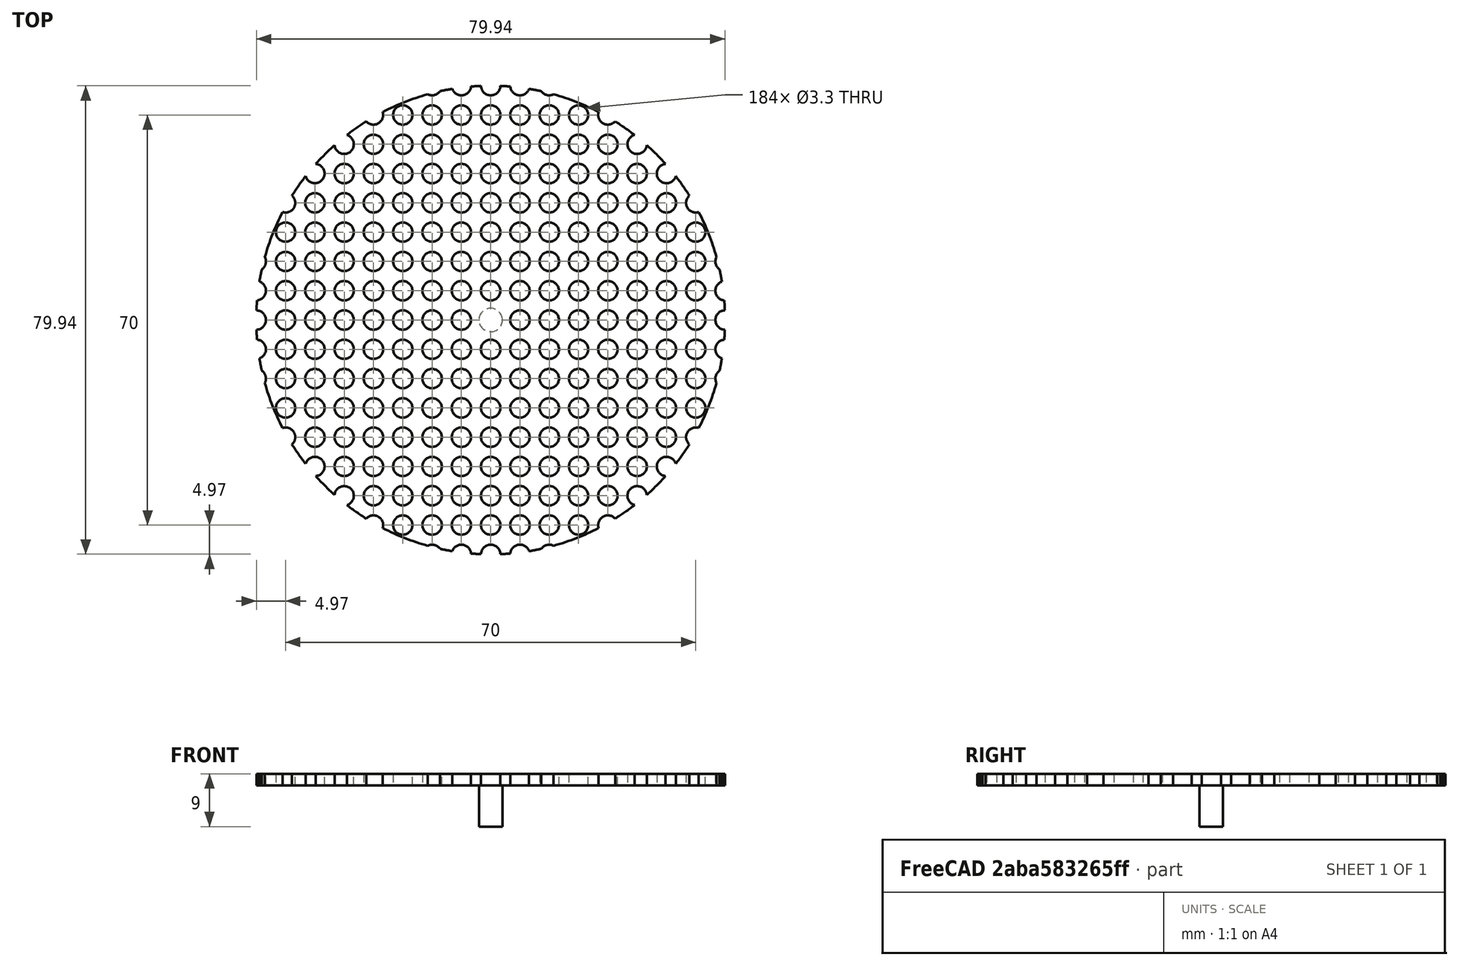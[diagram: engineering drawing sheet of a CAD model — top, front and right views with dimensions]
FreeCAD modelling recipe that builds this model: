
FCSTD DOCUMENT  (FreeCAD 0.21R0.21.1)
Label: XL30SampleholderBreadboard
License: All rights reserved
LicenseURL: https://en.wikipedia.org/wiki/All_rights_reserved
objects: Part::Cylinder×442, Part::MultiFuse×23, Spreadsheet::Sheet×1, Part::Cut×1
note: 466 computed .brp shape members not serialized (recipe doc carries the construction recipe); baked Part::Feature solids carry a one-line shape summary decoded from their .brp

FEATURE [Spreadsheet::Sheet] Spreadsheet  label="BreadboardConfig"
  cells = A1='Parameters; A2='Diameter of stage; B2(dia_breadboard)=80; C2='The outer diameter of the breadboard stage; A3='Corehole diameter; B3(screw_corehole)=3.3; C3='Corehole diameter for screws (3.3mm for M4); A4='Plate thickness; B4(t_plate)=2; A5='Hole spacing; B5(screw_spacing)=5
FEATURE [Part::Cylinder] Cylinder
  Angle = 360
  AttacherType = Attacher::AttachEngine3D
  FirstAngle = 0
  Height = 7
  Placement = pos=(0,0,-7) rot=(0,0,1;0rad)
  Radius = 2
  SecondAngle = 0
FEATURE [Part::Cylinder] Cylinder001
  Angle = 360
  AttacherType = Attacher::AttachEngine3D
  FirstAngle = 0
  Height = 2
  Radius = 40
  SecondAngle = 0
  expr: Height = <<BreadboardConfig>>.t_plate
  expr: Radius = <<BreadboardConfig>>.dia_breadboard / 2
FEATURE [Part::MultiFuse] Fusion
  Shapes = -> [Cylinder,Cylinder001]
FEATURE [Part::Cylinder] Cylinder002
  Angle = 360
  AttacherType = Attacher::AttachEngine3D
  FirstAngle = 0
  Height = 2
  Placement = pos=(5,0,0) rot=(0,0,1;0rad)
  Radius = 1.65
  SecondAngle = 0
  expr: .Placement.Base.x = <<BreadboardConfig>>.screw_spacing * 1
  expr: Height = <<BreadboardConfig>>.t_plate
  expr: Radius = <<BreadboardConfig>>.screw_corehole / 2
FEATURE [Part::Cylinder] Cylinder003
  Angle = 360
  AttacherType = Attacher::AttachEngine3D
  FirstAngle = 0
  Height = 2
  Placement = pos=(10,0,0) rot=(0,0,1;0rad)
  Radius = 1.65
  SecondAngle = 0
  expr: .Placement.Base.x = <<BreadboardConfig>>.screw_spacing * 2
  expr: Height = <<BreadboardConfig>>.t_plate
  expr: Radius = <<BreadboardConfig>>.screw_corehole / 2
FEATURE [Part::Cylinder] Cylinder004
  Angle = 360
  AttacherType = Attacher::AttachEngine3D
  FirstAngle = 0
  Height = 2
  Placement = pos=(15,0,0) rot=(0,0,1;0rad)
  Radius = 1.65
  SecondAngle = 0
  expr: .Placement.Base.x = <<BreadboardConfig>>.screw_spacing * 3
  expr: Height = <<BreadboardConfig>>.t_plate
  expr: Radius = <<BreadboardConfig>>.screw_corehole / 2
FEATURE [Part::Cylinder] Cylinder005
  Angle = 360
  AttacherType = Attacher::AttachEngine3D
  FirstAngle = 0
  Height = 2
  Placement = pos=(20,0,0) rot=(0,0,1;0rad)
  Radius = 1.65
  SecondAngle = 0
  expr: .Placement.Base.x = <<BreadboardConfig>>.screw_spacing * 4
  expr: Height = <<BreadboardConfig>>.t_plate
  expr: Radius = <<BreadboardConfig>>.screw_corehole / 2
FEATURE [Part::Cylinder] Cylinder006
  Angle = 360
  AttacherType = Attacher::AttachEngine3D
  FirstAngle = 0
  Height = 2
  Placement = pos=(25,0,0) rot=(0,0,1;0rad)
  Radius = 1.65
  SecondAngle = 0
  expr: .Placement.Base.x = <<BreadboardConfig>>.screw_spacing * 5
  expr: Height = <<BreadboardConfig>>.t_plate
  expr: Radius = <<BreadboardConfig>>.screw_corehole / 2
FEATURE [Part::Cylinder] Cylinder007
  Angle = 360
  AttacherType = Attacher::AttachEngine3D
  FirstAngle = 0
  Height = 2
  Placement = pos=(30,0,0) rot=(0,0,1;0rad)
  Radius = 1.65
  SecondAngle = 0
  expr: .Placement.Base.x = <<BreadboardConfig>>.screw_spacing * 6
  expr: Height = <<BreadboardConfig>>.t_plate
  expr: Radius = <<BreadboardConfig>>.screw_corehole / 2
FEATURE [Part::Cylinder] Cylinder008
  Angle = 360
  AttacherType = Attacher::AttachEngine3D
  FirstAngle = 0
  Height = 2
  Placement = pos=(35,0,0) rot=(0,0,1;0rad)
  Radius = 1.65
  SecondAngle = 0
  expr: .Placement.Base.x = <<BreadboardConfig>>.screw_spacing * 7
  expr: Height = <<BreadboardConfig>>.t_plate
  expr: Radius = <<BreadboardConfig>>.screw_corehole / 2
FEATURE [Part::Cylinder] Cylinder009
  Angle = 360
  AttacherType = Attacher::AttachEngine3D
  FirstAngle = 0
  Height = 2
  Placement = pos=(40,0,0) rot=(0,0,1;0rad)
  Radius = 1.65
  SecondAngle = 0
  expr: .Placement.Base.x = <<BreadboardConfig>>.screw_spacing * 8
  expr: Height = <<BreadboardConfig>>.t_plate
  expr: Radius = <<BreadboardConfig>>.screw_corehole / 2
FEATURE [Part::Cylinder] Cylinder010
  Angle = 360
  AttacherType = Attacher::AttachEngine3D
  FirstAngle = 0
  Height = 2
  Placement = pos=(45,0,0) rot=(0,0,1;0rad)
  Radius = 1.65
  SecondAngle = 0
  expr: .Placement.Base.x = <<BreadboardConfig>>.screw_spacing * 9
  expr: Height = <<BreadboardConfig>>.t_plate
  expr: Radius = <<BreadboardConfig>>.screw_corehole / 2
FEATURE [Part::Cylinder] Cylinder011
  Angle = 360
  AttacherType = Attacher::AttachEngine3D
  FirstAngle = 0
  Height = 2
  Placement = pos=(50,0,0) rot=(0,0,1;0rad)
  Radius = 1.65
  SecondAngle = 0
  expr: .Placement.Base.x = <<BreadboardConfig>>.screw_spacing * 10
  expr: Height = <<BreadboardConfig>>.t_plate
  expr: Radius = <<BreadboardConfig>>.screw_corehole / 2
FEATURE [Part::Cylinder] Cylinder012
  Angle = 360
  AttacherType = Attacher::AttachEngine3D
  FirstAngle = 0
  Height = 2
  Placement = pos=(-5,0,0) rot=(0,0,1;0rad)
  Radius = 1.65
  SecondAngle = 0
  expr: .Placement.Base.x = <<BreadboardConfig>>.screw_spacing * -1
  expr: Height = <<BreadboardConfig>>.t_plate
  expr: Radius = <<BreadboardConfig>>.screw_corehole / 2
FEATURE [Part::Cylinder] Cylinder013
  Angle = 360
  AttacherType = Attacher::AttachEngine3D
  FirstAngle = 0
  Height = 2
  Placement = pos=(-10,0,0) rot=(0,0,1;0rad)
  Radius = 1.65
  SecondAngle = 0
  expr: .Placement.Base.x = <<BreadboardConfig>>.screw_spacing * -2
  expr: Height = <<BreadboardConfig>>.t_plate
  expr: Radius = <<BreadboardConfig>>.screw_corehole / 2
FEATURE [Part::Cylinder] Cylinder014
  Angle = 360
  AttacherType = Attacher::AttachEngine3D
  FirstAngle = 0
  Height = 2
  Placement = pos=(-15,0,0) rot=(0,0,1;0rad)
  Radius = 1.65
  SecondAngle = 0
  expr: .Placement.Base.x = <<BreadboardConfig>>.screw_spacing * -3
  expr: Height = <<BreadboardConfig>>.t_plate
  expr: Radius = <<BreadboardConfig>>.screw_corehole / 2
FEATURE [Part::Cylinder] Cylinder015
  Angle = 360
  AttacherType = Attacher::AttachEngine3D
  FirstAngle = 0
  Height = 2
  Placement = pos=(-20,0,0) rot=(0,0,1;0rad)
  Radius = 1.65
  SecondAngle = 0
  expr: .Placement.Base.x = <<BreadboardConfig>>.screw_spacing * -4
  expr: Height = <<BreadboardConfig>>.t_plate
  expr: Radius = <<BreadboardConfig>>.screw_corehole / 2
FEATURE [Part::Cylinder] Cylinder016
  Angle = 360
  AttacherType = Attacher::AttachEngine3D
  FirstAngle = 0
  Height = 2
  Placement = pos=(-25,0,0) rot=(0,0,1;0rad)
  Radius = 1.65
  SecondAngle = 0
  expr: .Placement.Base.x = <<BreadboardConfig>>.screw_spacing * -5
  expr: Height = <<BreadboardConfig>>.t_plate
  expr: Radius = <<BreadboardConfig>>.screw_corehole / 2
FEATURE [Part::Cylinder] Cylinder017
  Angle = 360
  AttacherType = Attacher::AttachEngine3D
  FirstAngle = 0
  Height = 2
  Placement = pos=(-30,0,0) rot=(0,0,1;0rad)
  Radius = 1.65
  SecondAngle = 0
  expr: .Placement.Base.x = <<BreadboardConfig>>.screw_spacing * -6
  expr: Height = <<BreadboardConfig>>.t_plate
  expr: Radius = <<BreadboardConfig>>.screw_corehole / 2
FEATURE [Part::Cylinder] Cylinder018
  Angle = 360
  AttacherType = Attacher::AttachEngine3D
  FirstAngle = 0
  Height = 2
  Placement = pos=(-35,0,0) rot=(0,0,1;0rad)
  Radius = 1.65
  SecondAngle = 0
  expr: .Placement.Base.x = <<BreadboardConfig>>.screw_spacing * -7
  expr: Height = <<BreadboardConfig>>.t_plate
  expr: Radius = <<BreadboardConfig>>.screw_corehole / 2
FEATURE [Part::Cylinder] Cylinder019
  Angle = 360
  AttacherType = Attacher::AttachEngine3D
  FirstAngle = 0
  Height = 2
  Placement = pos=(-40,0,0) rot=(0,0,1;0rad)
  Radius = 1.65
  SecondAngle = 0
  expr: .Placement.Base.x = <<BreadboardConfig>>.screw_spacing * -8
  expr: Height = <<BreadboardConfig>>.t_plate
  expr: Radius = <<BreadboardConfig>>.screw_corehole / 2
FEATURE [Part::Cylinder] Cylinder020
  Angle = 360
  AttacherType = Attacher::AttachEngine3D
  FirstAngle = 0
  Height = 2
  Placement = pos=(-45,0,0) rot=(0,0,1;0rad)
  Radius = 1.65
  SecondAngle = 0
  expr: .Placement.Base.x = <<BreadboardConfig>>.screw_spacing * -9
  expr: Height = <<BreadboardConfig>>.t_plate
  expr: Radius = <<BreadboardConfig>>.screw_corehole / 2
FEATURE [Part::Cylinder] Cylinder021
  Angle = 360
  AttacherType = Attacher::AttachEngine3D
  FirstAngle = 0
  Height = 2
  Placement = pos=(-50,0,0) rot=(0,0,1;0rad)
  Radius = 1.65
  SecondAngle = 0
  expr: .Placement.Base.x = <<BreadboardConfig>>.screw_spacing * -10
  expr: Height = <<BreadboardConfig>>.t_plate
  expr: Radius = <<BreadboardConfig>>.screw_corehole / 2
FEATURE [Part::MultiFuse] Fusion001
  Shapes = -> [Cylinder021,Cylinder020,Cylinder019,Cylinder018,Cylinder017,Cylinder016,Cylinder015,Cylinder014,Cylinder013,Cylinder012,Cylinder011,Cylinder010,Cylinder009,Cylinder008,Cylinder007,Cylinder006,Cylinder005,Cylinder004,Cylinder003,Cylinder002]
FEATURE [Part::Cylinder] Cylinder022
  Angle = 360
  AttacherType = Attacher::AttachEngine3D
  FirstAngle = 0
  Height = 2
  Placement = pos=(5,0,0) rot=(0,0,1;0rad)
  Radius = 1.65
  SecondAngle = 0
  expr: .Placement.Base.x = <<BreadboardConfig>>.screw_spacing * 1
  expr: Height = <<BreadboardConfig>>.t_plate
  expr: Radius = <<BreadboardConfig>>.screw_corehole / 2
FEATURE [Part::Cylinder] Cylinder023
  Angle = 360
  AttacherType = Attacher::AttachEngine3D
  FirstAngle = 0
  Height = 2
  Placement = pos=(10,0,0) rot=(0,0,1;0rad)
  Radius = 1.65
  SecondAngle = 0
  expr: .Placement.Base.x = <<BreadboardConfig>>.screw_spacing * 2
  expr: Height = <<BreadboardConfig>>.t_plate
  expr: Radius = <<BreadboardConfig>>.screw_corehole / 2
FEATURE [Part::Cylinder] Cylinder024
  Angle = 360
  AttacherType = Attacher::AttachEngine3D
  FirstAngle = 0
  Height = 2
  Placement = pos=(15,0,0) rot=(0,0,1;0rad)
  Radius = 1.65
  SecondAngle = 0
  expr: .Placement.Base.x = <<BreadboardConfig>>.screw_spacing * 3
  expr: Height = <<BreadboardConfig>>.t_plate
  expr: Radius = <<BreadboardConfig>>.screw_corehole / 2
FEATURE [Part::Cylinder] Cylinder025
  Angle = 360
  AttacherType = Attacher::AttachEngine3D
  FirstAngle = 0
  Height = 2
  Placement = pos=(20,0,0) rot=(0,0,1;0rad)
  Radius = 1.65
  SecondAngle = 0
  expr: .Placement.Base.x = <<BreadboardConfig>>.screw_spacing * 4
  expr: Height = <<BreadboardConfig>>.t_plate
  expr: Radius = <<BreadboardConfig>>.screw_corehole / 2
FEATURE [Part::Cylinder] Cylinder026
  Angle = 360
  AttacherType = Attacher::AttachEngine3D
  FirstAngle = 0
  Height = 2
  Placement = pos=(25,0,0) rot=(0,0,1;0rad)
  Radius = 1.65
  SecondAngle = 0
  expr: .Placement.Base.x = <<BreadboardConfig>>.screw_spacing * 5
  expr: Height = <<BreadboardConfig>>.t_plate
  expr: Radius = <<BreadboardConfig>>.screw_corehole / 2
FEATURE [Part::Cylinder] Cylinder027
  Angle = 360
  AttacherType = Attacher::AttachEngine3D
  FirstAngle = 0
  Height = 2
  Placement = pos=(30,0,0) rot=(0,0,1;0rad)
  Radius = 1.65
  SecondAngle = 0
  expr: .Placement.Base.x = <<BreadboardConfig>>.screw_spacing * 6
  expr: Height = <<BreadboardConfig>>.t_plate
  expr: Radius = <<BreadboardConfig>>.screw_corehole / 2
FEATURE [Part::Cylinder] Cylinder028
  Angle = 360
  AttacherType = Attacher::AttachEngine3D
  FirstAngle = 0
  Height = 2
  Placement = pos=(35,0,0) rot=(0,0,1;0rad)
  Radius = 1.65
  SecondAngle = 0
  expr: .Placement.Base.x = <<BreadboardConfig>>.screw_spacing * 7
  expr: Height = <<BreadboardConfig>>.t_plate
  expr: Radius = <<BreadboardConfig>>.screw_corehole / 2
FEATURE [Part::Cylinder] Cylinder029
  Angle = 360
  AttacherType = Attacher::AttachEngine3D
  FirstAngle = 0
  Height = 2
  Placement = pos=(40,0,0) rot=(0,0,1;0rad)
  Radius = 1.65
  SecondAngle = 0
  expr: .Placement.Base.x = <<BreadboardConfig>>.screw_spacing * 8
  expr: Height = <<BreadboardConfig>>.t_plate
  expr: Radius = <<BreadboardConfig>>.screw_corehole / 2
FEATURE [Part::Cylinder] Cylinder030
  Angle = 360
  AttacherType = Attacher::AttachEngine3D
  FirstAngle = 0
  Height = 2
  Placement = pos=(45,0,0) rot=(0,0,1;0rad)
  Radius = 1.65
  SecondAngle = 0
  expr: .Placement.Base.x = <<BreadboardConfig>>.screw_spacing * 9
  expr: Height = <<BreadboardConfig>>.t_plate
  expr: Radius = <<BreadboardConfig>>.screw_corehole / 2
FEATURE [Part::Cylinder] Cylinder031
  Angle = 360
  AttacherType = Attacher::AttachEngine3D
  FirstAngle = 0
  Height = 2
  Placement = pos=(50,0,0) rot=(0,0,1;0rad)
  Radius = 1.65
  SecondAngle = 0
  expr: .Placement.Base.x = <<BreadboardConfig>>.screw_spacing * 10
  expr: Height = <<BreadboardConfig>>.t_plate
  expr: Radius = <<BreadboardConfig>>.screw_corehole / 2
FEATURE [Part::Cylinder] Cylinder032
  Angle = 360
  AttacherType = Attacher::AttachEngine3D
  FirstAngle = 0
  Height = 2
  Placement = pos=(-5,0,0) rot=(0,0,1;0rad)
  Radius = 1.65
  SecondAngle = 0
  expr: .Placement.Base.x = <<BreadboardConfig>>.screw_spacing * -1
  expr: Height = <<BreadboardConfig>>.t_plate
  expr: Radius = <<BreadboardConfig>>.screw_corehole / 2
FEATURE [Part::Cylinder] Cylinder033
  Angle = 360
  AttacherType = Attacher::AttachEngine3D
  FirstAngle = 0
  Height = 2
  Placement = pos=(-10,0,0) rot=(0,0,1;0rad)
  Radius = 1.65
  SecondAngle = 0
  expr: .Placement.Base.x = <<BreadboardConfig>>.screw_spacing * -2
  expr: Height = <<BreadboardConfig>>.t_plate
  expr: Radius = <<BreadboardConfig>>.screw_corehole / 2
FEATURE [Part::Cylinder] Cylinder034
  Angle = 360
  AttacherType = Attacher::AttachEngine3D
  FirstAngle = 0
  Height = 2
  Placement = pos=(-15,0,0) rot=(0,0,1;0rad)
  Radius = 1.65
  SecondAngle = 0
  expr: .Placement.Base.x = <<BreadboardConfig>>.screw_spacing * -3
  expr: Height = <<BreadboardConfig>>.t_plate
  expr: Radius = <<BreadboardConfig>>.screw_corehole / 2
FEATURE [Part::Cylinder] Cylinder035
  Angle = 360
  AttacherType = Attacher::AttachEngine3D
  FirstAngle = 0
  Height = 2
  Placement = pos=(-20,0,0) rot=(0,0,1;0rad)
  Radius = 1.65
  SecondAngle = 0
  expr: .Placement.Base.x = <<BreadboardConfig>>.screw_spacing * -4
  expr: Height = <<BreadboardConfig>>.t_plate
  expr: Radius = <<BreadboardConfig>>.screw_corehole / 2
FEATURE [Part::Cylinder] Cylinder036
  Angle = 360
  AttacherType = Attacher::AttachEngine3D
  FirstAngle = 0
  Height = 2
  Placement = pos=(-25,0,0) rot=(0,0,1;0rad)
  Radius = 1.65
  SecondAngle = 0
  expr: .Placement.Base.x = <<BreadboardConfig>>.screw_spacing * -5
  expr: Height = <<BreadboardConfig>>.t_plate
  expr: Radius = <<BreadboardConfig>>.screw_corehole / 2
FEATURE [Part::Cylinder] Cylinder037
  Angle = 360
  AttacherType = Attacher::AttachEngine3D
  FirstAngle = 0
  Height = 2
  Placement = pos=(-30,0,0) rot=(0,0,1;0rad)
  Radius = 1.65
  SecondAngle = 0
  expr: .Placement.Base.x = <<BreadboardConfig>>.screw_spacing * -6
  expr: Height = <<BreadboardConfig>>.t_plate
  expr: Radius = <<BreadboardConfig>>.screw_corehole / 2
FEATURE [Part::Cylinder] Cylinder038
  Angle = 360
  AttacherType = Attacher::AttachEngine3D
  FirstAngle = 0
  Height = 2
  Placement = pos=(-35,0,0) rot=(0,0,1;0rad)
  Radius = 1.65
  SecondAngle = 0
  expr: .Placement.Base.x = <<BreadboardConfig>>.screw_spacing * -7
  expr: Height = <<BreadboardConfig>>.t_plate
  expr: Radius = <<BreadboardConfig>>.screw_corehole / 2
FEATURE [Part::Cylinder] Cylinder039
  Angle = 360
  AttacherType = Attacher::AttachEngine3D
  FirstAngle = 0
  Height = 2
  Placement = pos=(-40,0,0) rot=(0,0,1;0rad)
  Radius = 1.65
  SecondAngle = 0
  expr: .Placement.Base.x = <<BreadboardConfig>>.screw_spacing * -8
  expr: Height = <<BreadboardConfig>>.t_plate
  expr: Radius = <<BreadboardConfig>>.screw_corehole / 2
FEATURE [Part::Cylinder] Cylinder040
  Angle = 360
  AttacherType = Attacher::AttachEngine3D
  FirstAngle = 0
  Height = 2
  Placement = pos=(-45,0,0) rot=(0,0,1;0rad)
  Radius = 1.65
  SecondAngle = 0
  expr: .Placement.Base.x = <<BreadboardConfig>>.screw_spacing * -9
  expr: Height = <<BreadboardConfig>>.t_plate
  expr: Radius = <<BreadboardConfig>>.screw_corehole / 2
FEATURE [Part::Cylinder] Cylinder041
  Angle = 360
  AttacherType = Attacher::AttachEngine3D
  FirstAngle = 0
  Height = 2
  Placement = pos=(-50,0,0) rot=(0,0,1;0rad)
  Radius = 1.65
  SecondAngle = 0
  expr: .Placement.Base.x = <<BreadboardConfig>>.screw_spacing * -10
  expr: Height = <<BreadboardConfig>>.t_plate
  expr: Radius = <<BreadboardConfig>>.screw_corehole / 2
FEATURE [Part::Cylinder] Cylinder042
  Angle = 360
  AttacherType = Attacher::AttachEngine3D
  FirstAngle = 0
  Height = 2
  Radius = 1.65
  SecondAngle = 0
  expr: Height = <<BreadboardConfig>>.t_plate
  expr: Radius = <<BreadboardConfig>>.screw_corehole / 2
FEATURE [Part::MultiFuse] Fusion002
  Placement = pos=(0,5,0) rot=(0,0,1;0rad)
  Shapes = -> [Cylinder041,Cylinder040,Cylinder039,Cylinder038,Cylinder037,Cylinder036,Cylinder035,Cylinder034,Cylinder033,Cylinder032,Cylinder031,Cylinder030,Cylinder029,Cylinder028,Cylinder027,Cylinder026,Cylinder025,Cylinder024,Cylinder023,Cylinder022,Cylinder042]
  expr: .Placement.Base.y = <<BreadboardConfig>>.screw_spacing
FEATURE [Part::Cylinder] Cylinder043
  Angle = 360
  AttacherType = Attacher::AttachEngine3D
  FirstAngle = 0
  Height = 2
  Placement = pos=(5,0,0) rot=(0,0,1;0rad)
  Radius = 1.65
  SecondAngle = 0
  expr: .Placement.Base.x = <<BreadboardConfig>>.screw_spacing * 1
  expr: Height = <<BreadboardConfig>>.t_plate
  expr: Radius = <<BreadboardConfig>>.screw_corehole / 2
FEATURE [Part::Cylinder] Cylinder044
  Angle = 360
  AttacherType = Attacher::AttachEngine3D
  FirstAngle = 0
  Height = 2
  Placement = pos=(10,0,0) rot=(0,0,1;0rad)
  Radius = 1.65
  SecondAngle = 0
  expr: .Placement.Base.x = <<BreadboardConfig>>.screw_spacing * 2
  expr: Height = <<BreadboardConfig>>.t_plate
  expr: Radius = <<BreadboardConfig>>.screw_corehole / 2
FEATURE [Part::Cylinder] Cylinder045
  Angle = 360
  AttacherType = Attacher::AttachEngine3D
  FirstAngle = 0
  Height = 2
  Placement = pos=(15,0,0) rot=(0,0,1;0rad)
  Radius = 1.65
  SecondAngle = 0
  expr: .Placement.Base.x = <<BreadboardConfig>>.screw_spacing * 3
  expr: Height = <<BreadboardConfig>>.t_plate
  expr: Radius = <<BreadboardConfig>>.screw_corehole / 2
FEATURE [Part::Cylinder] Cylinder046
  Angle = 360
  AttacherType = Attacher::AttachEngine3D
  FirstAngle = 0
  Height = 2
  Placement = pos=(20,0,0) rot=(0,0,1;0rad)
  Radius = 1.65
  SecondAngle = 0
  expr: .Placement.Base.x = <<BreadboardConfig>>.screw_spacing * 4
  expr: Height = <<BreadboardConfig>>.t_plate
  expr: Radius = <<BreadboardConfig>>.screw_corehole / 2
FEATURE [Part::Cylinder] Cylinder047
  Angle = 360
  AttacherType = Attacher::AttachEngine3D
  FirstAngle = 0
  Height = 2
  Placement = pos=(25,0,0) rot=(0,0,1;0rad)
  Radius = 1.65
  SecondAngle = 0
  expr: .Placement.Base.x = <<BreadboardConfig>>.screw_spacing * 5
  expr: Height = <<BreadboardConfig>>.t_plate
  expr: Radius = <<BreadboardConfig>>.screw_corehole / 2
FEATURE [Part::Cylinder] Cylinder048
  Angle = 360
  AttacherType = Attacher::AttachEngine3D
  FirstAngle = 0
  Height = 2
  Placement = pos=(30,0,0) rot=(0,0,1;0rad)
  Radius = 1.65
  SecondAngle = 0
  expr: .Placement.Base.x = <<BreadboardConfig>>.screw_spacing * 6
  expr: Height = <<BreadboardConfig>>.t_plate
  expr: Radius = <<BreadboardConfig>>.screw_corehole / 2
FEATURE [Part::Cylinder] Cylinder049
  Angle = 360
  AttacherType = Attacher::AttachEngine3D
  FirstAngle = 0
  Height = 2
  Placement = pos=(35,0,0) rot=(0,0,1;0rad)
  Radius = 1.65
  SecondAngle = 0
  expr: .Placement.Base.x = <<BreadboardConfig>>.screw_spacing * 7
  expr: Height = <<BreadboardConfig>>.t_plate
  expr: Radius = <<BreadboardConfig>>.screw_corehole / 2
FEATURE [Part::Cylinder] Cylinder050
  Angle = 360
  AttacherType = Attacher::AttachEngine3D
  FirstAngle = 0
  Height = 2
  Placement = pos=(40,0,0) rot=(0,0,1;0rad)
  Radius = 1.65
  SecondAngle = 0
  expr: .Placement.Base.x = <<BreadboardConfig>>.screw_spacing * 8
  expr: Height = <<BreadboardConfig>>.t_plate
  expr: Radius = <<BreadboardConfig>>.screw_corehole / 2
FEATURE [Part::Cylinder] Cylinder051
  Angle = 360
  AttacherType = Attacher::AttachEngine3D
  FirstAngle = 0
  Height = 2
  Placement = pos=(45,0,0) rot=(0,0,1;0rad)
  Radius = 1.65
  SecondAngle = 0
  expr: .Placement.Base.x = <<BreadboardConfig>>.screw_spacing * 9
  expr: Height = <<BreadboardConfig>>.t_plate
  expr: Radius = <<BreadboardConfig>>.screw_corehole / 2
FEATURE [Part::Cylinder] Cylinder052
  Angle = 360
  AttacherType = Attacher::AttachEngine3D
  FirstAngle = 0
  Height = 2
  Placement = pos=(50,0,0) rot=(0,0,1;0rad)
  Radius = 1.65
  SecondAngle = 0
  expr: .Placement.Base.x = <<BreadboardConfig>>.screw_spacing * 10
  expr: Height = <<BreadboardConfig>>.t_plate
  expr: Radius = <<BreadboardConfig>>.screw_corehole / 2
FEATURE [Part::Cylinder] Cylinder053
  Angle = 360
  AttacherType = Attacher::AttachEngine3D
  FirstAngle = 0
  Height = 2
  Placement = pos=(-5,0,0) rot=(0,0,1;0rad)
  Radius = 1.65
  SecondAngle = 0
  expr: .Placement.Base.x = <<BreadboardConfig>>.screw_spacing * -1
  expr: Height = <<BreadboardConfig>>.t_plate
  expr: Radius = <<BreadboardConfig>>.screw_corehole / 2
FEATURE [Part::Cylinder] Cylinder054
  Angle = 360
  AttacherType = Attacher::AttachEngine3D
  FirstAngle = 0
  Height = 2
  Placement = pos=(-10,0,0) rot=(0,0,1;0rad)
  Radius = 1.65
  SecondAngle = 0
  expr: .Placement.Base.x = <<BreadboardConfig>>.screw_spacing * -2
  expr: Height = <<BreadboardConfig>>.t_plate
  expr: Radius = <<BreadboardConfig>>.screw_corehole / 2
FEATURE [Part::Cylinder] Cylinder055
  Angle = 360
  AttacherType = Attacher::AttachEngine3D
  FirstAngle = 0
  Height = 2
  Placement = pos=(-15,0,0) rot=(0,0,1;0rad)
  Radius = 1.65
  SecondAngle = 0
  expr: .Placement.Base.x = <<BreadboardConfig>>.screw_spacing * -3
  expr: Height = <<BreadboardConfig>>.t_plate
  expr: Radius = <<BreadboardConfig>>.screw_corehole / 2
FEATURE [Part::Cylinder] Cylinder056
  Angle = 360
  AttacherType = Attacher::AttachEngine3D
  FirstAngle = 0
  Height = 2
  Placement = pos=(-20,0,0) rot=(0,0,1;0rad)
  Radius = 1.65
  SecondAngle = 0
  expr: .Placement.Base.x = <<BreadboardConfig>>.screw_spacing * -4
  expr: Height = <<BreadboardConfig>>.t_plate
  expr: Radius = <<BreadboardConfig>>.screw_corehole / 2
FEATURE [Part::Cylinder] Cylinder057
  Angle = 360
  AttacherType = Attacher::AttachEngine3D
  FirstAngle = 0
  Height = 2
  Placement = pos=(-25,0,0) rot=(0,0,1;0rad)
  Radius = 1.65
  SecondAngle = 0
  expr: .Placement.Base.x = <<BreadboardConfig>>.screw_spacing * -5
  expr: Height = <<BreadboardConfig>>.t_plate
  expr: Radius = <<BreadboardConfig>>.screw_corehole / 2
FEATURE [Part::Cylinder] Cylinder058
  Angle = 360
  AttacherType = Attacher::AttachEngine3D
  FirstAngle = 0
  Height = 2
  Placement = pos=(-30,0,0) rot=(0,0,1;0rad)
  Radius = 1.65
  SecondAngle = 0
  expr: .Placement.Base.x = <<BreadboardConfig>>.screw_spacing * -6
  expr: Height = <<BreadboardConfig>>.t_plate
  expr: Radius = <<BreadboardConfig>>.screw_corehole / 2
FEATURE [Part::Cylinder] Cylinder059
  Angle = 360
  AttacherType = Attacher::AttachEngine3D
  FirstAngle = 0
  Height = 2
  Placement = pos=(-35,0,0) rot=(0,0,1;0rad)
  Radius = 1.65
  SecondAngle = 0
  expr: .Placement.Base.x = <<BreadboardConfig>>.screw_spacing * -7
  expr: Height = <<BreadboardConfig>>.t_plate
  expr: Radius = <<BreadboardConfig>>.screw_corehole / 2
FEATURE [Part::Cylinder] Cylinder060
  Angle = 360
  AttacherType = Attacher::AttachEngine3D
  FirstAngle = 0
  Height = 2
  Placement = pos=(-40,0,0) rot=(0,0,1;0rad)
  Radius = 1.65
  SecondAngle = 0
  expr: .Placement.Base.x = <<BreadboardConfig>>.screw_spacing * -8
  expr: Height = <<BreadboardConfig>>.t_plate
  expr: Radius = <<BreadboardConfig>>.screw_corehole / 2
FEATURE [Part::Cylinder] Cylinder061
  Angle = 360
  AttacherType = Attacher::AttachEngine3D
  FirstAngle = 0
  Height = 2
  Placement = pos=(-45,0,0) rot=(0,0,1;0rad)
  Radius = 1.65
  SecondAngle = 0
  expr: .Placement.Base.x = <<BreadboardConfig>>.screw_spacing * -9
  expr: Height = <<BreadboardConfig>>.t_plate
  expr: Radius = <<BreadboardConfig>>.screw_corehole / 2
FEATURE [Part::Cylinder] Cylinder062
  Angle = 360
  AttacherType = Attacher::AttachEngine3D
  FirstAngle = 0
  Height = 2
  Placement = pos=(-50,0,0) rot=(0,0,1;0rad)
  Radius = 1.65
  SecondAngle = 0
  expr: .Placement.Base.x = <<BreadboardConfig>>.screw_spacing * -10
  expr: Height = <<BreadboardConfig>>.t_plate
  expr: Radius = <<BreadboardConfig>>.screw_corehole / 2
FEATURE [Part::Cylinder] Cylinder063
  Angle = 360
  AttacherType = Attacher::AttachEngine3D
  FirstAngle = 0
  Height = 2
  Radius = 1.65
  SecondAngle = 0
  expr: Height = <<BreadboardConfig>>.t_plate
  expr: Radius = <<BreadboardConfig>>.screw_corehole / 2
FEATURE [Part::MultiFuse] Fusion003
  Placement = pos=(0,10,0) rot=(0,0,1;0rad)
  Shapes = -> [Cylinder062,Cylinder061,Cylinder060,Cylinder059,Cylinder058,Cylinder057,Cylinder056,Cylinder055,Cylinder054,Cylinder053,Cylinder052,Cylinder051,Cylinder050,Cylinder049,Cylinder048,Cylinder047,Cylinder046,Cylinder045,Cylinder044,Cylinder043,Cylinder063]
  expr: .Placement.Base.y = <<BreadboardConfig>>.screw_spacing * 2
FEATURE [Part::Cylinder] Cylinder064
  Angle = 360
  AttacherType = Attacher::AttachEngine3D
  FirstAngle = 0
  Height = 2
  Placement = pos=(5,0,0) rot=(0,0,1;0rad)
  Radius = 1.65
  SecondAngle = 0
  expr: .Placement.Base.x = <<BreadboardConfig>>.screw_spacing * 1
  expr: Height = <<BreadboardConfig>>.t_plate
  expr: Radius = <<BreadboardConfig>>.screw_corehole / 2
FEATURE [Part::Cylinder] Cylinder065
  Angle = 360
  AttacherType = Attacher::AttachEngine3D
  FirstAngle = 0
  Height = 2
  Placement = pos=(10,0,0) rot=(0,0,1;0rad)
  Radius = 1.65
  SecondAngle = 0
  expr: .Placement.Base.x = <<BreadboardConfig>>.screw_spacing * 2
  expr: Height = <<BreadboardConfig>>.t_plate
  expr: Radius = <<BreadboardConfig>>.screw_corehole / 2
FEATURE [Part::Cylinder] Cylinder066
  Angle = 360
  AttacherType = Attacher::AttachEngine3D
  FirstAngle = 0
  Height = 2
  Placement = pos=(15,0,0) rot=(0,0,1;0rad)
  Radius = 1.65
  SecondAngle = 0
  expr: .Placement.Base.x = <<BreadboardConfig>>.screw_spacing * 3
  expr: Height = <<BreadboardConfig>>.t_plate
  expr: Radius = <<BreadboardConfig>>.screw_corehole / 2
FEATURE [Part::Cylinder] Cylinder067
  Angle = 360
  AttacherType = Attacher::AttachEngine3D
  FirstAngle = 0
  Height = 2
  Placement = pos=(20,0,0) rot=(0,0,1;0rad)
  Radius = 1.65
  SecondAngle = 0
  expr: .Placement.Base.x = <<BreadboardConfig>>.screw_spacing * 4
  expr: Height = <<BreadboardConfig>>.t_plate
  expr: Radius = <<BreadboardConfig>>.screw_corehole / 2
FEATURE [Part::Cylinder] Cylinder068
  Angle = 360
  AttacherType = Attacher::AttachEngine3D
  FirstAngle = 0
  Height = 2
  Placement = pos=(25,0,0) rot=(0,0,1;0rad)
  Radius = 1.65
  SecondAngle = 0
  expr: .Placement.Base.x = <<BreadboardConfig>>.screw_spacing * 5
  expr: Height = <<BreadboardConfig>>.t_plate
  expr: Radius = <<BreadboardConfig>>.screw_corehole / 2
FEATURE [Part::Cylinder] Cylinder069
  Angle = 360
  AttacherType = Attacher::AttachEngine3D
  FirstAngle = 0
  Height = 2
  Placement = pos=(30,0,0) rot=(0,0,1;0rad)
  Radius = 1.65
  SecondAngle = 0
  expr: .Placement.Base.x = <<BreadboardConfig>>.screw_spacing * 6
  expr: Height = <<BreadboardConfig>>.t_plate
  expr: Radius = <<BreadboardConfig>>.screw_corehole / 2
FEATURE [Part::Cylinder] Cylinder070
  Angle = 360
  AttacherType = Attacher::AttachEngine3D
  FirstAngle = 0
  Height = 2
  Placement = pos=(35,0,0) rot=(0,0,1;0rad)
  Radius = 1.65
  SecondAngle = 0
  expr: .Placement.Base.x = <<BreadboardConfig>>.screw_spacing * 7
  expr: Height = <<BreadboardConfig>>.t_plate
  expr: Radius = <<BreadboardConfig>>.screw_corehole / 2
FEATURE [Part::Cylinder] Cylinder071
  Angle = 360
  AttacherType = Attacher::AttachEngine3D
  FirstAngle = 0
  Height = 2
  Placement = pos=(40,0,0) rot=(0,0,1;0rad)
  Radius = 1.65
  SecondAngle = 0
  expr: .Placement.Base.x = <<BreadboardConfig>>.screw_spacing * 8
  expr: Height = <<BreadboardConfig>>.t_plate
  expr: Radius = <<BreadboardConfig>>.screw_corehole / 2
FEATURE [Part::Cylinder] Cylinder072
  Angle = 360
  AttacherType = Attacher::AttachEngine3D
  FirstAngle = 0
  Height = 2
  Placement = pos=(45,0,0) rot=(0,0,1;0rad)
  Radius = 1.65
  SecondAngle = 0
  expr: .Placement.Base.x = <<BreadboardConfig>>.screw_spacing * 9
  expr: Height = <<BreadboardConfig>>.t_plate
  expr: Radius = <<BreadboardConfig>>.screw_corehole / 2
FEATURE [Part::Cylinder] Cylinder073
  Angle = 360
  AttacherType = Attacher::AttachEngine3D
  FirstAngle = 0
  Height = 2
  Placement = pos=(50,0,0) rot=(0,0,1;0rad)
  Radius = 1.65
  SecondAngle = 0
  expr: .Placement.Base.x = <<BreadboardConfig>>.screw_spacing * 10
  expr: Height = <<BreadboardConfig>>.t_plate
  expr: Radius = <<BreadboardConfig>>.screw_corehole / 2
FEATURE [Part::Cylinder] Cylinder074
  Angle = 360
  AttacherType = Attacher::AttachEngine3D
  FirstAngle = 0
  Height = 2
  Placement = pos=(-5,0,0) rot=(0,0,1;0rad)
  Radius = 1.65
  SecondAngle = 0
  expr: .Placement.Base.x = <<BreadboardConfig>>.screw_spacing * -1
  expr: Height = <<BreadboardConfig>>.t_plate
  expr: Radius = <<BreadboardConfig>>.screw_corehole / 2
FEATURE [Part::Cylinder] Cylinder075
  Angle = 360
  AttacherType = Attacher::AttachEngine3D
  FirstAngle = 0
  Height = 2
  Placement = pos=(-10,0,0) rot=(0,0,1;0rad)
  Radius = 1.65
  SecondAngle = 0
  expr: .Placement.Base.x = <<BreadboardConfig>>.screw_spacing * -2
  expr: Height = <<BreadboardConfig>>.t_plate
  expr: Radius = <<BreadboardConfig>>.screw_corehole / 2
FEATURE [Part::Cylinder] Cylinder076
  Angle = 360
  AttacherType = Attacher::AttachEngine3D
  FirstAngle = 0
  Height = 2
  Placement = pos=(-15,0,0) rot=(0,0,1;0rad)
  Radius = 1.65
  SecondAngle = 0
  expr: .Placement.Base.x = <<BreadboardConfig>>.screw_spacing * -3
  expr: Height = <<BreadboardConfig>>.t_plate
  expr: Radius = <<BreadboardConfig>>.screw_corehole / 2
FEATURE [Part::Cylinder] Cylinder077
  Angle = 360
  AttacherType = Attacher::AttachEngine3D
  FirstAngle = 0
  Height = 2
  Placement = pos=(-20,0,0) rot=(0,0,1;0rad)
  Radius = 1.65
  SecondAngle = 0
  expr: .Placement.Base.x = <<BreadboardConfig>>.screw_spacing * -4
  expr: Height = <<BreadboardConfig>>.t_plate
  expr: Radius = <<BreadboardConfig>>.screw_corehole / 2
FEATURE [Part::Cylinder] Cylinder078
  Angle = 360
  AttacherType = Attacher::AttachEngine3D
  FirstAngle = 0
  Height = 2
  Placement = pos=(-25,0,0) rot=(0,0,1;0rad)
  Radius = 1.65
  SecondAngle = 0
  expr: .Placement.Base.x = <<BreadboardConfig>>.screw_spacing * -5
  expr: Height = <<BreadboardConfig>>.t_plate
  expr: Radius = <<BreadboardConfig>>.screw_corehole / 2
FEATURE [Part::Cylinder] Cylinder079
  Angle = 360
  AttacherType = Attacher::AttachEngine3D
  FirstAngle = 0
  Height = 2
  Placement = pos=(-30,0,0) rot=(0,0,1;0rad)
  Radius = 1.65
  SecondAngle = 0
  expr: .Placement.Base.x = <<BreadboardConfig>>.screw_spacing * -6
  expr: Height = <<BreadboardConfig>>.t_plate
  expr: Radius = <<BreadboardConfig>>.screw_corehole / 2
FEATURE [Part::Cylinder] Cylinder080
  Angle = 360
  AttacherType = Attacher::AttachEngine3D
  FirstAngle = 0
  Height = 2
  Placement = pos=(-35,0,0) rot=(0,0,1;0rad)
  Radius = 1.65
  SecondAngle = 0
  expr: .Placement.Base.x = <<BreadboardConfig>>.screw_spacing * -7
  expr: Height = <<BreadboardConfig>>.t_plate
  expr: Radius = <<BreadboardConfig>>.screw_corehole / 2
FEATURE [Part::Cylinder] Cylinder081
  Angle = 360
  AttacherType = Attacher::AttachEngine3D
  FirstAngle = 0
  Height = 2
  Placement = pos=(-40,0,0) rot=(0,0,1;0rad)
  Radius = 1.65
  SecondAngle = 0
  expr: .Placement.Base.x = <<BreadboardConfig>>.screw_spacing * -8
  expr: Height = <<BreadboardConfig>>.t_plate
  expr: Radius = <<BreadboardConfig>>.screw_corehole / 2
FEATURE [Part::Cylinder] Cylinder082
  Angle = 360
  AttacherType = Attacher::AttachEngine3D
  FirstAngle = 0
  Height = 2
  Placement = pos=(-45,0,0) rot=(0,0,1;0rad)
  Radius = 1.65
  SecondAngle = 0
  expr: .Placement.Base.x = <<BreadboardConfig>>.screw_spacing * -9
  expr: Height = <<BreadboardConfig>>.t_plate
  expr: Radius = <<BreadboardConfig>>.screw_corehole / 2
FEATURE [Part::Cylinder] Cylinder083
  Angle = 360
  AttacherType = Attacher::AttachEngine3D
  FirstAngle = 0
  Height = 2
  Placement = pos=(-50,0,0) rot=(0,0,1;0rad)
  Radius = 1.65
  SecondAngle = 0
  expr: .Placement.Base.x = <<BreadboardConfig>>.screw_spacing * -10
  expr: Height = <<BreadboardConfig>>.t_plate
  expr: Radius = <<BreadboardConfig>>.screw_corehole / 2
FEATURE [Part::Cylinder] Cylinder084
  Angle = 360
  AttacherType = Attacher::AttachEngine3D
  FirstAngle = 0
  Height = 2
  Radius = 1.65
  SecondAngle = 0
  expr: Height = <<BreadboardConfig>>.t_plate
  expr: Radius = <<BreadboardConfig>>.screw_corehole / 2
FEATURE [Part::MultiFuse] Fusion004
  Placement = pos=(0,15,0) rot=(0,0,1;0rad)
  Shapes = -> [Cylinder083,Cylinder082,Cylinder081,Cylinder080,Cylinder079,Cylinder078,Cylinder077,Cylinder076,Cylinder075,Cylinder074,Cylinder073,Cylinder072,Cylinder071,Cylinder070,Cylinder069,Cylinder068,Cylinder067,Cylinder066,Cylinder065,Cylinder064,Cylinder084]
  expr: .Placement.Base.y = <<BreadboardConfig>>.screw_spacing * 3
FEATURE [Part::Cylinder] Cylinder085
  Angle = 360
  AttacherType = Attacher::AttachEngine3D
  FirstAngle = 0
  Height = 2
  Placement = pos=(5,0,0) rot=(0,0,1;0rad)
  Radius = 1.65
  SecondAngle = 0
  expr: .Placement.Base.x = <<BreadboardConfig>>.screw_spacing * 1
  expr: Height = <<BreadboardConfig>>.t_plate
  expr: Radius = <<BreadboardConfig>>.screw_corehole / 2
FEATURE [Part::Cylinder] Cylinder086
  Angle = 360
  AttacherType = Attacher::AttachEngine3D
  FirstAngle = 0
  Height = 2
  Placement = pos=(10,0,0) rot=(0,0,1;0rad)
  Radius = 1.65
  SecondAngle = 0
  expr: .Placement.Base.x = <<BreadboardConfig>>.screw_spacing * 2
  expr: Height = <<BreadboardConfig>>.t_plate
  expr: Radius = <<BreadboardConfig>>.screw_corehole / 2
FEATURE [Part::Cylinder] Cylinder087
  Angle = 360
  AttacherType = Attacher::AttachEngine3D
  FirstAngle = 0
  Height = 2
  Placement = pos=(15,0,0) rot=(0,0,1;0rad)
  Radius = 1.65
  SecondAngle = 0
  expr: .Placement.Base.x = <<BreadboardConfig>>.screw_spacing * 3
  expr: Height = <<BreadboardConfig>>.t_plate
  expr: Radius = <<BreadboardConfig>>.screw_corehole / 2
FEATURE [Part::Cylinder] Cylinder088
  Angle = 360
  AttacherType = Attacher::AttachEngine3D
  FirstAngle = 0
  Height = 2
  Placement = pos=(20,0,0) rot=(0,0,1;0rad)
  Radius = 1.65
  SecondAngle = 0
  expr: .Placement.Base.x = <<BreadboardConfig>>.screw_spacing * 4
  expr: Height = <<BreadboardConfig>>.t_plate
  expr: Radius = <<BreadboardConfig>>.screw_corehole / 2
FEATURE [Part::Cylinder] Cylinder089
  Angle = 360
  AttacherType = Attacher::AttachEngine3D
  FirstAngle = 0
  Height = 2
  Placement = pos=(25,0,0) rot=(0,0,1;0rad)
  Radius = 1.65
  SecondAngle = 0
  expr: .Placement.Base.x = <<BreadboardConfig>>.screw_spacing * 5
  expr: Height = <<BreadboardConfig>>.t_plate
  expr: Radius = <<BreadboardConfig>>.screw_corehole / 2
FEATURE [Part::Cylinder] Cylinder090
  Angle = 360
  AttacherType = Attacher::AttachEngine3D
  FirstAngle = 0
  Height = 2
  Placement = pos=(30,0,0) rot=(0,0,1;0rad)
  Radius = 1.65
  SecondAngle = 0
  expr: .Placement.Base.x = <<BreadboardConfig>>.screw_spacing * 6
  expr: Height = <<BreadboardConfig>>.t_plate
  expr: Radius = <<BreadboardConfig>>.screw_corehole / 2
FEATURE [Part::Cylinder] Cylinder091
  Angle = 360
  AttacherType = Attacher::AttachEngine3D
  FirstAngle = 0
  Height = 2
  Placement = pos=(35,0,0) rot=(0,0,1;0rad)
  Radius = 1.65
  SecondAngle = 0
  expr: .Placement.Base.x = <<BreadboardConfig>>.screw_spacing * 7
  expr: Height = <<BreadboardConfig>>.t_plate
  expr: Radius = <<BreadboardConfig>>.screw_corehole / 2
FEATURE [Part::Cylinder] Cylinder092
  Angle = 360
  AttacherType = Attacher::AttachEngine3D
  FirstAngle = 0
  Height = 2
  Placement = pos=(40,0,0) rot=(0,0,1;0rad)
  Radius = 1.65
  SecondAngle = 0
  expr: .Placement.Base.x = <<BreadboardConfig>>.screw_spacing * 8
  expr: Height = <<BreadboardConfig>>.t_plate
  expr: Radius = <<BreadboardConfig>>.screw_corehole / 2
FEATURE [Part::Cylinder] Cylinder093
  Angle = 360
  AttacherType = Attacher::AttachEngine3D
  FirstAngle = 0
  Height = 2
  Placement = pos=(45,0,0) rot=(0,0,1;0rad)
  Radius = 1.65
  SecondAngle = 0
  expr: .Placement.Base.x = <<BreadboardConfig>>.screw_spacing * 9
  expr: Height = <<BreadboardConfig>>.t_plate
  expr: Radius = <<BreadboardConfig>>.screw_corehole / 2
FEATURE [Part::Cylinder] Cylinder094
  Angle = 360
  AttacherType = Attacher::AttachEngine3D
  FirstAngle = 0
  Height = 2
  Placement = pos=(50,0,0) rot=(0,0,1;0rad)
  Radius = 1.65
  SecondAngle = 0
  expr: .Placement.Base.x = <<BreadboardConfig>>.screw_spacing * 10
  expr: Height = <<BreadboardConfig>>.t_plate
  expr: Radius = <<BreadboardConfig>>.screw_corehole / 2
FEATURE [Part::Cylinder] Cylinder095
  Angle = 360
  AttacherType = Attacher::AttachEngine3D
  FirstAngle = 0
  Height = 2
  Placement = pos=(-5,0,0) rot=(0,0,1;0rad)
  Radius = 1.65
  SecondAngle = 0
  expr: .Placement.Base.x = <<BreadboardConfig>>.screw_spacing * -1
  expr: Height = <<BreadboardConfig>>.t_plate
  expr: Radius = <<BreadboardConfig>>.screw_corehole / 2
FEATURE [Part::Cylinder] Cylinder096
  Angle = 360
  AttacherType = Attacher::AttachEngine3D
  FirstAngle = 0
  Height = 2
  Placement = pos=(-10,0,0) rot=(0,0,1;0rad)
  Radius = 1.65
  SecondAngle = 0
  expr: .Placement.Base.x = <<BreadboardConfig>>.screw_spacing * -2
  expr: Height = <<BreadboardConfig>>.t_plate
  expr: Radius = <<BreadboardConfig>>.screw_corehole / 2
FEATURE [Part::Cylinder] Cylinder097
  Angle = 360
  AttacherType = Attacher::AttachEngine3D
  FirstAngle = 0
  Height = 2
  Placement = pos=(-15,0,0) rot=(0,0,1;0rad)
  Radius = 1.65
  SecondAngle = 0
  expr: .Placement.Base.x = <<BreadboardConfig>>.screw_spacing * -3
  expr: Height = <<BreadboardConfig>>.t_plate
  expr: Radius = <<BreadboardConfig>>.screw_corehole / 2
FEATURE [Part::Cylinder] Cylinder098
  Angle = 360
  AttacherType = Attacher::AttachEngine3D
  FirstAngle = 0
  Height = 2
  Placement = pos=(-20,0,0) rot=(0,0,1;0rad)
  Radius = 1.65
  SecondAngle = 0
  expr: .Placement.Base.x = <<BreadboardConfig>>.screw_spacing * -4
  expr: Height = <<BreadboardConfig>>.t_plate
  expr: Radius = <<BreadboardConfig>>.screw_corehole / 2
FEATURE [Part::Cylinder] Cylinder099
  Angle = 360
  AttacherType = Attacher::AttachEngine3D
  FirstAngle = 0
  Height = 2
  Placement = pos=(-25,0,0) rot=(0,0,1;0rad)
  Radius = 1.65
  SecondAngle = 0
  expr: .Placement.Base.x = <<BreadboardConfig>>.screw_spacing * -5
  expr: Height = <<BreadboardConfig>>.t_plate
  expr: Radius = <<BreadboardConfig>>.screw_corehole / 2
FEATURE [Part::Cylinder] Cylinder100
  Angle = 360
  AttacherType = Attacher::AttachEngine3D
  FirstAngle = 0
  Height = 2
  Placement = pos=(-30,0,0) rot=(0,0,1;0rad)
  Radius = 1.65
  SecondAngle = 0
  expr: .Placement.Base.x = <<BreadboardConfig>>.screw_spacing * -6
  expr: Height = <<BreadboardConfig>>.t_plate
  expr: Radius = <<BreadboardConfig>>.screw_corehole / 2
FEATURE [Part::Cylinder] Cylinder101
  Angle = 360
  AttacherType = Attacher::AttachEngine3D
  FirstAngle = 0
  Height = 2
  Placement = pos=(-35,0,0) rot=(0,0,1;0rad)
  Radius = 1.65
  SecondAngle = 0
  expr: .Placement.Base.x = <<BreadboardConfig>>.screw_spacing * -7
  expr: Height = <<BreadboardConfig>>.t_plate
  expr: Radius = <<BreadboardConfig>>.screw_corehole / 2
FEATURE [Part::Cylinder] Cylinder102
  Angle = 360
  AttacherType = Attacher::AttachEngine3D
  FirstAngle = 0
  Height = 2
  Placement = pos=(-40,0,0) rot=(0,0,1;0rad)
  Radius = 1.65
  SecondAngle = 0
  expr: .Placement.Base.x = <<BreadboardConfig>>.screw_spacing * -8
  expr: Height = <<BreadboardConfig>>.t_plate
  expr: Radius = <<BreadboardConfig>>.screw_corehole / 2
FEATURE [Part::Cylinder] Cylinder103
  Angle = 360
  AttacherType = Attacher::AttachEngine3D
  FirstAngle = 0
  Height = 2
  Placement = pos=(-45,0,0) rot=(0,0,1;0rad)
  Radius = 1.65
  SecondAngle = 0
  expr: .Placement.Base.x = <<BreadboardConfig>>.screw_spacing * -9
  expr: Height = <<BreadboardConfig>>.t_plate
  expr: Radius = <<BreadboardConfig>>.screw_corehole / 2
FEATURE [Part::Cylinder] Cylinder104
  Angle = 360
  AttacherType = Attacher::AttachEngine3D
  FirstAngle = 0
  Height = 2
  Placement = pos=(-50,0,0) rot=(0,0,1;0rad)
  Radius = 1.65
  SecondAngle = 0
  expr: .Placement.Base.x = <<BreadboardConfig>>.screw_spacing * -10
  expr: Height = <<BreadboardConfig>>.t_plate
  expr: Radius = <<BreadboardConfig>>.screw_corehole / 2
FEATURE [Part::Cylinder] Cylinder105
  Angle = 360
  AttacherType = Attacher::AttachEngine3D
  FirstAngle = 0
  Height = 2
  Radius = 1.65
  SecondAngle = 0
  expr: Height = <<BreadboardConfig>>.t_plate
  expr: Radius = <<BreadboardConfig>>.screw_corehole / 2
FEATURE [Part::MultiFuse] Fusion005
  Placement = pos=(0,20,0) rot=(0,0,1;0rad)
  Shapes = -> [Cylinder104,Cylinder103,Cylinder102,Cylinder101,Cylinder100,Cylinder099,Cylinder098,Cylinder097,Cylinder096,Cylinder095,Cylinder094,Cylinder093,Cylinder092,Cylinder091,Cylinder090,Cylinder089,Cylinder088,Cylinder087,Cylinder086,Cylinder085,Cylinder105]
  expr: .Placement.Base.y = <<BreadboardConfig>>.screw_spacing * 4
FEATURE [Part::Cylinder] Cylinder106
  Angle = 360
  AttacherType = Attacher::AttachEngine3D
  FirstAngle = 0
  Height = 2
  Placement = pos=(5,0,0) rot=(0,0,1;0rad)
  Radius = 1.65
  SecondAngle = 0
  expr: .Placement.Base.x = <<BreadboardConfig>>.screw_spacing * 1
  expr: Height = <<BreadboardConfig>>.t_plate
  expr: Radius = <<BreadboardConfig>>.screw_corehole / 2
FEATURE [Part::Cylinder] Cylinder107
  Angle = 360
  AttacherType = Attacher::AttachEngine3D
  FirstAngle = 0
  Height = 2
  Placement = pos=(10,0,0) rot=(0,0,1;0rad)
  Radius = 1.65
  SecondAngle = 0
  expr: .Placement.Base.x = <<BreadboardConfig>>.screw_spacing * 2
  expr: Height = <<BreadboardConfig>>.t_plate
  expr: Radius = <<BreadboardConfig>>.screw_corehole / 2
FEATURE [Part::Cylinder] Cylinder108
  Angle = 360
  AttacherType = Attacher::AttachEngine3D
  FirstAngle = 0
  Height = 2
  Placement = pos=(15,0,0) rot=(0,0,1;0rad)
  Radius = 1.65
  SecondAngle = 0
  expr: .Placement.Base.x = <<BreadboardConfig>>.screw_spacing * 3
  expr: Height = <<BreadboardConfig>>.t_plate
  expr: Radius = <<BreadboardConfig>>.screw_corehole / 2
FEATURE [Part::Cylinder] Cylinder109
  Angle = 360
  AttacherType = Attacher::AttachEngine3D
  FirstAngle = 0
  Height = 2
  Placement = pos=(20,0,0) rot=(0,0,1;0rad)
  Radius = 1.65
  SecondAngle = 0
  expr: .Placement.Base.x = <<BreadboardConfig>>.screw_spacing * 4
  expr: Height = <<BreadboardConfig>>.t_plate
  expr: Radius = <<BreadboardConfig>>.screw_corehole / 2
FEATURE [Part::Cylinder] Cylinder110
  Angle = 360
  AttacherType = Attacher::AttachEngine3D
  FirstAngle = 0
  Height = 2
  Placement = pos=(25,0,0) rot=(0,0,1;0rad)
  Radius = 1.65
  SecondAngle = 0
  expr: .Placement.Base.x = <<BreadboardConfig>>.screw_spacing * 5
  expr: Height = <<BreadboardConfig>>.t_plate
  expr: Radius = <<BreadboardConfig>>.screw_corehole / 2
FEATURE [Part::Cylinder] Cylinder111
  Angle = 360
  AttacherType = Attacher::AttachEngine3D
  FirstAngle = 0
  Height = 2
  Placement = pos=(30,0,0) rot=(0,0,1;0rad)
  Radius = 1.65
  SecondAngle = 0
  expr: .Placement.Base.x = <<BreadboardConfig>>.screw_spacing * 6
  expr: Height = <<BreadboardConfig>>.t_plate
  expr: Radius = <<BreadboardConfig>>.screw_corehole / 2
FEATURE [Part::Cylinder] Cylinder112
  Angle = 360
  AttacherType = Attacher::AttachEngine3D
  FirstAngle = 0
  Height = 2
  Placement = pos=(35,0,0) rot=(0,0,1;0rad)
  Radius = 1.65
  SecondAngle = 0
  expr: .Placement.Base.x = <<BreadboardConfig>>.screw_spacing * 7
  expr: Height = <<BreadboardConfig>>.t_plate
  expr: Radius = <<BreadboardConfig>>.screw_corehole / 2
FEATURE [Part::Cylinder] Cylinder113
  Angle = 360
  AttacherType = Attacher::AttachEngine3D
  FirstAngle = 0
  Height = 2
  Placement = pos=(40,0,0) rot=(0,0,1;0rad)
  Radius = 1.65
  SecondAngle = 0
  expr: .Placement.Base.x = <<BreadboardConfig>>.screw_spacing * 8
  expr: Height = <<BreadboardConfig>>.t_plate
  expr: Radius = <<BreadboardConfig>>.screw_corehole / 2
FEATURE [Part::Cylinder] Cylinder114
  Angle = 360
  AttacherType = Attacher::AttachEngine3D
  FirstAngle = 0
  Height = 2
  Placement = pos=(45,0,0) rot=(0,0,1;0rad)
  Radius = 1.65
  SecondAngle = 0
  expr: .Placement.Base.x = <<BreadboardConfig>>.screw_spacing * 9
  expr: Height = <<BreadboardConfig>>.t_plate
  expr: Radius = <<BreadboardConfig>>.screw_corehole / 2
FEATURE [Part::Cylinder] Cylinder115
  Angle = 360
  AttacherType = Attacher::AttachEngine3D
  FirstAngle = 0
  Height = 2
  Placement = pos=(50,0,0) rot=(0,0,1;0rad)
  Radius = 1.65
  SecondAngle = 0
  expr: .Placement.Base.x = <<BreadboardConfig>>.screw_spacing * 10
  expr: Height = <<BreadboardConfig>>.t_plate
  expr: Radius = <<BreadboardConfig>>.screw_corehole / 2
FEATURE [Part::Cylinder] Cylinder116
  Angle = 360
  AttacherType = Attacher::AttachEngine3D
  FirstAngle = 0
  Height = 2
  Placement = pos=(-5,0,0) rot=(0,0,1;0rad)
  Radius = 1.65
  SecondAngle = 0
  expr: .Placement.Base.x = <<BreadboardConfig>>.screw_spacing * -1
  expr: Height = <<BreadboardConfig>>.t_plate
  expr: Radius = <<BreadboardConfig>>.screw_corehole / 2
FEATURE [Part::Cylinder] Cylinder117
  Angle = 360
  AttacherType = Attacher::AttachEngine3D
  FirstAngle = 0
  Height = 2
  Placement = pos=(-10,0,0) rot=(0,0,1;0rad)
  Radius = 1.65
  SecondAngle = 0
  expr: .Placement.Base.x = <<BreadboardConfig>>.screw_spacing * -2
  expr: Height = <<BreadboardConfig>>.t_plate
  expr: Radius = <<BreadboardConfig>>.screw_corehole / 2
FEATURE [Part::Cylinder] Cylinder118
  Angle = 360
  AttacherType = Attacher::AttachEngine3D
  FirstAngle = 0
  Height = 2
  Placement = pos=(-15,0,0) rot=(0,0,1;0rad)
  Radius = 1.65
  SecondAngle = 0
  expr: .Placement.Base.x = <<BreadboardConfig>>.screw_spacing * -3
  expr: Height = <<BreadboardConfig>>.t_plate
  expr: Radius = <<BreadboardConfig>>.screw_corehole / 2
FEATURE [Part::Cylinder] Cylinder119
  Angle = 360
  AttacherType = Attacher::AttachEngine3D
  FirstAngle = 0
  Height = 2
  Placement = pos=(-20,0,0) rot=(0,0,1;0rad)
  Radius = 1.65
  SecondAngle = 0
  expr: .Placement.Base.x = <<BreadboardConfig>>.screw_spacing * -4
  expr: Height = <<BreadboardConfig>>.t_plate
  expr: Radius = <<BreadboardConfig>>.screw_corehole / 2
FEATURE [Part::Cylinder] Cylinder120
  Angle = 360
  AttacherType = Attacher::AttachEngine3D
  FirstAngle = 0
  Height = 2
  Placement = pos=(-25,0,0) rot=(0,0,1;0rad)
  Radius = 1.65
  SecondAngle = 0
  expr: .Placement.Base.x = <<BreadboardConfig>>.screw_spacing * -5
  expr: Height = <<BreadboardConfig>>.t_plate
  expr: Radius = <<BreadboardConfig>>.screw_corehole / 2
FEATURE [Part::Cylinder] Cylinder121
  Angle = 360
  AttacherType = Attacher::AttachEngine3D
  FirstAngle = 0
  Height = 2
  Placement = pos=(-30,0,0) rot=(0,0,1;0rad)
  Radius = 1.65
  SecondAngle = 0
  expr: .Placement.Base.x = <<BreadboardConfig>>.screw_spacing * -6
  expr: Height = <<BreadboardConfig>>.t_plate
  expr: Radius = <<BreadboardConfig>>.screw_corehole / 2
FEATURE [Part::Cylinder] Cylinder122
  Angle = 360
  AttacherType = Attacher::AttachEngine3D
  FirstAngle = 0
  Height = 2
  Placement = pos=(-35,0,0) rot=(0,0,1;0rad)
  Radius = 1.65
  SecondAngle = 0
  expr: .Placement.Base.x = <<BreadboardConfig>>.screw_spacing * -7
  expr: Height = <<BreadboardConfig>>.t_plate
  expr: Radius = <<BreadboardConfig>>.screw_corehole / 2
FEATURE [Part::Cylinder] Cylinder123
  Angle = 360
  AttacherType = Attacher::AttachEngine3D
  FirstAngle = 0
  Height = 2
  Placement = pos=(-40,0,0) rot=(0,0,1;0rad)
  Radius = 1.65
  SecondAngle = 0
  expr: .Placement.Base.x = <<BreadboardConfig>>.screw_spacing * -8
  expr: Height = <<BreadboardConfig>>.t_plate
  expr: Radius = <<BreadboardConfig>>.screw_corehole / 2
FEATURE [Part::Cylinder] Cylinder124
  Angle = 360
  AttacherType = Attacher::AttachEngine3D
  FirstAngle = 0
  Height = 2
  Placement = pos=(-45,0,0) rot=(0,0,1;0rad)
  Radius = 1.65
  SecondAngle = 0
  expr: .Placement.Base.x = <<BreadboardConfig>>.screw_spacing * -9
  expr: Height = <<BreadboardConfig>>.t_plate
  expr: Radius = <<BreadboardConfig>>.screw_corehole / 2
FEATURE [Part::Cylinder] Cylinder125
  Angle = 360
  AttacherType = Attacher::AttachEngine3D
  FirstAngle = 0
  Height = 2
  Placement = pos=(-50,0,0) rot=(0,0,1;0rad)
  Radius = 1.65
  SecondAngle = 0
  expr: .Placement.Base.x = <<BreadboardConfig>>.screw_spacing * -10
  expr: Height = <<BreadboardConfig>>.t_plate
  expr: Radius = <<BreadboardConfig>>.screw_corehole / 2
FEATURE [Part::Cylinder] Cylinder126
  Angle = 360
  AttacherType = Attacher::AttachEngine3D
  FirstAngle = 0
  Height = 2
  Radius = 1.65
  SecondAngle = 0
  expr: Height = <<BreadboardConfig>>.t_plate
  expr: Radius = <<BreadboardConfig>>.screw_corehole / 2
FEATURE [Part::MultiFuse] Fusion006
  Placement = pos=(0,25,0) rot=(0,0,1;0rad)
  Shapes = -> [Cylinder125,Cylinder124,Cylinder123,Cylinder122,Cylinder121,Cylinder120,Cylinder119,Cylinder118,Cylinder117,Cylinder116,Cylinder115,Cylinder114,Cylinder113,Cylinder112,Cylinder111,Cylinder110,Cylinder109,Cylinder108,Cylinder107,Cylinder106,Cylinder126]
  expr: .Placement.Base.y = <<BreadboardConfig>>.screw_spacing * 5
FEATURE [Part::Cylinder] Cylinder127
  Angle = 360
  AttacherType = Attacher::AttachEngine3D
  FirstAngle = 0
  Height = 2
  Placement = pos=(5,0,0) rot=(0,0,1;0rad)
  Radius = 1.65
  SecondAngle = 0
  expr: .Placement.Base.x = <<BreadboardConfig>>.screw_spacing * 1
  expr: Height = <<BreadboardConfig>>.t_plate
  expr: Radius = <<BreadboardConfig>>.screw_corehole / 2
FEATURE [Part::Cylinder] Cylinder128
  Angle = 360
  AttacherType = Attacher::AttachEngine3D
  FirstAngle = 0
  Height = 2
  Placement = pos=(10,0,0) rot=(0,0,1;0rad)
  Radius = 1.65
  SecondAngle = 0
  expr: .Placement.Base.x = <<BreadboardConfig>>.screw_spacing * 2
  expr: Height = <<BreadboardConfig>>.t_plate
  expr: Radius = <<BreadboardConfig>>.screw_corehole / 2
FEATURE [Part::Cylinder] Cylinder129
  Angle = 360
  AttacherType = Attacher::AttachEngine3D
  FirstAngle = 0
  Height = 2
  Placement = pos=(15,0,0) rot=(0,0,1;0rad)
  Radius = 1.65
  SecondAngle = 0
  expr: .Placement.Base.x = <<BreadboardConfig>>.screw_spacing * 3
  expr: Height = <<BreadboardConfig>>.t_plate
  expr: Radius = <<BreadboardConfig>>.screw_corehole / 2
FEATURE [Part::Cylinder] Cylinder130
  Angle = 360
  AttacherType = Attacher::AttachEngine3D
  FirstAngle = 0
  Height = 2
  Placement = pos=(20,0,0) rot=(0,0,1;0rad)
  Radius = 1.65
  SecondAngle = 0
  expr: .Placement.Base.x = <<BreadboardConfig>>.screw_spacing * 4
  expr: Height = <<BreadboardConfig>>.t_plate
  expr: Radius = <<BreadboardConfig>>.screw_corehole / 2
FEATURE [Part::Cylinder] Cylinder131
  Angle = 360
  AttacherType = Attacher::AttachEngine3D
  FirstAngle = 0
  Height = 2
  Placement = pos=(25,0,0) rot=(0,0,1;0rad)
  Radius = 1.65
  SecondAngle = 0
  expr: .Placement.Base.x = <<BreadboardConfig>>.screw_spacing * 5
  expr: Height = <<BreadboardConfig>>.t_plate
  expr: Radius = <<BreadboardConfig>>.screw_corehole / 2
FEATURE [Part::Cylinder] Cylinder132
  Angle = 360
  AttacherType = Attacher::AttachEngine3D
  FirstAngle = 0
  Height = 2
  Placement = pos=(30,0,0) rot=(0,0,1;0rad)
  Radius = 1.65
  SecondAngle = 0
  expr: .Placement.Base.x = <<BreadboardConfig>>.screw_spacing * 6
  expr: Height = <<BreadboardConfig>>.t_plate
  expr: Radius = <<BreadboardConfig>>.screw_corehole / 2
FEATURE [Part::Cylinder] Cylinder133
  Angle = 360
  AttacherType = Attacher::AttachEngine3D
  FirstAngle = 0
  Height = 2
  Placement = pos=(35,0,0) rot=(0,0,1;0rad)
  Radius = 1.65
  SecondAngle = 0
  expr: .Placement.Base.x = <<BreadboardConfig>>.screw_spacing * 7
  expr: Height = <<BreadboardConfig>>.t_plate
  expr: Radius = <<BreadboardConfig>>.screw_corehole / 2
FEATURE [Part::Cylinder] Cylinder134
  Angle = 360
  AttacherType = Attacher::AttachEngine3D
  FirstAngle = 0
  Height = 2
  Placement = pos=(40,0,0) rot=(0,0,1;0rad)
  Radius = 1.65
  SecondAngle = 0
  expr: .Placement.Base.x = <<BreadboardConfig>>.screw_spacing * 8
  expr: Height = <<BreadboardConfig>>.t_plate
  expr: Radius = <<BreadboardConfig>>.screw_corehole / 2
FEATURE [Part::Cylinder] Cylinder135
  Angle = 360
  AttacherType = Attacher::AttachEngine3D
  FirstAngle = 0
  Height = 2
  Placement = pos=(45,0,0) rot=(0,0,1;0rad)
  Radius = 1.65
  SecondAngle = 0
  expr: .Placement.Base.x = <<BreadboardConfig>>.screw_spacing * 9
  expr: Height = <<BreadboardConfig>>.t_plate
  expr: Radius = <<BreadboardConfig>>.screw_corehole / 2
FEATURE [Part::Cylinder] Cylinder136
  Angle = 360
  AttacherType = Attacher::AttachEngine3D
  FirstAngle = 0
  Height = 2
  Placement = pos=(50,0,0) rot=(0,0,1;0rad)
  Radius = 1.65
  SecondAngle = 0
  expr: .Placement.Base.x = <<BreadboardConfig>>.screw_spacing * 10
  expr: Height = <<BreadboardConfig>>.t_plate
  expr: Radius = <<BreadboardConfig>>.screw_corehole / 2
FEATURE [Part::Cylinder] Cylinder137
  Angle = 360
  AttacherType = Attacher::AttachEngine3D
  FirstAngle = 0
  Height = 2
  Placement = pos=(-5,0,0) rot=(0,0,1;0rad)
  Radius = 1.65
  SecondAngle = 0
  expr: .Placement.Base.x = <<BreadboardConfig>>.screw_spacing * -1
  expr: Height = <<BreadboardConfig>>.t_plate
  expr: Radius = <<BreadboardConfig>>.screw_corehole / 2
FEATURE [Part::Cylinder] Cylinder138
  Angle = 360
  AttacherType = Attacher::AttachEngine3D
  FirstAngle = 0
  Height = 2
  Placement = pos=(-10,0,0) rot=(0,0,1;0rad)
  Radius = 1.65
  SecondAngle = 0
  expr: .Placement.Base.x = <<BreadboardConfig>>.screw_spacing * -2
  expr: Height = <<BreadboardConfig>>.t_plate
  expr: Radius = <<BreadboardConfig>>.screw_corehole / 2
FEATURE [Part::Cylinder] Cylinder139
  Angle = 360
  AttacherType = Attacher::AttachEngine3D
  FirstAngle = 0
  Height = 2
  Placement = pos=(-15,0,0) rot=(0,0,1;0rad)
  Radius = 1.65
  SecondAngle = 0
  expr: .Placement.Base.x = <<BreadboardConfig>>.screw_spacing * -3
  expr: Height = <<BreadboardConfig>>.t_plate
  expr: Radius = <<BreadboardConfig>>.screw_corehole / 2
FEATURE [Part::Cylinder] Cylinder140
  Angle = 360
  AttacherType = Attacher::AttachEngine3D
  FirstAngle = 0
  Height = 2
  Placement = pos=(-20,0,0) rot=(0,0,1;0rad)
  Radius = 1.65
  SecondAngle = 0
  expr: .Placement.Base.x = <<BreadboardConfig>>.screw_spacing * -4
  expr: Height = <<BreadboardConfig>>.t_plate
  expr: Radius = <<BreadboardConfig>>.screw_corehole / 2
FEATURE [Part::Cylinder] Cylinder141
  Angle = 360
  AttacherType = Attacher::AttachEngine3D
  FirstAngle = 0
  Height = 2
  Placement = pos=(-25,0,0) rot=(0,0,1;0rad)
  Radius = 1.65
  SecondAngle = 0
  expr: .Placement.Base.x = <<BreadboardConfig>>.screw_spacing * -5
  expr: Height = <<BreadboardConfig>>.t_plate
  expr: Radius = <<BreadboardConfig>>.screw_corehole / 2
FEATURE [Part::Cylinder] Cylinder142
  Angle = 360
  AttacherType = Attacher::AttachEngine3D
  FirstAngle = 0
  Height = 2
  Placement = pos=(-30,0,0) rot=(0,0,1;0rad)
  Radius = 1.65
  SecondAngle = 0
  expr: .Placement.Base.x = <<BreadboardConfig>>.screw_spacing * -6
  expr: Height = <<BreadboardConfig>>.t_plate
  expr: Radius = <<BreadboardConfig>>.screw_corehole / 2
FEATURE [Part::Cylinder] Cylinder143
  Angle = 360
  AttacherType = Attacher::AttachEngine3D
  FirstAngle = 0
  Height = 2
  Placement = pos=(-35,0,0) rot=(0,0,1;0rad)
  Radius = 1.65
  SecondAngle = 0
  expr: .Placement.Base.x = <<BreadboardConfig>>.screw_spacing * -7
  expr: Height = <<BreadboardConfig>>.t_plate
  expr: Radius = <<BreadboardConfig>>.screw_corehole / 2
FEATURE [Part::Cylinder] Cylinder144
  Angle = 360
  AttacherType = Attacher::AttachEngine3D
  FirstAngle = 0
  Height = 2
  Placement = pos=(-40,0,0) rot=(0,0,1;0rad)
  Radius = 1.65
  SecondAngle = 0
  expr: .Placement.Base.x = <<BreadboardConfig>>.screw_spacing * -8
  expr: Height = <<BreadboardConfig>>.t_plate
  expr: Radius = <<BreadboardConfig>>.screw_corehole / 2
FEATURE [Part::Cylinder] Cylinder145
  Angle = 360
  AttacherType = Attacher::AttachEngine3D
  FirstAngle = 0
  Height = 2
  Placement = pos=(-45,0,0) rot=(0,0,1;0rad)
  Radius = 1.65
  SecondAngle = 0
  expr: .Placement.Base.x = <<BreadboardConfig>>.screw_spacing * -9
  expr: Height = <<BreadboardConfig>>.t_plate
  expr: Radius = <<BreadboardConfig>>.screw_corehole / 2
FEATURE [Part::Cylinder] Cylinder146
  Angle = 360
  AttacherType = Attacher::AttachEngine3D
  FirstAngle = 0
  Height = 2
  Placement = pos=(-50,0,0) rot=(0,0,1;0rad)
  Radius = 1.65
  SecondAngle = 0
  expr: .Placement.Base.x = <<BreadboardConfig>>.screw_spacing * -10
  expr: Height = <<BreadboardConfig>>.t_plate
  expr: Radius = <<BreadboardConfig>>.screw_corehole / 2
FEATURE [Part::Cylinder] Cylinder147
  Angle = 360
  AttacherType = Attacher::AttachEngine3D
  FirstAngle = 0
  Height = 2
  Radius = 1.65
  SecondAngle = 0
  expr: Height = <<BreadboardConfig>>.t_plate
  expr: Radius = <<BreadboardConfig>>.screw_corehole / 2
FEATURE [Part::MultiFuse] Fusion007
  Placement = pos=(0,30,0) rot=(0,0,1;0rad)
  Shapes = -> [Cylinder146,Cylinder145,Cylinder144,Cylinder143,Cylinder142,Cylinder141,Cylinder140,Cylinder139,Cylinder138,Cylinder137,Cylinder136,Cylinder135,Cylinder134,Cylinder133,Cylinder132,Cylinder131,Cylinder130,Cylinder129,Cylinder128,Cylinder127,Cylinder147]
  expr: .Placement.Base.y = <<BreadboardConfig>>.screw_spacing * 6
FEATURE [Part::Cylinder] Cylinder148
  Angle = 360
  AttacherType = Attacher::AttachEngine3D
  FirstAngle = 0
  Height = 2
  Placement = pos=(5,0,0) rot=(0,0,1;0rad)
  Radius = 1.65
  SecondAngle = 0
  expr: .Placement.Base.x = <<BreadboardConfig>>.screw_spacing * 1
  expr: Height = <<BreadboardConfig>>.t_plate
  expr: Radius = <<BreadboardConfig>>.screw_corehole / 2
FEATURE [Part::Cylinder] Cylinder149
  Angle = 360
  AttacherType = Attacher::AttachEngine3D
  FirstAngle = 0
  Height = 2
  Placement = pos=(10,0,0) rot=(0,0,1;0rad)
  Radius = 1.65
  SecondAngle = 0
  expr: .Placement.Base.x = <<BreadboardConfig>>.screw_spacing * 2
  expr: Height = <<BreadboardConfig>>.t_plate
  expr: Radius = <<BreadboardConfig>>.screw_corehole / 2
FEATURE [Part::Cylinder] Cylinder150
  Angle = 360
  AttacherType = Attacher::AttachEngine3D
  FirstAngle = 0
  Height = 2
  Placement = pos=(15,0,0) rot=(0,0,1;0rad)
  Radius = 1.65
  SecondAngle = 0
  expr: .Placement.Base.x = <<BreadboardConfig>>.screw_spacing * 3
  expr: Height = <<BreadboardConfig>>.t_plate
  expr: Radius = <<BreadboardConfig>>.screw_corehole / 2
FEATURE [Part::Cylinder] Cylinder151
  Angle = 360
  AttacherType = Attacher::AttachEngine3D
  FirstAngle = 0
  Height = 2
  Placement = pos=(20,0,0) rot=(0,0,1;0rad)
  Radius = 1.65
  SecondAngle = 0
  expr: .Placement.Base.x = <<BreadboardConfig>>.screw_spacing * 4
  expr: Height = <<BreadboardConfig>>.t_plate
  expr: Radius = <<BreadboardConfig>>.screw_corehole / 2
FEATURE [Part::Cylinder] Cylinder152
  Angle = 360
  AttacherType = Attacher::AttachEngine3D
  FirstAngle = 0
  Height = 2
  Placement = pos=(25,0,0) rot=(0,0,1;0rad)
  Radius = 1.65
  SecondAngle = 0
  expr: .Placement.Base.x = <<BreadboardConfig>>.screw_spacing * 5
  expr: Height = <<BreadboardConfig>>.t_plate
  expr: Radius = <<BreadboardConfig>>.screw_corehole / 2
FEATURE [Part::Cylinder] Cylinder153
  Angle = 360
  AttacherType = Attacher::AttachEngine3D
  FirstAngle = 0
  Height = 2
  Placement = pos=(30,0,0) rot=(0,0,1;0rad)
  Radius = 1.65
  SecondAngle = 0
  expr: .Placement.Base.x = <<BreadboardConfig>>.screw_spacing * 6
  expr: Height = <<BreadboardConfig>>.t_plate
  expr: Radius = <<BreadboardConfig>>.screw_corehole / 2
FEATURE [Part::Cylinder] Cylinder154
  Angle = 360
  AttacherType = Attacher::AttachEngine3D
  FirstAngle = 0
  Height = 2
  Placement = pos=(35,0,0) rot=(0,0,1;0rad)
  Radius = 1.65
  SecondAngle = 0
  expr: .Placement.Base.x = <<BreadboardConfig>>.screw_spacing * 7
  expr: Height = <<BreadboardConfig>>.t_plate
  expr: Radius = <<BreadboardConfig>>.screw_corehole / 2
FEATURE [Part::Cylinder] Cylinder155
  Angle = 360
  AttacherType = Attacher::AttachEngine3D
  FirstAngle = 0
  Height = 2
  Placement = pos=(40,0,0) rot=(0,0,1;0rad)
  Radius = 1.65
  SecondAngle = 0
  expr: .Placement.Base.x = <<BreadboardConfig>>.screw_spacing * 8
  expr: Height = <<BreadboardConfig>>.t_plate
  expr: Radius = <<BreadboardConfig>>.screw_corehole / 2
FEATURE [Part::Cylinder] Cylinder156
  Angle = 360
  AttacherType = Attacher::AttachEngine3D
  FirstAngle = 0
  Height = 2
  Placement = pos=(45,0,0) rot=(0,0,1;0rad)
  Radius = 1.65
  SecondAngle = 0
  expr: .Placement.Base.x = <<BreadboardConfig>>.screw_spacing * 9
  expr: Height = <<BreadboardConfig>>.t_plate
  expr: Radius = <<BreadboardConfig>>.screw_corehole / 2
FEATURE [Part::Cylinder] Cylinder157
  Angle = 360
  AttacherType = Attacher::AttachEngine3D
  FirstAngle = 0
  Height = 2
  Placement = pos=(50,0,0) rot=(0,0,1;0rad)
  Radius = 1.65
  SecondAngle = 0
  expr: .Placement.Base.x = <<BreadboardConfig>>.screw_spacing * 10
  expr: Height = <<BreadboardConfig>>.t_plate
  expr: Radius = <<BreadboardConfig>>.screw_corehole / 2
FEATURE [Part::Cylinder] Cylinder158
  Angle = 360
  AttacherType = Attacher::AttachEngine3D
  FirstAngle = 0
  Height = 2
  Placement = pos=(-5,0,0) rot=(0,0,1;0rad)
  Radius = 1.65
  SecondAngle = 0
  expr: .Placement.Base.x = <<BreadboardConfig>>.screw_spacing * -1
  expr: Height = <<BreadboardConfig>>.t_plate
  expr: Radius = <<BreadboardConfig>>.screw_corehole / 2
FEATURE [Part::Cylinder] Cylinder159
  Angle = 360
  AttacherType = Attacher::AttachEngine3D
  FirstAngle = 0
  Height = 2
  Placement = pos=(-10,0,0) rot=(0,0,1;0rad)
  Radius = 1.65
  SecondAngle = 0
  expr: .Placement.Base.x = <<BreadboardConfig>>.screw_spacing * -2
  expr: Height = <<BreadboardConfig>>.t_plate
  expr: Radius = <<BreadboardConfig>>.screw_corehole / 2
FEATURE [Part::Cylinder] Cylinder160
  Angle = 360
  AttacherType = Attacher::AttachEngine3D
  FirstAngle = 0
  Height = 2
  Placement = pos=(-15,0,0) rot=(0,0,1;0rad)
  Radius = 1.65
  SecondAngle = 0
  expr: .Placement.Base.x = <<BreadboardConfig>>.screw_spacing * -3
  expr: Height = <<BreadboardConfig>>.t_plate
  expr: Radius = <<BreadboardConfig>>.screw_corehole / 2
FEATURE [Part::Cylinder] Cylinder161
  Angle = 360
  AttacherType = Attacher::AttachEngine3D
  FirstAngle = 0
  Height = 2
  Placement = pos=(-20,0,0) rot=(0,0,1;0rad)
  Radius = 1.65
  SecondAngle = 0
  expr: .Placement.Base.x = <<BreadboardConfig>>.screw_spacing * -4
  expr: Height = <<BreadboardConfig>>.t_plate
  expr: Radius = <<BreadboardConfig>>.screw_corehole / 2
FEATURE [Part::Cylinder] Cylinder162
  Angle = 360
  AttacherType = Attacher::AttachEngine3D
  FirstAngle = 0
  Height = 2
  Placement = pos=(-25,0,0) rot=(0,0,1;0rad)
  Radius = 1.65
  SecondAngle = 0
  expr: .Placement.Base.x = <<BreadboardConfig>>.screw_spacing * -5
  expr: Height = <<BreadboardConfig>>.t_plate
  expr: Radius = <<BreadboardConfig>>.screw_corehole / 2
FEATURE [Part::Cylinder] Cylinder163
  Angle = 360
  AttacherType = Attacher::AttachEngine3D
  FirstAngle = 0
  Height = 2
  Placement = pos=(-30,0,0) rot=(0,0,1;0rad)
  Radius = 1.65
  SecondAngle = 0
  expr: .Placement.Base.x = <<BreadboardConfig>>.screw_spacing * -6
  expr: Height = <<BreadboardConfig>>.t_plate
  expr: Radius = <<BreadboardConfig>>.screw_corehole / 2
FEATURE [Part::Cylinder] Cylinder164
  Angle = 360
  AttacherType = Attacher::AttachEngine3D
  FirstAngle = 0
  Height = 2
  Placement = pos=(-35,0,0) rot=(0,0,1;0rad)
  Radius = 1.65
  SecondAngle = 0
  expr: .Placement.Base.x = <<BreadboardConfig>>.screw_spacing * -7
  expr: Height = <<BreadboardConfig>>.t_plate
  expr: Radius = <<BreadboardConfig>>.screw_corehole / 2
FEATURE [Part::Cylinder] Cylinder165
  Angle = 360
  AttacherType = Attacher::AttachEngine3D
  FirstAngle = 0
  Height = 2
  Placement = pos=(-40,0,0) rot=(0,0,1;0rad)
  Radius = 1.65
  SecondAngle = 0
  expr: .Placement.Base.x = <<BreadboardConfig>>.screw_spacing * -8
  expr: Height = <<BreadboardConfig>>.t_plate
  expr: Radius = <<BreadboardConfig>>.screw_corehole / 2
FEATURE [Part::Cylinder] Cylinder166
  Angle = 360
  AttacherType = Attacher::AttachEngine3D
  FirstAngle = 0
  Height = 2
  Placement = pos=(-45,0,0) rot=(0,0,1;0rad)
  Radius = 1.65
  SecondAngle = 0
  expr: .Placement.Base.x = <<BreadboardConfig>>.screw_spacing * -9
  expr: Height = <<BreadboardConfig>>.t_plate
  expr: Radius = <<BreadboardConfig>>.screw_corehole / 2
FEATURE [Part::Cylinder] Cylinder167
  Angle = 360
  AttacherType = Attacher::AttachEngine3D
  FirstAngle = 0
  Height = 2
  Placement = pos=(-50,0,0) rot=(0,0,1;0rad)
  Radius = 1.65
  SecondAngle = 0
  expr: .Placement.Base.x = <<BreadboardConfig>>.screw_spacing * -10
  expr: Height = <<BreadboardConfig>>.t_plate
  expr: Radius = <<BreadboardConfig>>.screw_corehole / 2
FEATURE [Part::Cylinder] Cylinder168
  Angle = 360
  AttacherType = Attacher::AttachEngine3D
  FirstAngle = 0
  Height = 2
  Radius = 1.65
  SecondAngle = 0
  expr: Height = <<BreadboardConfig>>.t_plate
  expr: Radius = <<BreadboardConfig>>.screw_corehole / 2
FEATURE [Part::MultiFuse] Fusion008
  Placement = pos=(0,35,0) rot=(0,0,1;0rad)
  Shapes = -> [Cylinder167,Cylinder166,Cylinder165,Cylinder164,Cylinder163,Cylinder162,Cylinder161,Cylinder160,Cylinder159,Cylinder158,Cylinder157,Cylinder156,Cylinder155,Cylinder154,Cylinder153,Cylinder152,Cylinder151,Cylinder150,Cylinder149,Cylinder148,Cylinder168]
  expr: .Placement.Base.y = <<BreadboardConfig>>.screw_spacing * 7
FEATURE [Part::Cylinder] Cylinder169
  Angle = 360
  AttacherType = Attacher::AttachEngine3D
  FirstAngle = 0
  Height = 2
  Placement = pos=(5,0,0) rot=(0,0,1;0rad)
  Radius = 1.65
  SecondAngle = 0
  expr: .Placement.Base.x = <<BreadboardConfig>>.screw_spacing * 1
  expr: Height = <<BreadboardConfig>>.t_plate
  expr: Radius = <<BreadboardConfig>>.screw_corehole / 2
FEATURE [Part::Cylinder] Cylinder170
  Angle = 360
  AttacherType = Attacher::AttachEngine3D
  FirstAngle = 0
  Height = 2
  Placement = pos=(10,0,0) rot=(0,0,1;0rad)
  Radius = 1.65
  SecondAngle = 0
  expr: .Placement.Base.x = <<BreadboardConfig>>.screw_spacing * 2
  expr: Height = <<BreadboardConfig>>.t_plate
  expr: Radius = <<BreadboardConfig>>.screw_corehole / 2
FEATURE [Part::Cylinder] Cylinder171
  Angle = 360
  AttacherType = Attacher::AttachEngine3D
  FirstAngle = 0
  Height = 2
  Placement = pos=(15,0,0) rot=(0,0,1;0rad)
  Radius = 1.65
  SecondAngle = 0
  expr: .Placement.Base.x = <<BreadboardConfig>>.screw_spacing * 3
  expr: Height = <<BreadboardConfig>>.t_plate
  expr: Radius = <<BreadboardConfig>>.screw_corehole / 2
FEATURE [Part::Cylinder] Cylinder172
  Angle = 360
  AttacherType = Attacher::AttachEngine3D
  FirstAngle = 0
  Height = 2
  Placement = pos=(20,0,0) rot=(0,0,1;0rad)
  Radius = 1.65
  SecondAngle = 0
  expr: .Placement.Base.x = <<BreadboardConfig>>.screw_spacing * 4
  expr: Height = <<BreadboardConfig>>.t_plate
  expr: Radius = <<BreadboardConfig>>.screw_corehole / 2
FEATURE [Part::Cylinder] Cylinder173
  Angle = 360
  AttacherType = Attacher::AttachEngine3D
  FirstAngle = 0
  Height = 2
  Placement = pos=(25,0,0) rot=(0,0,1;0rad)
  Radius = 1.65
  SecondAngle = 0
  expr: .Placement.Base.x = <<BreadboardConfig>>.screw_spacing * 5
  expr: Height = <<BreadboardConfig>>.t_plate
  expr: Radius = <<BreadboardConfig>>.screw_corehole / 2
FEATURE [Part::Cylinder] Cylinder174
  Angle = 360
  AttacherType = Attacher::AttachEngine3D
  FirstAngle = 0
  Height = 2
  Placement = pos=(30,0,0) rot=(0,0,1;0rad)
  Radius = 1.65
  SecondAngle = 0
  expr: .Placement.Base.x = <<BreadboardConfig>>.screw_spacing * 6
  expr: Height = <<BreadboardConfig>>.t_plate
  expr: Radius = <<BreadboardConfig>>.screw_corehole / 2
FEATURE [Part::Cylinder] Cylinder175
  Angle = 360
  AttacherType = Attacher::AttachEngine3D
  FirstAngle = 0
  Height = 2
  Placement = pos=(35,0,0) rot=(0,0,1;0rad)
  Radius = 1.65
  SecondAngle = 0
  expr: .Placement.Base.x = <<BreadboardConfig>>.screw_spacing * 7
  expr: Height = <<BreadboardConfig>>.t_plate
  expr: Radius = <<BreadboardConfig>>.screw_corehole / 2
FEATURE [Part::Cylinder] Cylinder176
  Angle = 360
  AttacherType = Attacher::AttachEngine3D
  FirstAngle = 0
  Height = 2
  Placement = pos=(40,0,0) rot=(0,0,1;0rad)
  Radius = 1.65
  SecondAngle = 0
  expr: .Placement.Base.x = <<BreadboardConfig>>.screw_spacing * 8
  expr: Height = <<BreadboardConfig>>.t_plate
  expr: Radius = <<BreadboardConfig>>.screw_corehole / 2
FEATURE [Part::Cylinder] Cylinder177
  Angle = 360
  AttacherType = Attacher::AttachEngine3D
  FirstAngle = 0
  Height = 2
  Placement = pos=(45,0,0) rot=(0,0,1;0rad)
  Radius = 1.65
  SecondAngle = 0
  expr: .Placement.Base.x = <<BreadboardConfig>>.screw_spacing * 9
  expr: Height = <<BreadboardConfig>>.t_plate
  expr: Radius = <<BreadboardConfig>>.screw_corehole / 2
FEATURE [Part::Cylinder] Cylinder178
  Angle = 360
  AttacherType = Attacher::AttachEngine3D
  FirstAngle = 0
  Height = 2
  Placement = pos=(50,0,0) rot=(0,0,1;0rad)
  Radius = 1.65
  SecondAngle = 0
  expr: .Placement.Base.x = <<BreadboardConfig>>.screw_spacing * 10
  expr: Height = <<BreadboardConfig>>.t_plate
  expr: Radius = <<BreadboardConfig>>.screw_corehole / 2
FEATURE [Part::Cylinder] Cylinder179
  Angle = 360
  AttacherType = Attacher::AttachEngine3D
  FirstAngle = 0
  Height = 2
  Placement = pos=(-5,0,0) rot=(0,0,1;0rad)
  Radius = 1.65
  SecondAngle = 0
  expr: .Placement.Base.x = <<BreadboardConfig>>.screw_spacing * -1
  expr: Height = <<BreadboardConfig>>.t_plate
  expr: Radius = <<BreadboardConfig>>.screw_corehole / 2
FEATURE [Part::Cylinder] Cylinder180
  Angle = 360
  AttacherType = Attacher::AttachEngine3D
  FirstAngle = 0
  Height = 2
  Placement = pos=(-10,0,0) rot=(0,0,1;0rad)
  Radius = 1.65
  SecondAngle = 0
  expr: .Placement.Base.x = <<BreadboardConfig>>.screw_spacing * -2
  expr: Height = <<BreadboardConfig>>.t_plate
  expr: Radius = <<BreadboardConfig>>.screw_corehole / 2
FEATURE [Part::Cylinder] Cylinder181
  Angle = 360
  AttacherType = Attacher::AttachEngine3D
  FirstAngle = 0
  Height = 2
  Placement = pos=(-15,0,0) rot=(0,0,1;0rad)
  Radius = 1.65
  SecondAngle = 0
  expr: .Placement.Base.x = <<BreadboardConfig>>.screw_spacing * -3
  expr: Height = <<BreadboardConfig>>.t_plate
  expr: Radius = <<BreadboardConfig>>.screw_corehole / 2
FEATURE [Part::Cylinder] Cylinder182
  Angle = 360
  AttacherType = Attacher::AttachEngine3D
  FirstAngle = 0
  Height = 2
  Placement = pos=(-20,0,0) rot=(0,0,1;0rad)
  Radius = 1.65
  SecondAngle = 0
  expr: .Placement.Base.x = <<BreadboardConfig>>.screw_spacing * -4
  expr: Height = <<BreadboardConfig>>.t_plate
  expr: Radius = <<BreadboardConfig>>.screw_corehole / 2
FEATURE [Part::Cylinder] Cylinder183
  Angle = 360
  AttacherType = Attacher::AttachEngine3D
  FirstAngle = 0
  Height = 2
  Placement = pos=(-25,0,0) rot=(0,0,1;0rad)
  Radius = 1.65
  SecondAngle = 0
  expr: .Placement.Base.x = <<BreadboardConfig>>.screw_spacing * -5
  expr: Height = <<BreadboardConfig>>.t_plate
  expr: Radius = <<BreadboardConfig>>.screw_corehole / 2
FEATURE [Part::Cylinder] Cylinder184
  Angle = 360
  AttacherType = Attacher::AttachEngine3D
  FirstAngle = 0
  Height = 2
  Placement = pos=(-30,0,0) rot=(0,0,1;0rad)
  Radius = 1.65
  SecondAngle = 0
  expr: .Placement.Base.x = <<BreadboardConfig>>.screw_spacing * -6
  expr: Height = <<BreadboardConfig>>.t_plate
  expr: Radius = <<BreadboardConfig>>.screw_corehole / 2
FEATURE [Part::Cylinder] Cylinder185
  Angle = 360
  AttacherType = Attacher::AttachEngine3D
  FirstAngle = 0
  Height = 2
  Placement = pos=(-35,0,0) rot=(0,0,1;0rad)
  Radius = 1.65
  SecondAngle = 0
  expr: .Placement.Base.x = <<BreadboardConfig>>.screw_spacing * -7
  expr: Height = <<BreadboardConfig>>.t_plate
  expr: Radius = <<BreadboardConfig>>.screw_corehole / 2
FEATURE [Part::Cylinder] Cylinder186
  Angle = 360
  AttacherType = Attacher::AttachEngine3D
  FirstAngle = 0
  Height = 2
  Placement = pos=(-40,0,0) rot=(0,0,1;0rad)
  Radius = 1.65
  SecondAngle = 0
  expr: .Placement.Base.x = <<BreadboardConfig>>.screw_spacing * -8
  expr: Height = <<BreadboardConfig>>.t_plate
  expr: Radius = <<BreadboardConfig>>.screw_corehole / 2
FEATURE [Part::Cylinder] Cylinder187
  Angle = 360
  AttacherType = Attacher::AttachEngine3D
  FirstAngle = 0
  Height = 2
  Placement = pos=(-45,0,0) rot=(0,0,1;0rad)
  Radius = 1.65
  SecondAngle = 0
  expr: .Placement.Base.x = <<BreadboardConfig>>.screw_spacing * -9
  expr: Height = <<BreadboardConfig>>.t_plate
  expr: Radius = <<BreadboardConfig>>.screw_corehole / 2
FEATURE [Part::Cylinder] Cylinder188
  Angle = 360
  AttacherType = Attacher::AttachEngine3D
  FirstAngle = 0
  Height = 2
  Placement = pos=(-50,0,0) rot=(0,0,1;0rad)
  Radius = 1.65
  SecondAngle = 0
  expr: .Placement.Base.x = <<BreadboardConfig>>.screw_spacing * -10
  expr: Height = <<BreadboardConfig>>.t_plate
  expr: Radius = <<BreadboardConfig>>.screw_corehole / 2
FEATURE [Part::Cylinder] Cylinder189
  Angle = 360
  AttacherType = Attacher::AttachEngine3D
  FirstAngle = 0
  Height = 2
  Radius = 1.65
  SecondAngle = 0
  expr: Height = <<BreadboardConfig>>.t_plate
  expr: Radius = <<BreadboardConfig>>.screw_corehole / 2
FEATURE [Part::MultiFuse] Fusion009
  Placement = pos=(0,40,0) rot=(0,0,1;0rad)
  Shapes = -> [Cylinder188,Cylinder187,Cylinder186,Cylinder185,Cylinder184,Cylinder183,Cylinder182,Cylinder181,Cylinder180,Cylinder179,Cylinder178,Cylinder177,Cylinder176,Cylinder175,Cylinder174,Cylinder173,Cylinder172,Cylinder171,Cylinder170,Cylinder169,Cylinder189]
  expr: .Placement.Base.y = <<BreadboardConfig>>.screw_spacing * 8
FEATURE [Part::Cylinder] Cylinder190
  Angle = 360
  AttacherType = Attacher::AttachEngine3D
  FirstAngle = 0
  Height = 2
  Placement = pos=(5,0,0) rot=(0,0,1;0rad)
  Radius = 1.65
  SecondAngle = 0
  expr: .Placement.Base.x = <<BreadboardConfig>>.screw_spacing * 1
  expr: Height = <<BreadboardConfig>>.t_plate
  expr: Radius = <<BreadboardConfig>>.screw_corehole / 2
FEATURE [Part::Cylinder] Cylinder191
  Angle = 360
  AttacherType = Attacher::AttachEngine3D
  FirstAngle = 0
  Height = 2
  Placement = pos=(10,0,0) rot=(0,0,1;0rad)
  Radius = 1.65
  SecondAngle = 0
  expr: .Placement.Base.x = <<BreadboardConfig>>.screw_spacing * 2
  expr: Height = <<BreadboardConfig>>.t_plate
  expr: Radius = <<BreadboardConfig>>.screw_corehole / 2
FEATURE [Part::Cylinder] Cylinder192
  Angle = 360
  AttacherType = Attacher::AttachEngine3D
  FirstAngle = 0
  Height = 2
  Placement = pos=(15,0,0) rot=(0,0,1;0rad)
  Radius = 1.65
  SecondAngle = 0
  expr: .Placement.Base.x = <<BreadboardConfig>>.screw_spacing * 3
  expr: Height = <<BreadboardConfig>>.t_plate
  expr: Radius = <<BreadboardConfig>>.screw_corehole / 2
FEATURE [Part::Cylinder] Cylinder193
  Angle = 360
  AttacherType = Attacher::AttachEngine3D
  FirstAngle = 0
  Height = 2
  Placement = pos=(20,0,0) rot=(0,0,1;0rad)
  Radius = 1.65
  SecondAngle = 0
  expr: .Placement.Base.x = <<BreadboardConfig>>.screw_spacing * 4
  expr: Height = <<BreadboardConfig>>.t_plate
  expr: Radius = <<BreadboardConfig>>.screw_corehole / 2
FEATURE [Part::Cylinder] Cylinder194
  Angle = 360
  AttacherType = Attacher::AttachEngine3D
  FirstAngle = 0
  Height = 2
  Placement = pos=(25,0,0) rot=(0,0,1;0rad)
  Radius = 1.65
  SecondAngle = 0
  expr: .Placement.Base.x = <<BreadboardConfig>>.screw_spacing * 5
  expr: Height = <<BreadboardConfig>>.t_plate
  expr: Radius = <<BreadboardConfig>>.screw_corehole / 2
FEATURE [Part::Cylinder] Cylinder195
  Angle = 360
  AttacherType = Attacher::AttachEngine3D
  FirstAngle = 0
  Height = 2
  Placement = pos=(30,0,0) rot=(0,0,1;0rad)
  Radius = 1.65
  SecondAngle = 0
  expr: .Placement.Base.x = <<BreadboardConfig>>.screw_spacing * 6
  expr: Height = <<BreadboardConfig>>.t_plate
  expr: Radius = <<BreadboardConfig>>.screw_corehole / 2
FEATURE [Part::Cylinder] Cylinder196
  Angle = 360
  AttacherType = Attacher::AttachEngine3D
  FirstAngle = 0
  Height = 2
  Placement = pos=(35,0,0) rot=(0,0,1;0rad)
  Radius = 1.65
  SecondAngle = 0
  expr: .Placement.Base.x = <<BreadboardConfig>>.screw_spacing * 7
  expr: Height = <<BreadboardConfig>>.t_plate
  expr: Radius = <<BreadboardConfig>>.screw_corehole / 2
FEATURE [Part::Cylinder] Cylinder197
  Angle = 360
  AttacherType = Attacher::AttachEngine3D
  FirstAngle = 0
  Height = 2
  Placement = pos=(40,0,0) rot=(0,0,1;0rad)
  Radius = 1.65
  SecondAngle = 0
  expr: .Placement.Base.x = <<BreadboardConfig>>.screw_spacing * 8
  expr: Height = <<BreadboardConfig>>.t_plate
  expr: Radius = <<BreadboardConfig>>.screw_corehole / 2
FEATURE [Part::Cylinder] Cylinder198
  Angle = 360
  AttacherType = Attacher::AttachEngine3D
  FirstAngle = 0
  Height = 2
  Placement = pos=(45,0,0) rot=(0,0,1;0rad)
  Radius = 1.65
  SecondAngle = 0
  expr: .Placement.Base.x = <<BreadboardConfig>>.screw_spacing * 9
  expr: Height = <<BreadboardConfig>>.t_plate
  expr: Radius = <<BreadboardConfig>>.screw_corehole / 2
FEATURE [Part::Cylinder] Cylinder199
  Angle = 360
  AttacherType = Attacher::AttachEngine3D
  FirstAngle = 0
  Height = 2
  Placement = pos=(50,0,0) rot=(0,0,1;0rad)
  Radius = 1.65
  SecondAngle = 0
  expr: .Placement.Base.x = <<BreadboardConfig>>.screw_spacing * 10
  expr: Height = <<BreadboardConfig>>.t_plate
  expr: Radius = <<BreadboardConfig>>.screw_corehole / 2
FEATURE [Part::Cylinder] Cylinder200
  Angle = 360
  AttacherType = Attacher::AttachEngine3D
  FirstAngle = 0
  Height = 2
  Placement = pos=(-5,0,0) rot=(0,0,1;0rad)
  Radius = 1.65
  SecondAngle = 0
  expr: .Placement.Base.x = <<BreadboardConfig>>.screw_spacing * -1
  expr: Height = <<BreadboardConfig>>.t_plate
  expr: Radius = <<BreadboardConfig>>.screw_corehole / 2
FEATURE [Part::Cylinder] Cylinder201
  Angle = 360
  AttacherType = Attacher::AttachEngine3D
  FirstAngle = 0
  Height = 2
  Placement = pos=(-10,0,0) rot=(0,0,1;0rad)
  Radius = 1.65
  SecondAngle = 0
  expr: .Placement.Base.x = <<BreadboardConfig>>.screw_spacing * -2
  expr: Height = <<BreadboardConfig>>.t_plate
  expr: Radius = <<BreadboardConfig>>.screw_corehole / 2
FEATURE [Part::Cylinder] Cylinder202
  Angle = 360
  AttacherType = Attacher::AttachEngine3D
  FirstAngle = 0
  Height = 2
  Placement = pos=(-15,0,0) rot=(0,0,1;0rad)
  Radius = 1.65
  SecondAngle = 0
  expr: .Placement.Base.x = <<BreadboardConfig>>.screw_spacing * -3
  expr: Height = <<BreadboardConfig>>.t_plate
  expr: Radius = <<BreadboardConfig>>.screw_corehole / 2
FEATURE [Part::Cylinder] Cylinder203
  Angle = 360
  AttacherType = Attacher::AttachEngine3D
  FirstAngle = 0
  Height = 2
  Placement = pos=(-20,0,0) rot=(0,0,1;0rad)
  Radius = 1.65
  SecondAngle = 0
  expr: .Placement.Base.x = <<BreadboardConfig>>.screw_spacing * -4
  expr: Height = <<BreadboardConfig>>.t_plate
  expr: Radius = <<BreadboardConfig>>.screw_corehole / 2
FEATURE [Part::Cylinder] Cylinder204
  Angle = 360
  AttacherType = Attacher::AttachEngine3D
  FirstAngle = 0
  Height = 2
  Placement = pos=(-25,0,0) rot=(0,0,1;0rad)
  Radius = 1.65
  SecondAngle = 0
  expr: .Placement.Base.x = <<BreadboardConfig>>.screw_spacing * -5
  expr: Height = <<BreadboardConfig>>.t_plate
  expr: Radius = <<BreadboardConfig>>.screw_corehole / 2
FEATURE [Part::Cylinder] Cylinder205
  Angle = 360
  AttacherType = Attacher::AttachEngine3D
  FirstAngle = 0
  Height = 2
  Placement = pos=(-30,0,0) rot=(0,0,1;0rad)
  Radius = 1.65
  SecondAngle = 0
  expr: .Placement.Base.x = <<BreadboardConfig>>.screw_spacing * -6
  expr: Height = <<BreadboardConfig>>.t_plate
  expr: Radius = <<BreadboardConfig>>.screw_corehole / 2
FEATURE [Part::Cylinder] Cylinder206
  Angle = 360
  AttacherType = Attacher::AttachEngine3D
  FirstAngle = 0
  Height = 2
  Placement = pos=(-35,0,0) rot=(0,0,1;0rad)
  Radius = 1.65
  SecondAngle = 0
  expr: .Placement.Base.x = <<BreadboardConfig>>.screw_spacing * -7
  expr: Height = <<BreadboardConfig>>.t_plate
  expr: Radius = <<BreadboardConfig>>.screw_corehole / 2
FEATURE [Part::Cylinder] Cylinder207
  Angle = 360
  AttacherType = Attacher::AttachEngine3D
  FirstAngle = 0
  Height = 2
  Placement = pos=(-40,0,0) rot=(0,0,1;0rad)
  Radius = 1.65
  SecondAngle = 0
  expr: .Placement.Base.x = <<BreadboardConfig>>.screw_spacing * -8
  expr: Height = <<BreadboardConfig>>.t_plate
  expr: Radius = <<BreadboardConfig>>.screw_corehole / 2
FEATURE [Part::Cylinder] Cylinder208
  Angle = 360
  AttacherType = Attacher::AttachEngine3D
  FirstAngle = 0
  Height = 2
  Placement = pos=(-45,0,0) rot=(0,0,1;0rad)
  Radius = 1.65
  SecondAngle = 0
  expr: .Placement.Base.x = <<BreadboardConfig>>.screw_spacing * -9
  expr: Height = <<BreadboardConfig>>.t_plate
  expr: Radius = <<BreadboardConfig>>.screw_corehole / 2
FEATURE [Part::Cylinder] Cylinder209
  Angle = 360
  AttacherType = Attacher::AttachEngine3D
  FirstAngle = 0
  Height = 2
  Placement = pos=(-50,0,0) rot=(0,0,1;0rad)
  Radius = 1.65
  SecondAngle = 0
  expr: .Placement.Base.x = <<BreadboardConfig>>.screw_spacing * -10
  expr: Height = <<BreadboardConfig>>.t_plate
  expr: Radius = <<BreadboardConfig>>.screw_corehole / 2
FEATURE [Part::Cylinder] Cylinder210
  Angle = 360
  AttacherType = Attacher::AttachEngine3D
  FirstAngle = 0
  Height = 2
  Radius = 1.65
  SecondAngle = 0
  expr: Height = <<BreadboardConfig>>.t_plate
  expr: Radius = <<BreadboardConfig>>.screw_corehole / 2
FEATURE [Part::MultiFuse] Fusion010
  Placement = pos=(0,45,0) rot=(0,0,1;0rad)
  Shapes = -> [Cylinder209,Cylinder208,Cylinder207,Cylinder206,Cylinder205,Cylinder204,Cylinder203,Cylinder202,Cylinder201,Cylinder200,Cylinder199,Cylinder198,Cylinder197,Cylinder196,Cylinder195,Cylinder194,Cylinder193,Cylinder192,Cylinder191,Cylinder190,Cylinder210]
  expr: .Placement.Base.y = <<BreadboardConfig>>.screw_spacing * 9
FEATURE [Part::Cylinder] Cylinder211
  Angle = 360
  AttacherType = Attacher::AttachEngine3D
  FirstAngle = 0
  Height = 2
  Placement = pos=(5,0,0) rot=(0,0,1;0rad)
  Radius = 1.65
  SecondAngle = 0
  expr: .Placement.Base.x = <<BreadboardConfig>>.screw_spacing * 1
  expr: Height = <<BreadboardConfig>>.t_plate
  expr: Radius = <<BreadboardConfig>>.screw_corehole / 2
FEATURE [Part::Cylinder] Cylinder212
  Angle = 360
  AttacherType = Attacher::AttachEngine3D
  FirstAngle = 0
  Height = 2
  Placement = pos=(10,0,0) rot=(0,0,1;0rad)
  Radius = 1.65
  SecondAngle = 0
  expr: .Placement.Base.x = <<BreadboardConfig>>.screw_spacing * 2
  expr: Height = <<BreadboardConfig>>.t_plate
  expr: Radius = <<BreadboardConfig>>.screw_corehole / 2
FEATURE [Part::Cylinder] Cylinder213
  Angle = 360
  AttacherType = Attacher::AttachEngine3D
  FirstAngle = 0
  Height = 2
  Placement = pos=(15,0,0) rot=(0,0,1;0rad)
  Radius = 1.65
  SecondAngle = 0
  expr: .Placement.Base.x = <<BreadboardConfig>>.screw_spacing * 3
  expr: Height = <<BreadboardConfig>>.t_plate
  expr: Radius = <<BreadboardConfig>>.screw_corehole / 2
FEATURE [Part::Cylinder] Cylinder214
  Angle = 360
  AttacherType = Attacher::AttachEngine3D
  FirstAngle = 0
  Height = 2
  Placement = pos=(20,0,0) rot=(0,0,1;0rad)
  Radius = 1.65
  SecondAngle = 0
  expr: .Placement.Base.x = <<BreadboardConfig>>.screw_spacing * 4
  expr: Height = <<BreadboardConfig>>.t_plate
  expr: Radius = <<BreadboardConfig>>.screw_corehole / 2
FEATURE [Part::Cylinder] Cylinder215
  Angle = 360
  AttacherType = Attacher::AttachEngine3D
  FirstAngle = 0
  Height = 2
  Placement = pos=(25,0,0) rot=(0,0,1;0rad)
  Radius = 1.65
  SecondAngle = 0
  expr: .Placement.Base.x = <<BreadboardConfig>>.screw_spacing * 5
  expr: Height = <<BreadboardConfig>>.t_plate
  expr: Radius = <<BreadboardConfig>>.screw_corehole / 2
FEATURE [Part::Cylinder] Cylinder216
  Angle = 360
  AttacherType = Attacher::AttachEngine3D
  FirstAngle = 0
  Height = 2
  Placement = pos=(30,0,0) rot=(0,0,1;0rad)
  Radius = 1.65
  SecondAngle = 0
  expr: .Placement.Base.x = <<BreadboardConfig>>.screw_spacing * 6
  expr: Height = <<BreadboardConfig>>.t_plate
  expr: Radius = <<BreadboardConfig>>.screw_corehole / 2
FEATURE [Part::Cylinder] Cylinder217
  Angle = 360
  AttacherType = Attacher::AttachEngine3D
  FirstAngle = 0
  Height = 2
  Placement = pos=(35,0,0) rot=(0,0,1;0rad)
  Radius = 1.65
  SecondAngle = 0
  expr: .Placement.Base.x = <<BreadboardConfig>>.screw_spacing * 7
  expr: Height = <<BreadboardConfig>>.t_plate
  expr: Radius = <<BreadboardConfig>>.screw_corehole / 2
FEATURE [Part::Cylinder] Cylinder218
  Angle = 360
  AttacherType = Attacher::AttachEngine3D
  FirstAngle = 0
  Height = 2
  Placement = pos=(40,0,0) rot=(0,0,1;0rad)
  Radius = 1.65
  SecondAngle = 0
  expr: .Placement.Base.x = <<BreadboardConfig>>.screw_spacing * 8
  expr: Height = <<BreadboardConfig>>.t_plate
  expr: Radius = <<BreadboardConfig>>.screw_corehole / 2
FEATURE [Part::Cylinder] Cylinder219
  Angle = 360
  AttacherType = Attacher::AttachEngine3D
  FirstAngle = 0
  Height = 2
  Placement = pos=(45,0,0) rot=(0,0,1;0rad)
  Radius = 1.65
  SecondAngle = 0
  expr: .Placement.Base.x = <<BreadboardConfig>>.screw_spacing * 9
  expr: Height = <<BreadboardConfig>>.t_plate
  expr: Radius = <<BreadboardConfig>>.screw_corehole / 2
FEATURE [Part::Cylinder] Cylinder220
  Angle = 360
  AttacherType = Attacher::AttachEngine3D
  FirstAngle = 0
  Height = 2
  Placement = pos=(50,0,0) rot=(0,0,1;0rad)
  Radius = 1.65
  SecondAngle = 0
  expr: .Placement.Base.x = <<BreadboardConfig>>.screw_spacing * 10
  expr: Height = <<BreadboardConfig>>.t_plate
  expr: Radius = <<BreadboardConfig>>.screw_corehole / 2
FEATURE [Part::Cylinder] Cylinder221
  Angle = 360
  AttacherType = Attacher::AttachEngine3D
  FirstAngle = 0
  Height = 2
  Placement = pos=(-5,0,0) rot=(0,0,1;0rad)
  Radius = 1.65
  SecondAngle = 0
  expr: .Placement.Base.x = <<BreadboardConfig>>.screw_spacing * -1
  expr: Height = <<BreadboardConfig>>.t_plate
  expr: Radius = <<BreadboardConfig>>.screw_corehole / 2
FEATURE [Part::Cylinder] Cylinder222
  Angle = 360
  AttacherType = Attacher::AttachEngine3D
  FirstAngle = 0
  Height = 2
  Placement = pos=(-10,0,0) rot=(0,0,1;0rad)
  Radius = 1.65
  SecondAngle = 0
  expr: .Placement.Base.x = <<BreadboardConfig>>.screw_spacing * -2
  expr: Height = <<BreadboardConfig>>.t_plate
  expr: Radius = <<BreadboardConfig>>.screw_corehole / 2
FEATURE [Part::Cylinder] Cylinder223
  Angle = 360
  AttacherType = Attacher::AttachEngine3D
  FirstAngle = 0
  Height = 2
  Placement = pos=(-15,0,0) rot=(0,0,1;0rad)
  Radius = 1.65
  SecondAngle = 0
  expr: .Placement.Base.x = <<BreadboardConfig>>.screw_spacing * -3
  expr: Height = <<BreadboardConfig>>.t_plate
  expr: Radius = <<BreadboardConfig>>.screw_corehole / 2
FEATURE [Part::Cylinder] Cylinder224
  Angle = 360
  AttacherType = Attacher::AttachEngine3D
  FirstAngle = 0
  Height = 2
  Placement = pos=(-20,0,0) rot=(0,0,1;0rad)
  Radius = 1.65
  SecondAngle = 0
  expr: .Placement.Base.x = <<BreadboardConfig>>.screw_spacing * -4
  expr: Height = <<BreadboardConfig>>.t_plate
  expr: Radius = <<BreadboardConfig>>.screw_corehole / 2
FEATURE [Part::Cylinder] Cylinder225
  Angle = 360
  AttacherType = Attacher::AttachEngine3D
  FirstAngle = 0
  Height = 2
  Placement = pos=(-25,0,0) rot=(0,0,1;0rad)
  Radius = 1.65
  SecondAngle = 0
  expr: .Placement.Base.x = <<BreadboardConfig>>.screw_spacing * -5
  expr: Height = <<BreadboardConfig>>.t_plate
  expr: Radius = <<BreadboardConfig>>.screw_corehole / 2
FEATURE [Part::Cylinder] Cylinder226
  Angle = 360
  AttacherType = Attacher::AttachEngine3D
  FirstAngle = 0
  Height = 2
  Placement = pos=(-30,0,0) rot=(0,0,1;0rad)
  Radius = 1.65
  SecondAngle = 0
  expr: .Placement.Base.x = <<BreadboardConfig>>.screw_spacing * -6
  expr: Height = <<BreadboardConfig>>.t_plate
  expr: Radius = <<BreadboardConfig>>.screw_corehole / 2
FEATURE [Part::Cylinder] Cylinder227
  Angle = 360
  AttacherType = Attacher::AttachEngine3D
  FirstAngle = 0
  Height = 2
  Placement = pos=(-35,0,0) rot=(0,0,1;0rad)
  Radius = 1.65
  SecondAngle = 0
  expr: .Placement.Base.x = <<BreadboardConfig>>.screw_spacing * -7
  expr: Height = <<BreadboardConfig>>.t_plate
  expr: Radius = <<BreadboardConfig>>.screw_corehole / 2
FEATURE [Part::Cylinder] Cylinder228
  Angle = 360
  AttacherType = Attacher::AttachEngine3D
  FirstAngle = 0
  Height = 2
  Placement = pos=(-40,0,0) rot=(0,0,1;0rad)
  Radius = 1.65
  SecondAngle = 0
  expr: .Placement.Base.x = <<BreadboardConfig>>.screw_spacing * -8
  expr: Height = <<BreadboardConfig>>.t_plate
  expr: Radius = <<BreadboardConfig>>.screw_corehole / 2
FEATURE [Part::Cylinder] Cylinder229
  Angle = 360
  AttacherType = Attacher::AttachEngine3D
  FirstAngle = 0
  Height = 2
  Placement = pos=(-45,0,0) rot=(0,0,1;0rad)
  Radius = 1.65
  SecondAngle = 0
  expr: .Placement.Base.x = <<BreadboardConfig>>.screw_spacing * -9
  expr: Height = <<BreadboardConfig>>.t_plate
  expr: Radius = <<BreadboardConfig>>.screw_corehole / 2
FEATURE [Part::Cylinder] Cylinder230
  Angle = 360
  AttacherType = Attacher::AttachEngine3D
  FirstAngle = 0
  Height = 2
  Placement = pos=(-50,0,0) rot=(0,0,1;0rad)
  Radius = 1.65
  SecondAngle = 0
  expr: .Placement.Base.x = <<BreadboardConfig>>.screw_spacing * -10
  expr: Height = <<BreadboardConfig>>.t_plate
  expr: Radius = <<BreadboardConfig>>.screw_corehole / 2
FEATURE [Part::Cylinder] Cylinder231
  Angle = 360
  AttacherType = Attacher::AttachEngine3D
  FirstAngle = 0
  Height = 2
  Radius = 1.65
  SecondAngle = 0
  expr: Height = <<BreadboardConfig>>.t_plate
  expr: Radius = <<BreadboardConfig>>.screw_corehole / 2
FEATURE [Part::MultiFuse] Fusion011
  Placement = pos=(0,50,0) rot=(0,0,1;0rad)
  Shapes = -> [Cylinder230,Cylinder229,Cylinder228,Cylinder227,Cylinder226,Cylinder225,Cylinder224,Cylinder223,Cylinder222,Cylinder221,Cylinder220,Cylinder219,Cylinder218,Cylinder217,Cylinder216,Cylinder215,Cylinder214,Cylinder213,Cylinder212,Cylinder211,Cylinder231]
  expr: .Placement.Base.y = <<BreadboardConfig>>.screw_spacing * 10
FEATURE [Part::Cylinder] Cylinder232
  Angle = 360
  AttacherType = Attacher::AttachEngine3D
  FirstAngle = 0
  Height = 2
  Placement = pos=(5,0,0) rot=(0,0,1;0rad)
  Radius = 1.65
  SecondAngle = 0
  expr: .Placement.Base.x = <<BreadboardConfig>>.screw_spacing * 1
  expr: Height = <<BreadboardConfig>>.t_plate
  expr: Radius = <<BreadboardConfig>>.screw_corehole / 2
FEATURE [Part::Cylinder] Cylinder233
  Angle = 360
  AttacherType = Attacher::AttachEngine3D
  FirstAngle = 0
  Height = 2
  Placement = pos=(10,0,0) rot=(0,0,1;0rad)
  Radius = 1.65
  SecondAngle = 0
  expr: .Placement.Base.x = <<BreadboardConfig>>.screw_spacing * 2
  expr: Height = <<BreadboardConfig>>.t_plate
  expr: Radius = <<BreadboardConfig>>.screw_corehole / 2
FEATURE [Part::Cylinder] Cylinder234
  Angle = 360
  AttacherType = Attacher::AttachEngine3D
  FirstAngle = 0
  Height = 2
  Placement = pos=(15,0,0) rot=(0,0,1;0rad)
  Radius = 1.65
  SecondAngle = 0
  expr: .Placement.Base.x = <<BreadboardConfig>>.screw_spacing * 3
  expr: Height = <<BreadboardConfig>>.t_plate
  expr: Radius = <<BreadboardConfig>>.screw_corehole / 2
FEATURE [Part::Cylinder] Cylinder235
  Angle = 360
  AttacherType = Attacher::AttachEngine3D
  FirstAngle = 0
  Height = 2
  Placement = pos=(20,0,0) rot=(0,0,1;0rad)
  Radius = 1.65
  SecondAngle = 0
  expr: .Placement.Base.x = <<BreadboardConfig>>.screw_spacing * 4
  expr: Height = <<BreadboardConfig>>.t_plate
  expr: Radius = <<BreadboardConfig>>.screw_corehole / 2
FEATURE [Part::Cylinder] Cylinder236
  Angle = 360
  AttacherType = Attacher::AttachEngine3D
  FirstAngle = 0
  Height = 2
  Placement = pos=(25,0,0) rot=(0,0,1;0rad)
  Radius = 1.65
  SecondAngle = 0
  expr: .Placement.Base.x = <<BreadboardConfig>>.screw_spacing * 5
  expr: Height = <<BreadboardConfig>>.t_plate
  expr: Radius = <<BreadboardConfig>>.screw_corehole / 2
FEATURE [Part::Cylinder] Cylinder237
  Angle = 360
  AttacherType = Attacher::AttachEngine3D
  FirstAngle = 0
  Height = 2
  Placement = pos=(30,0,0) rot=(0,0,1;0rad)
  Radius = 1.65
  SecondAngle = 0
  expr: .Placement.Base.x = <<BreadboardConfig>>.screw_spacing * 6
  expr: Height = <<BreadboardConfig>>.t_plate
  expr: Radius = <<BreadboardConfig>>.screw_corehole / 2
FEATURE [Part::Cylinder] Cylinder238
  Angle = 360
  AttacherType = Attacher::AttachEngine3D
  FirstAngle = 0
  Height = 2
  Placement = pos=(35,0,0) rot=(0,0,1;0rad)
  Radius = 1.65
  SecondAngle = 0
  expr: .Placement.Base.x = <<BreadboardConfig>>.screw_spacing * 7
  expr: Height = <<BreadboardConfig>>.t_plate
  expr: Radius = <<BreadboardConfig>>.screw_corehole / 2
FEATURE [Part::Cylinder] Cylinder239
  Angle = 360
  AttacherType = Attacher::AttachEngine3D
  FirstAngle = 0
  Height = 2
  Placement = pos=(40,0,0) rot=(0,0,1;0rad)
  Radius = 1.65
  SecondAngle = 0
  expr: .Placement.Base.x = <<BreadboardConfig>>.screw_spacing * 8
  expr: Height = <<BreadboardConfig>>.t_plate
  expr: Radius = <<BreadboardConfig>>.screw_corehole / 2
FEATURE [Part::Cylinder] Cylinder240
  Angle = 360
  AttacherType = Attacher::AttachEngine3D
  FirstAngle = 0
  Height = 2
  Placement = pos=(45,0,0) rot=(0,0,1;0rad)
  Radius = 1.65
  SecondAngle = 0
  expr: .Placement.Base.x = <<BreadboardConfig>>.screw_spacing * 9
  expr: Height = <<BreadboardConfig>>.t_plate
  expr: Radius = <<BreadboardConfig>>.screw_corehole / 2
FEATURE [Part::Cylinder] Cylinder241
  Angle = 360
  AttacherType = Attacher::AttachEngine3D
  FirstAngle = 0
  Height = 2
  Placement = pos=(50,0,0) rot=(0,0,1;0rad)
  Radius = 1.65
  SecondAngle = 0
  expr: .Placement.Base.x = <<BreadboardConfig>>.screw_spacing * 10
  expr: Height = <<BreadboardConfig>>.t_plate
  expr: Radius = <<BreadboardConfig>>.screw_corehole / 2
FEATURE [Part::Cylinder] Cylinder242
  Angle = 360
  AttacherType = Attacher::AttachEngine3D
  FirstAngle = 0
  Height = 2
  Placement = pos=(-5,0,0) rot=(0,0,1;0rad)
  Radius = 1.65
  SecondAngle = 0
  expr: .Placement.Base.x = <<BreadboardConfig>>.screw_spacing * -1
  expr: Height = <<BreadboardConfig>>.t_plate
  expr: Radius = <<BreadboardConfig>>.screw_corehole / 2
FEATURE [Part::Cylinder] Cylinder243
  Angle = 360
  AttacherType = Attacher::AttachEngine3D
  FirstAngle = 0
  Height = 2
  Placement = pos=(-10,0,0) rot=(0,0,1;0rad)
  Radius = 1.65
  SecondAngle = 0
  expr: .Placement.Base.x = <<BreadboardConfig>>.screw_spacing * -2
  expr: Height = <<BreadboardConfig>>.t_plate
  expr: Radius = <<BreadboardConfig>>.screw_corehole / 2
FEATURE [Part::Cylinder] Cylinder244
  Angle = 360
  AttacherType = Attacher::AttachEngine3D
  FirstAngle = 0
  Height = 2
  Placement = pos=(-15,0,0) rot=(0,0,1;0rad)
  Radius = 1.65
  SecondAngle = 0
  expr: .Placement.Base.x = <<BreadboardConfig>>.screw_spacing * -3
  expr: Height = <<BreadboardConfig>>.t_plate
  expr: Radius = <<BreadboardConfig>>.screw_corehole / 2
FEATURE [Part::Cylinder] Cylinder245
  Angle = 360
  AttacherType = Attacher::AttachEngine3D
  FirstAngle = 0
  Height = 2
  Placement = pos=(-20,0,0) rot=(0,0,1;0rad)
  Radius = 1.65
  SecondAngle = 0
  expr: .Placement.Base.x = <<BreadboardConfig>>.screw_spacing * -4
  expr: Height = <<BreadboardConfig>>.t_plate
  expr: Radius = <<BreadboardConfig>>.screw_corehole / 2
FEATURE [Part::Cylinder] Cylinder246
  Angle = 360
  AttacherType = Attacher::AttachEngine3D
  FirstAngle = 0
  Height = 2
  Placement = pos=(-25,0,0) rot=(0,0,1;0rad)
  Radius = 1.65
  SecondAngle = 0
  expr: .Placement.Base.x = <<BreadboardConfig>>.screw_spacing * -5
  expr: Height = <<BreadboardConfig>>.t_plate
  expr: Radius = <<BreadboardConfig>>.screw_corehole / 2
FEATURE [Part::Cylinder] Cylinder247
  Angle = 360
  AttacherType = Attacher::AttachEngine3D
  FirstAngle = 0
  Height = 2
  Placement = pos=(-30,0,0) rot=(0,0,1;0rad)
  Radius = 1.65
  SecondAngle = 0
  expr: .Placement.Base.x = <<BreadboardConfig>>.screw_spacing * -6
  expr: Height = <<BreadboardConfig>>.t_plate
  expr: Radius = <<BreadboardConfig>>.screw_corehole / 2
FEATURE [Part::Cylinder] Cylinder248
  Angle = 360
  AttacherType = Attacher::AttachEngine3D
  FirstAngle = 0
  Height = 2
  Placement = pos=(-35,0,0) rot=(0,0,1;0rad)
  Radius = 1.65
  SecondAngle = 0
  expr: .Placement.Base.x = <<BreadboardConfig>>.screw_spacing * -7
  expr: Height = <<BreadboardConfig>>.t_plate
  expr: Radius = <<BreadboardConfig>>.screw_corehole / 2
FEATURE [Part::Cylinder] Cylinder249
  Angle = 360
  AttacherType = Attacher::AttachEngine3D
  FirstAngle = 0
  Height = 2
  Placement = pos=(-40,0,0) rot=(0,0,1;0rad)
  Radius = 1.65
  SecondAngle = 0
  expr: .Placement.Base.x = <<BreadboardConfig>>.screw_spacing * -8
  expr: Height = <<BreadboardConfig>>.t_plate
  expr: Radius = <<BreadboardConfig>>.screw_corehole / 2
FEATURE [Part::Cylinder] Cylinder250
  Angle = 360
  AttacherType = Attacher::AttachEngine3D
  FirstAngle = 0
  Height = 2
  Placement = pos=(-45,0,0) rot=(0,0,1;0rad)
  Radius = 1.65
  SecondAngle = 0
  expr: .Placement.Base.x = <<BreadboardConfig>>.screw_spacing * -9
  expr: Height = <<BreadboardConfig>>.t_plate
  expr: Radius = <<BreadboardConfig>>.screw_corehole / 2
FEATURE [Part::Cylinder] Cylinder251
  Angle = 360
  AttacherType = Attacher::AttachEngine3D
  FirstAngle = 0
  Height = 2
  Placement = pos=(-50,0,0) rot=(0,0,1;0rad)
  Radius = 1.65
  SecondAngle = 0
  expr: .Placement.Base.x = <<BreadboardConfig>>.screw_spacing * -10
  expr: Height = <<BreadboardConfig>>.t_plate
  expr: Radius = <<BreadboardConfig>>.screw_corehole / 2
FEATURE [Part::Cylinder] Cylinder252
  Angle = 360
  AttacherType = Attacher::AttachEngine3D
  FirstAngle = 0
  Height = 2
  Radius = 1.65
  SecondAngle = 0
  expr: Height = <<BreadboardConfig>>.t_plate
  expr: Radius = <<BreadboardConfig>>.screw_corehole / 2
FEATURE [Part::MultiFuse] Fusion012
  Placement = pos=(0,-5,0) rot=(0,0,1;0rad)
  Shapes = -> [Cylinder251,Cylinder250,Cylinder249,Cylinder248,Cylinder247,Cylinder246,Cylinder245,Cylinder244,Cylinder243,Cylinder242,Cylinder241,Cylinder240,Cylinder239,Cylinder238,Cylinder237,Cylinder236,Cylinder235,Cylinder234,Cylinder233,Cylinder232,Cylinder252]
  expr: .Placement.Base.y = <<BreadboardConfig>>.screw_spacing * -1
FEATURE [Part::Cylinder] Cylinder253
  Angle = 360
  AttacherType = Attacher::AttachEngine3D
  FirstAngle = 0
  Height = 2
  Placement = pos=(5,0,0) rot=(0,0,1;0rad)
  Radius = 1.65
  SecondAngle = 0
  expr: .Placement.Base.x = <<BreadboardConfig>>.screw_spacing * 1
  expr: Height = <<BreadboardConfig>>.t_plate
  expr: Radius = <<BreadboardConfig>>.screw_corehole / 2
FEATURE [Part::Cylinder] Cylinder254
  Angle = 360
  AttacherType = Attacher::AttachEngine3D
  FirstAngle = 0
  Height = 2
  Placement = pos=(10,0,0) rot=(0,0,1;0rad)
  Radius = 1.65
  SecondAngle = 0
  expr: .Placement.Base.x = <<BreadboardConfig>>.screw_spacing * 2
  expr: Height = <<BreadboardConfig>>.t_plate
  expr: Radius = <<BreadboardConfig>>.screw_corehole / 2
FEATURE [Part::Cylinder] Cylinder255
  Angle = 360
  AttacherType = Attacher::AttachEngine3D
  FirstAngle = 0
  Height = 2
  Placement = pos=(15,0,0) rot=(0,0,1;0rad)
  Radius = 1.65
  SecondAngle = 0
  expr: .Placement.Base.x = <<BreadboardConfig>>.screw_spacing * 3
  expr: Height = <<BreadboardConfig>>.t_plate
  expr: Radius = <<BreadboardConfig>>.screw_corehole / 2
FEATURE [Part::Cylinder] Cylinder256
  Angle = 360
  AttacherType = Attacher::AttachEngine3D
  FirstAngle = 0
  Height = 2
  Placement = pos=(20,0,0) rot=(0,0,1;0rad)
  Radius = 1.65
  SecondAngle = 0
  expr: .Placement.Base.x = <<BreadboardConfig>>.screw_spacing * 4
  expr: Height = <<BreadboardConfig>>.t_plate
  expr: Radius = <<BreadboardConfig>>.screw_corehole / 2
FEATURE [Part::Cylinder] Cylinder257
  Angle = 360
  AttacherType = Attacher::AttachEngine3D
  FirstAngle = 0
  Height = 2
  Placement = pos=(25,0,0) rot=(0,0,1;0rad)
  Radius = 1.65
  SecondAngle = 0
  expr: .Placement.Base.x = <<BreadboardConfig>>.screw_spacing * 5
  expr: Height = <<BreadboardConfig>>.t_plate
  expr: Radius = <<BreadboardConfig>>.screw_corehole / 2
FEATURE [Part::Cylinder] Cylinder258
  Angle = 360
  AttacherType = Attacher::AttachEngine3D
  FirstAngle = 0
  Height = 2
  Placement = pos=(30,0,0) rot=(0,0,1;0rad)
  Radius = 1.65
  SecondAngle = 0
  expr: .Placement.Base.x = <<BreadboardConfig>>.screw_spacing * 6
  expr: Height = <<BreadboardConfig>>.t_plate
  expr: Radius = <<BreadboardConfig>>.screw_corehole / 2
FEATURE [Part::Cylinder] Cylinder259
  Angle = 360
  AttacherType = Attacher::AttachEngine3D
  FirstAngle = 0
  Height = 2
  Placement = pos=(35,0,0) rot=(0,0,1;0rad)
  Radius = 1.65
  SecondAngle = 0
  expr: .Placement.Base.x = <<BreadboardConfig>>.screw_spacing * 7
  expr: Height = <<BreadboardConfig>>.t_plate
  expr: Radius = <<BreadboardConfig>>.screw_corehole / 2
FEATURE [Part::Cylinder] Cylinder260
  Angle = 360
  AttacherType = Attacher::AttachEngine3D
  FirstAngle = 0
  Height = 2
  Placement = pos=(40,0,0) rot=(0,0,1;0rad)
  Radius = 1.65
  SecondAngle = 0
  expr: .Placement.Base.x = <<BreadboardConfig>>.screw_spacing * 8
  expr: Height = <<BreadboardConfig>>.t_plate
  expr: Radius = <<BreadboardConfig>>.screw_corehole / 2
FEATURE [Part::Cylinder] Cylinder261
  Angle = 360
  AttacherType = Attacher::AttachEngine3D
  FirstAngle = 0
  Height = 2
  Placement = pos=(45,0,0) rot=(0,0,1;0rad)
  Radius = 1.65
  SecondAngle = 0
  expr: .Placement.Base.x = <<BreadboardConfig>>.screw_spacing * 9
  expr: Height = <<BreadboardConfig>>.t_plate
  expr: Radius = <<BreadboardConfig>>.screw_corehole / 2
FEATURE [Part::Cylinder] Cylinder262
  Angle = 360
  AttacherType = Attacher::AttachEngine3D
  FirstAngle = 0
  Height = 2
  Placement = pos=(50,0,0) rot=(0,0,1;0rad)
  Radius = 1.65
  SecondAngle = 0
  expr: .Placement.Base.x = <<BreadboardConfig>>.screw_spacing * 10
  expr: Height = <<BreadboardConfig>>.t_plate
  expr: Radius = <<BreadboardConfig>>.screw_corehole / 2
FEATURE [Part::Cylinder] Cylinder263
  Angle = 360
  AttacherType = Attacher::AttachEngine3D
  FirstAngle = 0
  Height = 2
  Placement = pos=(-5,0,0) rot=(0,0,1;0rad)
  Radius = 1.65
  SecondAngle = 0
  expr: .Placement.Base.x = <<BreadboardConfig>>.screw_spacing * -1
  expr: Height = <<BreadboardConfig>>.t_plate
  expr: Radius = <<BreadboardConfig>>.screw_corehole / 2
FEATURE [Part::Cylinder] Cylinder264
  Angle = 360
  AttacherType = Attacher::AttachEngine3D
  FirstAngle = 0
  Height = 2
  Placement = pos=(-10,0,0) rot=(0,0,1;0rad)
  Radius = 1.65
  SecondAngle = 0
  expr: .Placement.Base.x = <<BreadboardConfig>>.screw_spacing * -2
  expr: Height = <<BreadboardConfig>>.t_plate
  expr: Radius = <<BreadboardConfig>>.screw_corehole / 2
FEATURE [Part::Cylinder] Cylinder265
  Angle = 360
  AttacherType = Attacher::AttachEngine3D
  FirstAngle = 0
  Height = 2
  Placement = pos=(-15,0,0) rot=(0,0,1;0rad)
  Radius = 1.65
  SecondAngle = 0
  expr: .Placement.Base.x = <<BreadboardConfig>>.screw_spacing * -3
  expr: Height = <<BreadboardConfig>>.t_plate
  expr: Radius = <<BreadboardConfig>>.screw_corehole / 2
FEATURE [Part::Cylinder] Cylinder266
  Angle = 360
  AttacherType = Attacher::AttachEngine3D
  FirstAngle = 0
  Height = 2
  Placement = pos=(-20,0,0) rot=(0,0,1;0rad)
  Radius = 1.65
  SecondAngle = 0
  expr: .Placement.Base.x = <<BreadboardConfig>>.screw_spacing * -4
  expr: Height = <<BreadboardConfig>>.t_plate
  expr: Radius = <<BreadboardConfig>>.screw_corehole / 2
FEATURE [Part::Cylinder] Cylinder267
  Angle = 360
  AttacherType = Attacher::AttachEngine3D
  FirstAngle = 0
  Height = 2
  Placement = pos=(-25,0,0) rot=(0,0,1;0rad)
  Radius = 1.65
  SecondAngle = 0
  expr: .Placement.Base.x = <<BreadboardConfig>>.screw_spacing * -5
  expr: Height = <<BreadboardConfig>>.t_plate
  expr: Radius = <<BreadboardConfig>>.screw_corehole / 2
FEATURE [Part::Cylinder] Cylinder268
  Angle = 360
  AttacherType = Attacher::AttachEngine3D
  FirstAngle = 0
  Height = 2
  Placement = pos=(-30,0,0) rot=(0,0,1;0rad)
  Radius = 1.65
  SecondAngle = 0
  expr: .Placement.Base.x = <<BreadboardConfig>>.screw_spacing * -6
  expr: Height = <<BreadboardConfig>>.t_plate
  expr: Radius = <<BreadboardConfig>>.screw_corehole / 2
FEATURE [Part::Cylinder] Cylinder269
  Angle = 360
  AttacherType = Attacher::AttachEngine3D
  FirstAngle = 0
  Height = 2
  Placement = pos=(-35,0,0) rot=(0,0,1;0rad)
  Radius = 1.65
  SecondAngle = 0
  expr: .Placement.Base.x = <<BreadboardConfig>>.screw_spacing * -7
  expr: Height = <<BreadboardConfig>>.t_plate
  expr: Radius = <<BreadboardConfig>>.screw_corehole / 2
FEATURE [Part::Cylinder] Cylinder270
  Angle = 360
  AttacherType = Attacher::AttachEngine3D
  FirstAngle = 0
  Height = 2
  Placement = pos=(-40,0,0) rot=(0,0,1;0rad)
  Radius = 1.65
  SecondAngle = 0
  expr: .Placement.Base.x = <<BreadboardConfig>>.screw_spacing * -8
  expr: Height = <<BreadboardConfig>>.t_plate
  expr: Radius = <<BreadboardConfig>>.screw_corehole / 2
FEATURE [Part::Cylinder] Cylinder271
  Angle = 360
  AttacherType = Attacher::AttachEngine3D
  FirstAngle = 0
  Height = 2
  Placement = pos=(-45,0,0) rot=(0,0,1;0rad)
  Radius = 1.65
  SecondAngle = 0
  expr: .Placement.Base.x = <<BreadboardConfig>>.screw_spacing * -9
  expr: Height = <<BreadboardConfig>>.t_plate
  expr: Radius = <<BreadboardConfig>>.screw_corehole / 2
FEATURE [Part::Cylinder] Cylinder272
  Angle = 360
  AttacherType = Attacher::AttachEngine3D
  FirstAngle = 0
  Height = 2
  Placement = pos=(-50,0,0) rot=(0,0,1;0rad)
  Radius = 1.65
  SecondAngle = 0
  expr: .Placement.Base.x = <<BreadboardConfig>>.screw_spacing * -10
  expr: Height = <<BreadboardConfig>>.t_plate
  expr: Radius = <<BreadboardConfig>>.screw_corehole / 2
FEATURE [Part::Cylinder] Cylinder273
  Angle = 360
  AttacherType = Attacher::AttachEngine3D
  FirstAngle = 0
  Height = 2
  Radius = 1.65
  SecondAngle = 0
  expr: Height = <<BreadboardConfig>>.t_plate
  expr: Radius = <<BreadboardConfig>>.screw_corehole / 2
FEATURE [Part::MultiFuse] Fusion013
  Placement = pos=(0,-10,0) rot=(0,0,1;0rad)
  Shapes = -> [Cylinder272,Cylinder271,Cylinder270,Cylinder269,Cylinder268,Cylinder267,Cylinder266,Cylinder265,Cylinder264,Cylinder263,Cylinder262,Cylinder261,Cylinder260,Cylinder259,Cylinder258,Cylinder257,Cylinder256,Cylinder255,Cylinder254,Cylinder253,Cylinder273]
  expr: .Placement.Base.y = <<BreadboardConfig>>.screw_spacing * -2
FEATURE [Part::Cylinder] Cylinder274
  Angle = 360
  AttacherType = Attacher::AttachEngine3D
  FirstAngle = 0
  Height = 2
  Placement = pos=(5,0,0) rot=(0,0,1;0rad)
  Radius = 1.65
  SecondAngle = 0
  expr: .Placement.Base.x = <<BreadboardConfig>>.screw_spacing * 1
  expr: Height = <<BreadboardConfig>>.t_plate
  expr: Radius = <<BreadboardConfig>>.screw_corehole / 2
FEATURE [Part::Cylinder] Cylinder275
  Angle = 360
  AttacherType = Attacher::AttachEngine3D
  FirstAngle = 0
  Height = 2
  Placement = pos=(10,0,0) rot=(0,0,1;0rad)
  Radius = 1.65
  SecondAngle = 0
  expr: .Placement.Base.x = <<BreadboardConfig>>.screw_spacing * 2
  expr: Height = <<BreadboardConfig>>.t_plate
  expr: Radius = <<BreadboardConfig>>.screw_corehole / 2
FEATURE [Part::Cylinder] Cylinder276
  Angle = 360
  AttacherType = Attacher::AttachEngine3D
  FirstAngle = 0
  Height = 2
  Placement = pos=(15,0,0) rot=(0,0,1;0rad)
  Radius = 1.65
  SecondAngle = 0
  expr: .Placement.Base.x = <<BreadboardConfig>>.screw_spacing * 3
  expr: Height = <<BreadboardConfig>>.t_plate
  expr: Radius = <<BreadboardConfig>>.screw_corehole / 2
FEATURE [Part::Cylinder] Cylinder277
  Angle = 360
  AttacherType = Attacher::AttachEngine3D
  FirstAngle = 0
  Height = 2
  Placement = pos=(20,0,0) rot=(0,0,1;0rad)
  Radius = 1.65
  SecondAngle = 0
  expr: .Placement.Base.x = <<BreadboardConfig>>.screw_spacing * 4
  expr: Height = <<BreadboardConfig>>.t_plate
  expr: Radius = <<BreadboardConfig>>.screw_corehole / 2
FEATURE [Part::Cylinder] Cylinder278
  Angle = 360
  AttacherType = Attacher::AttachEngine3D
  FirstAngle = 0
  Height = 2
  Placement = pos=(25,0,0) rot=(0,0,1;0rad)
  Radius = 1.65
  SecondAngle = 0
  expr: .Placement.Base.x = <<BreadboardConfig>>.screw_spacing * 5
  expr: Height = <<BreadboardConfig>>.t_plate
  expr: Radius = <<BreadboardConfig>>.screw_corehole / 2
FEATURE [Part::Cylinder] Cylinder279
  Angle = 360
  AttacherType = Attacher::AttachEngine3D
  FirstAngle = 0
  Height = 2
  Placement = pos=(30,0,0) rot=(0,0,1;0rad)
  Radius = 1.65
  SecondAngle = 0
  expr: .Placement.Base.x = <<BreadboardConfig>>.screw_spacing * 6
  expr: Height = <<BreadboardConfig>>.t_plate
  expr: Radius = <<BreadboardConfig>>.screw_corehole / 2
FEATURE [Part::Cylinder] Cylinder280
  Angle = 360
  AttacherType = Attacher::AttachEngine3D
  FirstAngle = 0
  Height = 2
  Placement = pos=(35,0,0) rot=(0,0,1;0rad)
  Radius = 1.65
  SecondAngle = 0
  expr: .Placement.Base.x = <<BreadboardConfig>>.screw_spacing * 7
  expr: Height = <<BreadboardConfig>>.t_plate
  expr: Radius = <<BreadboardConfig>>.screw_corehole / 2
FEATURE [Part::Cylinder] Cylinder281
  Angle = 360
  AttacherType = Attacher::AttachEngine3D
  FirstAngle = 0
  Height = 2
  Placement = pos=(40,0,0) rot=(0,0,1;0rad)
  Radius = 1.65
  SecondAngle = 0
  expr: .Placement.Base.x = <<BreadboardConfig>>.screw_spacing * 8
  expr: Height = <<BreadboardConfig>>.t_plate
  expr: Radius = <<BreadboardConfig>>.screw_corehole / 2
FEATURE [Part::Cylinder] Cylinder282
  Angle = 360
  AttacherType = Attacher::AttachEngine3D
  FirstAngle = 0
  Height = 2
  Placement = pos=(45,0,0) rot=(0,0,1;0rad)
  Radius = 1.65
  SecondAngle = 0
  expr: .Placement.Base.x = <<BreadboardConfig>>.screw_spacing * 9
  expr: Height = <<BreadboardConfig>>.t_plate
  expr: Radius = <<BreadboardConfig>>.screw_corehole / 2
FEATURE [Part::Cylinder] Cylinder283
  Angle = 360
  AttacherType = Attacher::AttachEngine3D
  FirstAngle = 0
  Height = 2
  Placement = pos=(50,0,0) rot=(0,0,1;0rad)
  Radius = 1.65
  SecondAngle = 0
  expr: .Placement.Base.x = <<BreadboardConfig>>.screw_spacing * 10
  expr: Height = <<BreadboardConfig>>.t_plate
  expr: Radius = <<BreadboardConfig>>.screw_corehole / 2
FEATURE [Part::Cylinder] Cylinder284
  Angle = 360
  AttacherType = Attacher::AttachEngine3D
  FirstAngle = 0
  Height = 2
  Placement = pos=(-5,0,0) rot=(0,0,1;0rad)
  Radius = 1.65
  SecondAngle = 0
  expr: .Placement.Base.x = <<BreadboardConfig>>.screw_spacing * -1
  expr: Height = <<BreadboardConfig>>.t_plate
  expr: Radius = <<BreadboardConfig>>.screw_corehole / 2
FEATURE [Part::Cylinder] Cylinder285
  Angle = 360
  AttacherType = Attacher::AttachEngine3D
  FirstAngle = 0
  Height = 2
  Placement = pos=(-10,0,0) rot=(0,0,1;0rad)
  Radius = 1.65
  SecondAngle = 0
  expr: .Placement.Base.x = <<BreadboardConfig>>.screw_spacing * -2
  expr: Height = <<BreadboardConfig>>.t_plate
  expr: Radius = <<BreadboardConfig>>.screw_corehole / 2
FEATURE [Part::Cylinder] Cylinder286
  Angle = 360
  AttacherType = Attacher::AttachEngine3D
  FirstAngle = 0
  Height = 2
  Placement = pos=(-15,0,0) rot=(0,0,1;0rad)
  Radius = 1.65
  SecondAngle = 0
  expr: .Placement.Base.x = <<BreadboardConfig>>.screw_spacing * -3
  expr: Height = <<BreadboardConfig>>.t_plate
  expr: Radius = <<BreadboardConfig>>.screw_corehole / 2
FEATURE [Part::Cylinder] Cylinder287
  Angle = 360
  AttacherType = Attacher::AttachEngine3D
  FirstAngle = 0
  Height = 2
  Placement = pos=(-20,0,0) rot=(0,0,1;0rad)
  Radius = 1.65
  SecondAngle = 0
  expr: .Placement.Base.x = <<BreadboardConfig>>.screw_spacing * -4
  expr: Height = <<BreadboardConfig>>.t_plate
  expr: Radius = <<BreadboardConfig>>.screw_corehole / 2
FEATURE [Part::Cylinder] Cylinder288
  Angle = 360
  AttacherType = Attacher::AttachEngine3D
  FirstAngle = 0
  Height = 2
  Placement = pos=(-25,0,0) rot=(0,0,1;0rad)
  Radius = 1.65
  SecondAngle = 0
  expr: .Placement.Base.x = <<BreadboardConfig>>.screw_spacing * -5
  expr: Height = <<BreadboardConfig>>.t_plate
  expr: Radius = <<BreadboardConfig>>.screw_corehole / 2
FEATURE [Part::Cylinder] Cylinder289
  Angle = 360
  AttacherType = Attacher::AttachEngine3D
  FirstAngle = 0
  Height = 2
  Placement = pos=(-30,0,0) rot=(0,0,1;0rad)
  Radius = 1.65
  SecondAngle = 0
  expr: .Placement.Base.x = <<BreadboardConfig>>.screw_spacing * -6
  expr: Height = <<BreadboardConfig>>.t_plate
  expr: Radius = <<BreadboardConfig>>.screw_corehole / 2
FEATURE [Part::Cylinder] Cylinder290
  Angle = 360
  AttacherType = Attacher::AttachEngine3D
  FirstAngle = 0
  Height = 2
  Placement = pos=(-35,0,0) rot=(0,0,1;0rad)
  Radius = 1.65
  SecondAngle = 0
  expr: .Placement.Base.x = <<BreadboardConfig>>.screw_spacing * -7
  expr: Height = <<BreadboardConfig>>.t_plate
  expr: Radius = <<BreadboardConfig>>.screw_corehole / 2
FEATURE [Part::Cylinder] Cylinder291
  Angle = 360
  AttacherType = Attacher::AttachEngine3D
  FirstAngle = 0
  Height = 2
  Placement = pos=(-40,0,0) rot=(0,0,1;0rad)
  Radius = 1.65
  SecondAngle = 0
  expr: .Placement.Base.x = <<BreadboardConfig>>.screw_spacing * -8
  expr: Height = <<BreadboardConfig>>.t_plate
  expr: Radius = <<BreadboardConfig>>.screw_corehole / 2
FEATURE [Part::Cylinder] Cylinder292
  Angle = 360
  AttacherType = Attacher::AttachEngine3D
  FirstAngle = 0
  Height = 2
  Placement = pos=(-45,0,0) rot=(0,0,1;0rad)
  Radius = 1.65
  SecondAngle = 0
  expr: .Placement.Base.x = <<BreadboardConfig>>.screw_spacing * -9
  expr: Height = <<BreadboardConfig>>.t_plate
  expr: Radius = <<BreadboardConfig>>.screw_corehole / 2
FEATURE [Part::Cylinder] Cylinder293
  Angle = 360
  AttacherType = Attacher::AttachEngine3D
  FirstAngle = 0
  Height = 2
  Placement = pos=(-50,0,0) rot=(0,0,1;0rad)
  Radius = 1.65
  SecondAngle = 0
  expr: .Placement.Base.x = <<BreadboardConfig>>.screw_spacing * -10
  expr: Height = <<BreadboardConfig>>.t_plate
  expr: Radius = <<BreadboardConfig>>.screw_corehole / 2
FEATURE [Part::Cylinder] Cylinder294
  Angle = 360
  AttacherType = Attacher::AttachEngine3D
  FirstAngle = 0
  Height = 2
  Radius = 1.65
  SecondAngle = 0
  expr: Height = <<BreadboardConfig>>.t_plate
  expr: Radius = <<BreadboardConfig>>.screw_corehole / 2
FEATURE [Part::MultiFuse] Fusion014
  Placement = pos=(0,-15,0) rot=(0,0,1;0rad)
  Shapes = -> [Cylinder293,Cylinder292,Cylinder291,Cylinder290,Cylinder289,Cylinder288,Cylinder287,Cylinder286,Cylinder285,Cylinder284,Cylinder283,Cylinder282,Cylinder281,Cylinder280,Cylinder279,Cylinder278,Cylinder277,Cylinder276,Cylinder275,Cylinder274,Cylinder294]
  expr: .Placement.Base.y = <<BreadboardConfig>>.screw_spacing * -3
FEATURE [Part::Cylinder] Cylinder295
  Angle = 360
  AttacherType = Attacher::AttachEngine3D
  FirstAngle = 0
  Height = 2
  Placement = pos=(5,0,0) rot=(0,0,1;0rad)
  Radius = 1.65
  SecondAngle = 0
  expr: .Placement.Base.x = <<BreadboardConfig>>.screw_spacing * 1
  expr: Height = <<BreadboardConfig>>.t_plate
  expr: Radius = <<BreadboardConfig>>.screw_corehole / 2
FEATURE [Part::Cylinder] Cylinder296
  Angle = 360
  AttacherType = Attacher::AttachEngine3D
  FirstAngle = 0
  Height = 2
  Placement = pos=(10,0,0) rot=(0,0,1;0rad)
  Radius = 1.65
  SecondAngle = 0
  expr: .Placement.Base.x = <<BreadboardConfig>>.screw_spacing * 2
  expr: Height = <<BreadboardConfig>>.t_plate
  expr: Radius = <<BreadboardConfig>>.screw_corehole / 2
FEATURE [Part::Cylinder] Cylinder297
  Angle = 360
  AttacherType = Attacher::AttachEngine3D
  FirstAngle = 0
  Height = 2
  Placement = pos=(15,0,0) rot=(0,0,1;0rad)
  Radius = 1.65
  SecondAngle = 0
  expr: .Placement.Base.x = <<BreadboardConfig>>.screw_spacing * 3
  expr: Height = <<BreadboardConfig>>.t_plate
  expr: Radius = <<BreadboardConfig>>.screw_corehole / 2
FEATURE [Part::Cylinder] Cylinder298
  Angle = 360
  AttacherType = Attacher::AttachEngine3D
  FirstAngle = 0
  Height = 2
  Placement = pos=(20,0,0) rot=(0,0,1;0rad)
  Radius = 1.65
  SecondAngle = 0
  expr: .Placement.Base.x = <<BreadboardConfig>>.screw_spacing * 4
  expr: Height = <<BreadboardConfig>>.t_plate
  expr: Radius = <<BreadboardConfig>>.screw_corehole / 2
FEATURE [Part::Cylinder] Cylinder299
  Angle = 360
  AttacherType = Attacher::AttachEngine3D
  FirstAngle = 0
  Height = 2
  Placement = pos=(25,0,0) rot=(0,0,1;0rad)
  Radius = 1.65
  SecondAngle = 0
  expr: .Placement.Base.x = <<BreadboardConfig>>.screw_spacing * 5
  expr: Height = <<BreadboardConfig>>.t_plate
  expr: Radius = <<BreadboardConfig>>.screw_corehole / 2
FEATURE [Part::Cylinder] Cylinder300
  Angle = 360
  AttacherType = Attacher::AttachEngine3D
  FirstAngle = 0
  Height = 2
  Placement = pos=(30,0,0) rot=(0,0,1;0rad)
  Radius = 1.65
  SecondAngle = 0
  expr: .Placement.Base.x = <<BreadboardConfig>>.screw_spacing * 6
  expr: Height = <<BreadboardConfig>>.t_plate
  expr: Radius = <<BreadboardConfig>>.screw_corehole / 2
FEATURE [Part::Cylinder] Cylinder301
  Angle = 360
  AttacherType = Attacher::AttachEngine3D
  FirstAngle = 0
  Height = 2
  Placement = pos=(35,0,0) rot=(0,0,1;0rad)
  Radius = 1.65
  SecondAngle = 0
  expr: .Placement.Base.x = <<BreadboardConfig>>.screw_spacing * 7
  expr: Height = <<BreadboardConfig>>.t_plate
  expr: Radius = <<BreadboardConfig>>.screw_corehole / 2
FEATURE [Part::Cylinder] Cylinder302
  Angle = 360
  AttacherType = Attacher::AttachEngine3D
  FirstAngle = 0
  Height = 2
  Placement = pos=(40,0,0) rot=(0,0,1;0rad)
  Radius = 1.65
  SecondAngle = 0
  expr: .Placement.Base.x = <<BreadboardConfig>>.screw_spacing * 8
  expr: Height = <<BreadboardConfig>>.t_plate
  expr: Radius = <<BreadboardConfig>>.screw_corehole / 2
FEATURE [Part::Cylinder] Cylinder303
  Angle = 360
  AttacherType = Attacher::AttachEngine3D
  FirstAngle = 0
  Height = 2
  Placement = pos=(45,0,0) rot=(0,0,1;0rad)
  Radius = 1.65
  SecondAngle = 0
  expr: .Placement.Base.x = <<BreadboardConfig>>.screw_spacing * 9
  expr: Height = <<BreadboardConfig>>.t_plate
  expr: Radius = <<BreadboardConfig>>.screw_corehole / 2
FEATURE [Part::Cylinder] Cylinder304
  Angle = 360
  AttacherType = Attacher::AttachEngine3D
  FirstAngle = 0
  Height = 2
  Placement = pos=(50,0,0) rot=(0,0,1;0rad)
  Radius = 1.65
  SecondAngle = 0
  expr: .Placement.Base.x = <<BreadboardConfig>>.screw_spacing * 10
  expr: Height = <<BreadboardConfig>>.t_plate
  expr: Radius = <<BreadboardConfig>>.screw_corehole / 2
FEATURE [Part::Cylinder] Cylinder305
  Angle = 360
  AttacherType = Attacher::AttachEngine3D
  FirstAngle = 0
  Height = 2
  Placement = pos=(-5,0,0) rot=(0,0,1;0rad)
  Radius = 1.65
  SecondAngle = 0
  expr: .Placement.Base.x = <<BreadboardConfig>>.screw_spacing * -1
  expr: Height = <<BreadboardConfig>>.t_plate
  expr: Radius = <<BreadboardConfig>>.screw_corehole / 2
FEATURE [Part::Cylinder] Cylinder306
  Angle = 360
  AttacherType = Attacher::AttachEngine3D
  FirstAngle = 0
  Height = 2
  Placement = pos=(-10,0,0) rot=(0,0,1;0rad)
  Radius = 1.65
  SecondAngle = 0
  expr: .Placement.Base.x = <<BreadboardConfig>>.screw_spacing * -2
  expr: Height = <<BreadboardConfig>>.t_plate
  expr: Radius = <<BreadboardConfig>>.screw_corehole / 2
FEATURE [Part::Cylinder] Cylinder307
  Angle = 360
  AttacherType = Attacher::AttachEngine3D
  FirstAngle = 0
  Height = 2
  Placement = pos=(-15,0,0) rot=(0,0,1;0rad)
  Radius = 1.65
  SecondAngle = 0
  expr: .Placement.Base.x = <<BreadboardConfig>>.screw_spacing * -3
  expr: Height = <<BreadboardConfig>>.t_plate
  expr: Radius = <<BreadboardConfig>>.screw_corehole / 2
FEATURE [Part::Cylinder] Cylinder308
  Angle = 360
  AttacherType = Attacher::AttachEngine3D
  FirstAngle = 0
  Height = 2
  Placement = pos=(-20,0,0) rot=(0,0,1;0rad)
  Radius = 1.65
  SecondAngle = 0
  expr: .Placement.Base.x = <<BreadboardConfig>>.screw_spacing * -4
  expr: Height = <<BreadboardConfig>>.t_plate
  expr: Radius = <<BreadboardConfig>>.screw_corehole / 2
FEATURE [Part::Cylinder] Cylinder309
  Angle = 360
  AttacherType = Attacher::AttachEngine3D
  FirstAngle = 0
  Height = 2
  Placement = pos=(-25,0,0) rot=(0,0,1;0rad)
  Radius = 1.65
  SecondAngle = 0
  expr: .Placement.Base.x = <<BreadboardConfig>>.screw_spacing * -5
  expr: Height = <<BreadboardConfig>>.t_plate
  expr: Radius = <<BreadboardConfig>>.screw_corehole / 2
FEATURE [Part::Cylinder] Cylinder310
  Angle = 360
  AttacherType = Attacher::AttachEngine3D
  FirstAngle = 0
  Height = 2
  Placement = pos=(-30,0,0) rot=(0,0,1;0rad)
  Radius = 1.65
  SecondAngle = 0
  expr: .Placement.Base.x = <<BreadboardConfig>>.screw_spacing * -6
  expr: Height = <<BreadboardConfig>>.t_plate
  expr: Radius = <<BreadboardConfig>>.screw_corehole / 2
FEATURE [Part::Cylinder] Cylinder311
  Angle = 360
  AttacherType = Attacher::AttachEngine3D
  FirstAngle = 0
  Height = 2
  Placement = pos=(-35,0,0) rot=(0,0,1;0rad)
  Radius = 1.65
  SecondAngle = 0
  expr: .Placement.Base.x = <<BreadboardConfig>>.screw_spacing * -7
  expr: Height = <<BreadboardConfig>>.t_plate
  expr: Radius = <<BreadboardConfig>>.screw_corehole / 2
FEATURE [Part::Cylinder] Cylinder312
  Angle = 360
  AttacherType = Attacher::AttachEngine3D
  FirstAngle = 0
  Height = 2
  Placement = pos=(-40,0,0) rot=(0,0,1;0rad)
  Radius = 1.65
  SecondAngle = 0
  expr: .Placement.Base.x = <<BreadboardConfig>>.screw_spacing * -8
  expr: Height = <<BreadboardConfig>>.t_plate
  expr: Radius = <<BreadboardConfig>>.screw_corehole / 2
FEATURE [Part::Cylinder] Cylinder313
  Angle = 360
  AttacherType = Attacher::AttachEngine3D
  FirstAngle = 0
  Height = 2
  Placement = pos=(-45,0,0) rot=(0,0,1;0rad)
  Radius = 1.65
  SecondAngle = 0
  expr: .Placement.Base.x = <<BreadboardConfig>>.screw_spacing * -9
  expr: Height = <<BreadboardConfig>>.t_plate
  expr: Radius = <<BreadboardConfig>>.screw_corehole / 2
FEATURE [Part::Cylinder] Cylinder314
  Angle = 360
  AttacherType = Attacher::AttachEngine3D
  FirstAngle = 0
  Height = 2
  Placement = pos=(-50,0,0) rot=(0,0,1;0rad)
  Radius = 1.65
  SecondAngle = 0
  expr: .Placement.Base.x = <<BreadboardConfig>>.screw_spacing * -10
  expr: Height = <<BreadboardConfig>>.t_plate
  expr: Radius = <<BreadboardConfig>>.screw_corehole / 2
FEATURE [Part::Cylinder] Cylinder315
  Angle = 360
  AttacherType = Attacher::AttachEngine3D
  FirstAngle = 0
  Height = 2
  Radius = 1.65
  SecondAngle = 0
  expr: Height = <<BreadboardConfig>>.t_plate
  expr: Radius = <<BreadboardConfig>>.screw_corehole / 2
FEATURE [Part::MultiFuse] Fusion015
  Placement = pos=(0,-20,0) rot=(0,0,1;0rad)
  Shapes = -> [Cylinder314,Cylinder313,Cylinder312,Cylinder311,Cylinder310,Cylinder309,Cylinder308,Cylinder307,Cylinder306,Cylinder305,Cylinder304,Cylinder303,Cylinder302,Cylinder301,Cylinder300,Cylinder299,Cylinder298,Cylinder297,Cylinder296,Cylinder295,Cylinder315]
  expr: .Placement.Base.y = <<BreadboardConfig>>.screw_spacing * -4
FEATURE [Part::Cylinder] Cylinder316
  Angle = 360
  AttacherType = Attacher::AttachEngine3D
  FirstAngle = 0
  Height = 2
  Placement = pos=(5,0,0) rot=(0,0,1;0rad)
  Radius = 1.65
  SecondAngle = 0
  expr: .Placement.Base.x = <<BreadboardConfig>>.screw_spacing * 1
  expr: Height = <<BreadboardConfig>>.t_plate
  expr: Radius = <<BreadboardConfig>>.screw_corehole / 2
FEATURE [Part::Cylinder] Cylinder317
  Angle = 360
  AttacherType = Attacher::AttachEngine3D
  FirstAngle = 0
  Height = 2
  Placement = pos=(10,0,0) rot=(0,0,1;0rad)
  Radius = 1.65
  SecondAngle = 0
  expr: .Placement.Base.x = <<BreadboardConfig>>.screw_spacing * 2
  expr: Height = <<BreadboardConfig>>.t_plate
  expr: Radius = <<BreadboardConfig>>.screw_corehole / 2
FEATURE [Part::Cylinder] Cylinder318
  Angle = 360
  AttacherType = Attacher::AttachEngine3D
  FirstAngle = 0
  Height = 2
  Placement = pos=(15,0,0) rot=(0,0,1;0rad)
  Radius = 1.65
  SecondAngle = 0
  expr: .Placement.Base.x = <<BreadboardConfig>>.screw_spacing * 3
  expr: Height = <<BreadboardConfig>>.t_plate
  expr: Radius = <<BreadboardConfig>>.screw_corehole / 2
FEATURE [Part::Cylinder] Cylinder319
  Angle = 360
  AttacherType = Attacher::AttachEngine3D
  FirstAngle = 0
  Height = 2
  Placement = pos=(20,0,0) rot=(0,0,1;0rad)
  Radius = 1.65
  SecondAngle = 0
  expr: .Placement.Base.x = <<BreadboardConfig>>.screw_spacing * 4
  expr: Height = <<BreadboardConfig>>.t_plate
  expr: Radius = <<BreadboardConfig>>.screw_corehole / 2
FEATURE [Part::Cylinder] Cylinder320
  Angle = 360
  AttacherType = Attacher::AttachEngine3D
  FirstAngle = 0
  Height = 2
  Placement = pos=(25,0,0) rot=(0,0,1;0rad)
  Radius = 1.65
  SecondAngle = 0
  expr: .Placement.Base.x = <<BreadboardConfig>>.screw_spacing * 5
  expr: Height = <<BreadboardConfig>>.t_plate
  expr: Radius = <<BreadboardConfig>>.screw_corehole / 2
FEATURE [Part::Cylinder] Cylinder321
  Angle = 360
  AttacherType = Attacher::AttachEngine3D
  FirstAngle = 0
  Height = 2
  Placement = pos=(30,0,0) rot=(0,0,1;0rad)
  Radius = 1.65
  SecondAngle = 0
  expr: .Placement.Base.x = <<BreadboardConfig>>.screw_spacing * 6
  expr: Height = <<BreadboardConfig>>.t_plate
  expr: Radius = <<BreadboardConfig>>.screw_corehole / 2
FEATURE [Part::Cylinder] Cylinder322
  Angle = 360
  AttacherType = Attacher::AttachEngine3D
  FirstAngle = 0
  Height = 2
  Placement = pos=(35,0,0) rot=(0,0,1;0rad)
  Radius = 1.65
  SecondAngle = 0
  expr: .Placement.Base.x = <<BreadboardConfig>>.screw_spacing * 7
  expr: Height = <<BreadboardConfig>>.t_plate
  expr: Radius = <<BreadboardConfig>>.screw_corehole / 2
FEATURE [Part::Cylinder] Cylinder323
  Angle = 360
  AttacherType = Attacher::AttachEngine3D
  FirstAngle = 0
  Height = 2
  Placement = pos=(40,0,0) rot=(0,0,1;0rad)
  Radius = 1.65
  SecondAngle = 0
  expr: .Placement.Base.x = <<BreadboardConfig>>.screw_spacing * 8
  expr: Height = <<BreadboardConfig>>.t_plate
  expr: Radius = <<BreadboardConfig>>.screw_corehole / 2
FEATURE [Part::Cylinder] Cylinder324
  Angle = 360
  AttacherType = Attacher::AttachEngine3D
  FirstAngle = 0
  Height = 2
  Placement = pos=(45,0,0) rot=(0,0,1;0rad)
  Radius = 1.65
  SecondAngle = 0
  expr: .Placement.Base.x = <<BreadboardConfig>>.screw_spacing * 9
  expr: Height = <<BreadboardConfig>>.t_plate
  expr: Radius = <<BreadboardConfig>>.screw_corehole / 2
FEATURE [Part::Cylinder] Cylinder325
  Angle = 360
  AttacherType = Attacher::AttachEngine3D
  FirstAngle = 0
  Height = 2
  Placement = pos=(50,0,0) rot=(0,0,1;0rad)
  Radius = 1.65
  SecondAngle = 0
  expr: .Placement.Base.x = <<BreadboardConfig>>.screw_spacing * 10
  expr: Height = <<BreadboardConfig>>.t_plate
  expr: Radius = <<BreadboardConfig>>.screw_corehole / 2
FEATURE [Part::Cylinder] Cylinder326
  Angle = 360
  AttacherType = Attacher::AttachEngine3D
  FirstAngle = 0
  Height = 2
  Placement = pos=(-5,0,0) rot=(0,0,1;0rad)
  Radius = 1.65
  SecondAngle = 0
  expr: .Placement.Base.x = <<BreadboardConfig>>.screw_spacing * -1
  expr: Height = <<BreadboardConfig>>.t_plate
  expr: Radius = <<BreadboardConfig>>.screw_corehole / 2
FEATURE [Part::Cylinder] Cylinder327
  Angle = 360
  AttacherType = Attacher::AttachEngine3D
  FirstAngle = 0
  Height = 2
  Placement = pos=(-10,0,0) rot=(0,0,1;0rad)
  Radius = 1.65
  SecondAngle = 0
  expr: .Placement.Base.x = <<BreadboardConfig>>.screw_spacing * -2
  expr: Height = <<BreadboardConfig>>.t_plate
  expr: Radius = <<BreadboardConfig>>.screw_corehole / 2
FEATURE [Part::Cylinder] Cylinder328
  Angle = 360
  AttacherType = Attacher::AttachEngine3D
  FirstAngle = 0
  Height = 2
  Placement = pos=(-15,0,0) rot=(0,0,1;0rad)
  Radius = 1.65
  SecondAngle = 0
  expr: .Placement.Base.x = <<BreadboardConfig>>.screw_spacing * -3
  expr: Height = <<BreadboardConfig>>.t_plate
  expr: Radius = <<BreadboardConfig>>.screw_corehole / 2
FEATURE [Part::Cylinder] Cylinder329
  Angle = 360
  AttacherType = Attacher::AttachEngine3D
  FirstAngle = 0
  Height = 2
  Placement = pos=(-20,0,0) rot=(0,0,1;0rad)
  Radius = 1.65
  SecondAngle = 0
  expr: .Placement.Base.x = <<BreadboardConfig>>.screw_spacing * -4
  expr: Height = <<BreadboardConfig>>.t_plate
  expr: Radius = <<BreadboardConfig>>.screw_corehole / 2
FEATURE [Part::Cylinder] Cylinder330
  Angle = 360
  AttacherType = Attacher::AttachEngine3D
  FirstAngle = 0
  Height = 2
  Placement = pos=(-25,0,0) rot=(0,0,1;0rad)
  Radius = 1.65
  SecondAngle = 0
  expr: .Placement.Base.x = <<BreadboardConfig>>.screw_spacing * -5
  expr: Height = <<BreadboardConfig>>.t_plate
  expr: Radius = <<BreadboardConfig>>.screw_corehole / 2
FEATURE [Part::Cylinder] Cylinder331
  Angle = 360
  AttacherType = Attacher::AttachEngine3D
  FirstAngle = 0
  Height = 2
  Placement = pos=(-30,0,0) rot=(0,0,1;0rad)
  Radius = 1.65
  SecondAngle = 0
  expr: .Placement.Base.x = <<BreadboardConfig>>.screw_spacing * -6
  expr: Height = <<BreadboardConfig>>.t_plate
  expr: Radius = <<BreadboardConfig>>.screw_corehole / 2
FEATURE [Part::Cylinder] Cylinder332
  Angle = 360
  AttacherType = Attacher::AttachEngine3D
  FirstAngle = 0
  Height = 2
  Placement = pos=(-35,0,0) rot=(0,0,1;0rad)
  Radius = 1.65
  SecondAngle = 0
  expr: .Placement.Base.x = <<BreadboardConfig>>.screw_spacing * -7
  expr: Height = <<BreadboardConfig>>.t_plate
  expr: Radius = <<BreadboardConfig>>.screw_corehole / 2
FEATURE [Part::Cylinder] Cylinder333
  Angle = 360
  AttacherType = Attacher::AttachEngine3D
  FirstAngle = 0
  Height = 2
  Placement = pos=(-40,0,0) rot=(0,0,1;0rad)
  Radius = 1.65
  SecondAngle = 0
  expr: .Placement.Base.x = <<BreadboardConfig>>.screw_spacing * -8
  expr: Height = <<BreadboardConfig>>.t_plate
  expr: Radius = <<BreadboardConfig>>.screw_corehole / 2
FEATURE [Part::Cylinder] Cylinder334
  Angle = 360
  AttacherType = Attacher::AttachEngine3D
  FirstAngle = 0
  Height = 2
  Placement = pos=(-45,0,0) rot=(0,0,1;0rad)
  Radius = 1.65
  SecondAngle = 0
  expr: .Placement.Base.x = <<BreadboardConfig>>.screw_spacing * -9
  expr: Height = <<BreadboardConfig>>.t_plate
  expr: Radius = <<BreadboardConfig>>.screw_corehole / 2
FEATURE [Part::Cylinder] Cylinder335
  Angle = 360
  AttacherType = Attacher::AttachEngine3D
  FirstAngle = 0
  Height = 2
  Placement = pos=(-50,0,0) rot=(0,0,1;0rad)
  Radius = 1.65
  SecondAngle = 0
  expr: .Placement.Base.x = <<BreadboardConfig>>.screw_spacing * -10
  expr: Height = <<BreadboardConfig>>.t_plate
  expr: Radius = <<BreadboardConfig>>.screw_corehole / 2
FEATURE [Part::Cylinder] Cylinder336
  Angle = 360
  AttacherType = Attacher::AttachEngine3D
  FirstAngle = 0
  Height = 2
  Radius = 1.65
  SecondAngle = 0
  expr: Height = <<BreadboardConfig>>.t_plate
  expr: Radius = <<BreadboardConfig>>.screw_corehole / 2
FEATURE [Part::MultiFuse] Fusion016
  Placement = pos=(0,-25,0) rot=(0,0,1;0rad)
  Shapes = -> [Cylinder335,Cylinder334,Cylinder333,Cylinder332,Cylinder331,Cylinder330,Cylinder329,Cylinder328,Cylinder327,Cylinder326,Cylinder325,Cylinder324,Cylinder323,Cylinder322,Cylinder321,Cylinder320,Cylinder319,Cylinder318,Cylinder317,Cylinder316,Cylinder336]
  expr: .Placement.Base.y = <<BreadboardConfig>>.screw_spacing * -5
FEATURE [Part::Cylinder] Cylinder337
  Angle = 360
  AttacherType = Attacher::AttachEngine3D
  FirstAngle = 0
  Height = 2
  Placement = pos=(5,0,0) rot=(0,0,1;0rad)
  Radius = 1.65
  SecondAngle = 0
  expr: .Placement.Base.x = <<BreadboardConfig>>.screw_spacing * 1
  expr: Height = <<BreadboardConfig>>.t_plate
  expr: Radius = <<BreadboardConfig>>.screw_corehole / 2
FEATURE [Part::Cylinder] Cylinder338
  Angle = 360
  AttacherType = Attacher::AttachEngine3D
  FirstAngle = 0
  Height = 2
  Placement = pos=(10,0,0) rot=(0,0,1;0rad)
  Radius = 1.65
  SecondAngle = 0
  expr: .Placement.Base.x = <<BreadboardConfig>>.screw_spacing * 2
  expr: Height = <<BreadboardConfig>>.t_plate
  expr: Radius = <<BreadboardConfig>>.screw_corehole / 2
FEATURE [Part::Cylinder] Cylinder339
  Angle = 360
  AttacherType = Attacher::AttachEngine3D
  FirstAngle = 0
  Height = 2
  Placement = pos=(15,0,0) rot=(0,0,1;0rad)
  Radius = 1.65
  SecondAngle = 0
  expr: .Placement.Base.x = <<BreadboardConfig>>.screw_spacing * 3
  expr: Height = <<BreadboardConfig>>.t_plate
  expr: Radius = <<BreadboardConfig>>.screw_corehole / 2
FEATURE [Part::Cylinder] Cylinder340
  Angle = 360
  AttacherType = Attacher::AttachEngine3D
  FirstAngle = 0
  Height = 2
  Placement = pos=(20,0,0) rot=(0,0,1;0rad)
  Radius = 1.65
  SecondAngle = 0
  expr: .Placement.Base.x = <<BreadboardConfig>>.screw_spacing * 4
  expr: Height = <<BreadboardConfig>>.t_plate
  expr: Radius = <<BreadboardConfig>>.screw_corehole / 2
FEATURE [Part::Cylinder] Cylinder341
  Angle = 360
  AttacherType = Attacher::AttachEngine3D
  FirstAngle = 0
  Height = 2
  Placement = pos=(25,0,0) rot=(0,0,1;0rad)
  Radius = 1.65
  SecondAngle = 0
  expr: .Placement.Base.x = <<BreadboardConfig>>.screw_spacing * 5
  expr: Height = <<BreadboardConfig>>.t_plate
  expr: Radius = <<BreadboardConfig>>.screw_corehole / 2
FEATURE [Part::Cylinder] Cylinder342
  Angle = 360
  AttacherType = Attacher::AttachEngine3D
  FirstAngle = 0
  Height = 2
  Placement = pos=(30,0,0) rot=(0,0,1;0rad)
  Radius = 1.65
  SecondAngle = 0
  expr: .Placement.Base.x = <<BreadboardConfig>>.screw_spacing * 6
  expr: Height = <<BreadboardConfig>>.t_plate
  expr: Radius = <<BreadboardConfig>>.screw_corehole / 2
FEATURE [Part::Cylinder] Cylinder343
  Angle = 360
  AttacherType = Attacher::AttachEngine3D
  FirstAngle = 0
  Height = 2
  Placement = pos=(35,0,0) rot=(0,0,1;0rad)
  Radius = 1.65
  SecondAngle = 0
  expr: .Placement.Base.x = <<BreadboardConfig>>.screw_spacing * 7
  expr: Height = <<BreadboardConfig>>.t_plate
  expr: Radius = <<BreadboardConfig>>.screw_corehole / 2
FEATURE [Part::Cylinder] Cylinder344
  Angle = 360
  AttacherType = Attacher::AttachEngine3D
  FirstAngle = 0
  Height = 2
  Placement = pos=(40,0,0) rot=(0,0,1;0rad)
  Radius = 1.65
  SecondAngle = 0
  expr: .Placement.Base.x = <<BreadboardConfig>>.screw_spacing * 8
  expr: Height = <<BreadboardConfig>>.t_plate
  expr: Radius = <<BreadboardConfig>>.screw_corehole / 2
FEATURE [Part::Cylinder] Cylinder345
  Angle = 360
  AttacherType = Attacher::AttachEngine3D
  FirstAngle = 0
  Height = 2
  Placement = pos=(45,0,0) rot=(0,0,1;0rad)
  Radius = 1.65
  SecondAngle = 0
  expr: .Placement.Base.x = <<BreadboardConfig>>.screw_spacing * 9
  expr: Height = <<BreadboardConfig>>.t_plate
  expr: Radius = <<BreadboardConfig>>.screw_corehole / 2
FEATURE [Part::Cylinder] Cylinder346
  Angle = 360
  AttacherType = Attacher::AttachEngine3D
  FirstAngle = 0
  Height = 2
  Placement = pos=(50,0,0) rot=(0,0,1;0rad)
  Radius = 1.65
  SecondAngle = 0
  expr: .Placement.Base.x = <<BreadboardConfig>>.screw_spacing * 10
  expr: Height = <<BreadboardConfig>>.t_plate
  expr: Radius = <<BreadboardConfig>>.screw_corehole / 2
FEATURE [Part::Cylinder] Cylinder347
  Angle = 360
  AttacherType = Attacher::AttachEngine3D
  FirstAngle = 0
  Height = 2
  Placement = pos=(-5,0,0) rot=(0,0,1;0rad)
  Radius = 1.65
  SecondAngle = 0
  expr: .Placement.Base.x = <<BreadboardConfig>>.screw_spacing * -1
  expr: Height = <<BreadboardConfig>>.t_plate
  expr: Radius = <<BreadboardConfig>>.screw_corehole / 2
FEATURE [Part::Cylinder] Cylinder348
  Angle = 360
  AttacherType = Attacher::AttachEngine3D
  FirstAngle = 0
  Height = 2
  Placement = pos=(-10,0,0) rot=(0,0,1;0rad)
  Radius = 1.65
  SecondAngle = 0
  expr: .Placement.Base.x = <<BreadboardConfig>>.screw_spacing * -2
  expr: Height = <<BreadboardConfig>>.t_plate
  expr: Radius = <<BreadboardConfig>>.screw_corehole / 2
FEATURE [Part::Cylinder] Cylinder349
  Angle = 360
  AttacherType = Attacher::AttachEngine3D
  FirstAngle = 0
  Height = 2
  Placement = pos=(-15,0,0) rot=(0,0,1;0rad)
  Radius = 1.65
  SecondAngle = 0
  expr: .Placement.Base.x = <<BreadboardConfig>>.screw_spacing * -3
  expr: Height = <<BreadboardConfig>>.t_plate
  expr: Radius = <<BreadboardConfig>>.screw_corehole / 2
FEATURE [Part::Cylinder] Cylinder350
  Angle = 360
  AttacherType = Attacher::AttachEngine3D
  FirstAngle = 0
  Height = 2
  Placement = pos=(-20,0,0) rot=(0,0,1;0rad)
  Radius = 1.65
  SecondAngle = 0
  expr: .Placement.Base.x = <<BreadboardConfig>>.screw_spacing * -4
  expr: Height = <<BreadboardConfig>>.t_plate
  expr: Radius = <<BreadboardConfig>>.screw_corehole / 2
FEATURE [Part::Cylinder] Cylinder351
  Angle = 360
  AttacherType = Attacher::AttachEngine3D
  FirstAngle = 0
  Height = 2
  Placement = pos=(-25,0,0) rot=(0,0,1;0rad)
  Radius = 1.65
  SecondAngle = 0
  expr: .Placement.Base.x = <<BreadboardConfig>>.screw_spacing * -5
  expr: Height = <<BreadboardConfig>>.t_plate
  expr: Radius = <<BreadboardConfig>>.screw_corehole / 2
FEATURE [Part::Cylinder] Cylinder352
  Angle = 360
  AttacherType = Attacher::AttachEngine3D
  FirstAngle = 0
  Height = 2
  Placement = pos=(-30,0,0) rot=(0,0,1;0rad)
  Radius = 1.65
  SecondAngle = 0
  expr: .Placement.Base.x = <<BreadboardConfig>>.screw_spacing * -6
  expr: Height = <<BreadboardConfig>>.t_plate
  expr: Radius = <<BreadboardConfig>>.screw_corehole / 2
FEATURE [Part::Cylinder] Cylinder353
  Angle = 360
  AttacherType = Attacher::AttachEngine3D
  FirstAngle = 0
  Height = 2
  Placement = pos=(-35,0,0) rot=(0,0,1;0rad)
  Radius = 1.65
  SecondAngle = 0
  expr: .Placement.Base.x = <<BreadboardConfig>>.screw_spacing * -7
  expr: Height = <<BreadboardConfig>>.t_plate
  expr: Radius = <<BreadboardConfig>>.screw_corehole / 2
FEATURE [Part::Cylinder] Cylinder354
  Angle = 360
  AttacherType = Attacher::AttachEngine3D
  FirstAngle = 0
  Height = 2
  Placement = pos=(-40,0,0) rot=(0,0,1;0rad)
  Radius = 1.65
  SecondAngle = 0
  expr: .Placement.Base.x = <<BreadboardConfig>>.screw_spacing * -8
  expr: Height = <<BreadboardConfig>>.t_plate
  expr: Radius = <<BreadboardConfig>>.screw_corehole / 2
FEATURE [Part::Cylinder] Cylinder355
  Angle = 360
  AttacherType = Attacher::AttachEngine3D
  FirstAngle = 0
  Height = 2
  Placement = pos=(-45,0,0) rot=(0,0,1;0rad)
  Radius = 1.65
  SecondAngle = 0
  expr: .Placement.Base.x = <<BreadboardConfig>>.screw_spacing * -9
  expr: Height = <<BreadboardConfig>>.t_plate
  expr: Radius = <<BreadboardConfig>>.screw_corehole / 2
FEATURE [Part::Cylinder] Cylinder356
  Angle = 360
  AttacherType = Attacher::AttachEngine3D
  FirstAngle = 0
  Height = 2
  Placement = pos=(-50,0,0) rot=(0,0,1;0rad)
  Radius = 1.65
  SecondAngle = 0
  expr: .Placement.Base.x = <<BreadboardConfig>>.screw_spacing * -10
  expr: Height = <<BreadboardConfig>>.t_plate
  expr: Radius = <<BreadboardConfig>>.screw_corehole / 2
FEATURE [Part::Cylinder] Cylinder357
  Angle = 360
  AttacherType = Attacher::AttachEngine3D
  FirstAngle = 0
  Height = 2
  Radius = 1.65
  SecondAngle = 0
  expr: Height = <<BreadboardConfig>>.t_plate
  expr: Radius = <<BreadboardConfig>>.screw_corehole / 2
FEATURE [Part::MultiFuse] Fusion017
  Placement = pos=(0,-30,0) rot=(0,0,1;0rad)
  Shapes = -> [Cylinder356,Cylinder355,Cylinder354,Cylinder353,Cylinder352,Cylinder351,Cylinder350,Cylinder349,Cylinder348,Cylinder347,Cylinder346,Cylinder345,Cylinder344,Cylinder343,Cylinder342,Cylinder341,Cylinder340,Cylinder339,Cylinder338,Cylinder337,Cylinder357]
  expr: .Placement.Base.y = <<BreadboardConfig>>.screw_spacing * -6
FEATURE [Part::Cylinder] Cylinder358
  Angle = 360
  AttacherType = Attacher::AttachEngine3D
  FirstAngle = 0
  Height = 2
  Placement = pos=(5,0,0) rot=(0,0,1;0rad)
  Radius = 1.65
  SecondAngle = 0
  expr: .Placement.Base.x = <<BreadboardConfig>>.screw_spacing * 1
  expr: Height = <<BreadboardConfig>>.t_plate
  expr: Radius = <<BreadboardConfig>>.screw_corehole / 2
FEATURE [Part::Cylinder] Cylinder359
  Angle = 360
  AttacherType = Attacher::AttachEngine3D
  FirstAngle = 0
  Height = 2
  Placement = pos=(10,0,0) rot=(0,0,1;0rad)
  Radius = 1.65
  SecondAngle = 0
  expr: .Placement.Base.x = <<BreadboardConfig>>.screw_spacing * 2
  expr: Height = <<BreadboardConfig>>.t_plate
  expr: Radius = <<BreadboardConfig>>.screw_corehole / 2
FEATURE [Part::Cylinder] Cylinder360
  Angle = 360
  AttacherType = Attacher::AttachEngine3D
  FirstAngle = 0
  Height = 2
  Placement = pos=(15,0,0) rot=(0,0,1;0rad)
  Radius = 1.65
  SecondAngle = 0
  expr: .Placement.Base.x = <<BreadboardConfig>>.screw_spacing * 3
  expr: Height = <<BreadboardConfig>>.t_plate
  expr: Radius = <<BreadboardConfig>>.screw_corehole / 2
FEATURE [Part::Cylinder] Cylinder361
  Angle = 360
  AttacherType = Attacher::AttachEngine3D
  FirstAngle = 0
  Height = 2
  Placement = pos=(20,0,0) rot=(0,0,1;0rad)
  Radius = 1.65
  SecondAngle = 0
  expr: .Placement.Base.x = <<BreadboardConfig>>.screw_spacing * 4
  expr: Height = <<BreadboardConfig>>.t_plate
  expr: Radius = <<BreadboardConfig>>.screw_corehole / 2
FEATURE [Part::Cylinder] Cylinder362
  Angle = 360
  AttacherType = Attacher::AttachEngine3D
  FirstAngle = 0
  Height = 2
  Placement = pos=(25,0,0) rot=(0,0,1;0rad)
  Radius = 1.65
  SecondAngle = 0
  expr: .Placement.Base.x = <<BreadboardConfig>>.screw_spacing * 5
  expr: Height = <<BreadboardConfig>>.t_plate
  expr: Radius = <<BreadboardConfig>>.screw_corehole / 2
FEATURE [Part::Cylinder] Cylinder363
  Angle = 360
  AttacherType = Attacher::AttachEngine3D
  FirstAngle = 0
  Height = 2
  Placement = pos=(30,0,0) rot=(0,0,1;0rad)
  Radius = 1.65
  SecondAngle = 0
  expr: .Placement.Base.x = <<BreadboardConfig>>.screw_spacing * 6
  expr: Height = <<BreadboardConfig>>.t_plate
  expr: Radius = <<BreadboardConfig>>.screw_corehole / 2
FEATURE [Part::Cylinder] Cylinder364
  Angle = 360
  AttacherType = Attacher::AttachEngine3D
  FirstAngle = 0
  Height = 2
  Placement = pos=(35,0,0) rot=(0,0,1;0rad)
  Radius = 1.65
  SecondAngle = 0
  expr: .Placement.Base.x = <<BreadboardConfig>>.screw_spacing * 7
  expr: Height = <<BreadboardConfig>>.t_plate
  expr: Radius = <<BreadboardConfig>>.screw_corehole / 2
FEATURE [Part::Cylinder] Cylinder365
  Angle = 360
  AttacherType = Attacher::AttachEngine3D
  FirstAngle = 0
  Height = 2
  Placement = pos=(40,0,0) rot=(0,0,1;0rad)
  Radius = 1.65
  SecondAngle = 0
  expr: .Placement.Base.x = <<BreadboardConfig>>.screw_spacing * 8
  expr: Height = <<BreadboardConfig>>.t_plate
  expr: Radius = <<BreadboardConfig>>.screw_corehole / 2
FEATURE [Part::Cylinder] Cylinder366
  Angle = 360
  AttacherType = Attacher::AttachEngine3D
  FirstAngle = 0
  Height = 2
  Placement = pos=(45,0,0) rot=(0,0,1;0rad)
  Radius = 1.65
  SecondAngle = 0
  expr: .Placement.Base.x = <<BreadboardConfig>>.screw_spacing * 9
  expr: Height = <<BreadboardConfig>>.t_plate
  expr: Radius = <<BreadboardConfig>>.screw_corehole / 2
FEATURE [Part::Cylinder] Cylinder367
  Angle = 360
  AttacherType = Attacher::AttachEngine3D
  FirstAngle = 0
  Height = 2
  Placement = pos=(50,0,0) rot=(0,0,1;0rad)
  Radius = 1.65
  SecondAngle = 0
  expr: .Placement.Base.x = <<BreadboardConfig>>.screw_spacing * 10
  expr: Height = <<BreadboardConfig>>.t_plate
  expr: Radius = <<BreadboardConfig>>.screw_corehole / 2
FEATURE [Part::Cylinder] Cylinder368
  Angle = 360
  AttacherType = Attacher::AttachEngine3D
  FirstAngle = 0
  Height = 2
  Placement = pos=(-5,0,0) rot=(0,0,1;0rad)
  Radius = 1.65
  SecondAngle = 0
  expr: .Placement.Base.x = <<BreadboardConfig>>.screw_spacing * -1
  expr: Height = <<BreadboardConfig>>.t_plate
  expr: Radius = <<BreadboardConfig>>.screw_corehole / 2
FEATURE [Part::Cylinder] Cylinder369
  Angle = 360
  AttacherType = Attacher::AttachEngine3D
  FirstAngle = 0
  Height = 2
  Placement = pos=(-10,0,0) rot=(0,0,1;0rad)
  Radius = 1.65
  SecondAngle = 0
  expr: .Placement.Base.x = <<BreadboardConfig>>.screw_spacing * -2
  expr: Height = <<BreadboardConfig>>.t_plate
  expr: Radius = <<BreadboardConfig>>.screw_corehole / 2
FEATURE [Part::Cylinder] Cylinder370
  Angle = 360
  AttacherType = Attacher::AttachEngine3D
  FirstAngle = 0
  Height = 2
  Placement = pos=(-15,0,0) rot=(0,0,1;0rad)
  Radius = 1.65
  SecondAngle = 0
  expr: .Placement.Base.x = <<BreadboardConfig>>.screw_spacing * -3
  expr: Height = <<BreadboardConfig>>.t_plate
  expr: Radius = <<BreadboardConfig>>.screw_corehole / 2
FEATURE [Part::Cylinder] Cylinder371
  Angle = 360
  AttacherType = Attacher::AttachEngine3D
  FirstAngle = 0
  Height = 2
  Placement = pos=(-20,0,0) rot=(0,0,1;0rad)
  Radius = 1.65
  SecondAngle = 0
  expr: .Placement.Base.x = <<BreadboardConfig>>.screw_spacing * -4
  expr: Height = <<BreadboardConfig>>.t_plate
  expr: Radius = <<BreadboardConfig>>.screw_corehole / 2
FEATURE [Part::Cylinder] Cylinder372
  Angle = 360
  AttacherType = Attacher::AttachEngine3D
  FirstAngle = 0
  Height = 2
  Placement = pos=(-25,0,0) rot=(0,0,1;0rad)
  Radius = 1.65
  SecondAngle = 0
  expr: .Placement.Base.x = <<BreadboardConfig>>.screw_spacing * -5
  expr: Height = <<BreadboardConfig>>.t_plate
  expr: Radius = <<BreadboardConfig>>.screw_corehole / 2
FEATURE [Part::Cylinder] Cylinder373
  Angle = 360
  AttacherType = Attacher::AttachEngine3D
  FirstAngle = 0
  Height = 2
  Placement = pos=(-30,0,0) rot=(0,0,1;0rad)
  Radius = 1.65
  SecondAngle = 0
  expr: .Placement.Base.x = <<BreadboardConfig>>.screw_spacing * -6
  expr: Height = <<BreadboardConfig>>.t_plate
  expr: Radius = <<BreadboardConfig>>.screw_corehole / 2
FEATURE [Part::Cylinder] Cylinder374
  Angle = 360
  AttacherType = Attacher::AttachEngine3D
  FirstAngle = 0
  Height = 2
  Placement = pos=(-35,0,0) rot=(0,0,1;0rad)
  Radius = 1.65
  SecondAngle = 0
  expr: .Placement.Base.x = <<BreadboardConfig>>.screw_spacing * -7
  expr: Height = <<BreadboardConfig>>.t_plate
  expr: Radius = <<BreadboardConfig>>.screw_corehole / 2
FEATURE [Part::Cylinder] Cylinder375
  Angle = 360
  AttacherType = Attacher::AttachEngine3D
  FirstAngle = 0
  Height = 2
  Placement = pos=(-40,0,0) rot=(0,0,1;0rad)
  Radius = 1.65
  SecondAngle = 0
  expr: .Placement.Base.x = <<BreadboardConfig>>.screw_spacing * -8
  expr: Height = <<BreadboardConfig>>.t_plate
  expr: Radius = <<BreadboardConfig>>.screw_corehole / 2
FEATURE [Part::Cylinder] Cylinder376
  Angle = 360
  AttacherType = Attacher::AttachEngine3D
  FirstAngle = 0
  Height = 2
  Placement = pos=(-45,0,0) rot=(0,0,1;0rad)
  Radius = 1.65
  SecondAngle = 0
  expr: .Placement.Base.x = <<BreadboardConfig>>.screw_spacing * -9
  expr: Height = <<BreadboardConfig>>.t_plate
  expr: Radius = <<BreadboardConfig>>.screw_corehole / 2
FEATURE [Part::Cylinder] Cylinder377
  Angle = 360
  AttacherType = Attacher::AttachEngine3D
  FirstAngle = 0
  Height = 2
  Placement = pos=(-50,0,0) rot=(0,0,1;0rad)
  Radius = 1.65
  SecondAngle = 0
  expr: .Placement.Base.x = <<BreadboardConfig>>.screw_spacing * -10
  expr: Height = <<BreadboardConfig>>.t_plate
  expr: Radius = <<BreadboardConfig>>.screw_corehole / 2
FEATURE [Part::Cylinder] Cylinder378
  Angle = 360
  AttacherType = Attacher::AttachEngine3D
  FirstAngle = 0
  Height = 2
  Radius = 1.65
  SecondAngle = 0
  expr: Height = <<BreadboardConfig>>.t_plate
  expr: Radius = <<BreadboardConfig>>.screw_corehole / 2
FEATURE [Part::MultiFuse] Fusion018
  Placement = pos=(0,-40,0) rot=(0,0,1;0rad)
  Shapes = -> [Cylinder377,Cylinder376,Cylinder375,Cylinder374,Cylinder373,Cylinder372,Cylinder371,Cylinder370,Cylinder369,Cylinder368,Cylinder367,Cylinder366,Cylinder365,Cylinder364,Cylinder363,Cylinder362,Cylinder361,Cylinder360,Cylinder359,Cylinder358,Cylinder378]
  expr: .Placement.Base.y = <<BreadboardConfig>>.screw_spacing * -8
FEATURE [Part::Cylinder] Cylinder379
  Angle = 360
  AttacherType = Attacher::AttachEngine3D
  FirstAngle = 0
  Height = 2
  Placement = pos=(5,0,0) rot=(0,0,1;0rad)
  Radius = 1.65
  SecondAngle = 0
  expr: .Placement.Base.x = <<BreadboardConfig>>.screw_spacing * 1
  expr: Height = <<BreadboardConfig>>.t_plate
  expr: Radius = <<BreadboardConfig>>.screw_corehole / 2
FEATURE [Part::Cylinder] Cylinder380
  Angle = 360
  AttacherType = Attacher::AttachEngine3D
  FirstAngle = 0
  Height = 2
  Placement = pos=(10,0,0) rot=(0,0,1;0rad)
  Radius = 1.65
  SecondAngle = 0
  expr: .Placement.Base.x = <<BreadboardConfig>>.screw_spacing * 2
  expr: Height = <<BreadboardConfig>>.t_plate
  expr: Radius = <<BreadboardConfig>>.screw_corehole / 2
FEATURE [Part::Cylinder] Cylinder381
  Angle = 360
  AttacherType = Attacher::AttachEngine3D
  FirstAngle = 0
  Height = 2
  Placement = pos=(15,0,0) rot=(0,0,1;0rad)
  Radius = 1.65
  SecondAngle = 0
  expr: .Placement.Base.x = <<BreadboardConfig>>.screw_spacing * 3
  expr: Height = <<BreadboardConfig>>.t_plate
  expr: Radius = <<BreadboardConfig>>.screw_corehole / 2
FEATURE [Part::Cylinder] Cylinder382
  Angle = 360
  AttacherType = Attacher::AttachEngine3D
  FirstAngle = 0
  Height = 2
  Placement = pos=(20,0,0) rot=(0,0,1;0rad)
  Radius = 1.65
  SecondAngle = 0
  expr: .Placement.Base.x = <<BreadboardConfig>>.screw_spacing * 4
  expr: Height = <<BreadboardConfig>>.t_plate
  expr: Radius = <<BreadboardConfig>>.screw_corehole / 2
FEATURE [Part::Cylinder] Cylinder383
  Angle = 360
  AttacherType = Attacher::AttachEngine3D
  FirstAngle = 0
  Height = 2
  Placement = pos=(25,0,0) rot=(0,0,1;0rad)
  Radius = 1.65
  SecondAngle = 0
  expr: .Placement.Base.x = <<BreadboardConfig>>.screw_spacing * 5
  expr: Height = <<BreadboardConfig>>.t_plate
  expr: Radius = <<BreadboardConfig>>.screw_corehole / 2
FEATURE [Part::Cylinder] Cylinder384
  Angle = 360
  AttacherType = Attacher::AttachEngine3D
  FirstAngle = 0
  Height = 2
  Placement = pos=(30,0,0) rot=(0,0,1;0rad)
  Radius = 1.65
  SecondAngle = 0
  expr: .Placement.Base.x = <<BreadboardConfig>>.screw_spacing * 6
  expr: Height = <<BreadboardConfig>>.t_plate
  expr: Radius = <<BreadboardConfig>>.screw_corehole / 2
FEATURE [Part::Cylinder] Cylinder385
  Angle = 360
  AttacherType = Attacher::AttachEngine3D
  FirstAngle = 0
  Height = 2
  Placement = pos=(35,0,0) rot=(0,0,1;0rad)
  Radius = 1.65
  SecondAngle = 0
  expr: .Placement.Base.x = <<BreadboardConfig>>.screw_spacing * 7
  expr: Height = <<BreadboardConfig>>.t_plate
  expr: Radius = <<BreadboardConfig>>.screw_corehole / 2
FEATURE [Part::Cylinder] Cylinder386
  Angle = 360
  AttacherType = Attacher::AttachEngine3D
  FirstAngle = 0
  Height = 2
  Placement = pos=(40,0,0) rot=(0,0,1;0rad)
  Radius = 1.65
  SecondAngle = 0
  expr: .Placement.Base.x = <<BreadboardConfig>>.screw_spacing * 8
  expr: Height = <<BreadboardConfig>>.t_plate
  expr: Radius = <<BreadboardConfig>>.screw_corehole / 2
FEATURE [Part::Cylinder] Cylinder387
  Angle = 360
  AttacherType = Attacher::AttachEngine3D
  FirstAngle = 0
  Height = 2
  Placement = pos=(45,0,0) rot=(0,0,1;0rad)
  Radius = 1.65
  SecondAngle = 0
  expr: .Placement.Base.x = <<BreadboardConfig>>.screw_spacing * 9
  expr: Height = <<BreadboardConfig>>.t_plate
  expr: Radius = <<BreadboardConfig>>.screw_corehole / 2
FEATURE [Part::Cylinder] Cylinder388
  Angle = 360
  AttacherType = Attacher::AttachEngine3D
  FirstAngle = 0
  Height = 2
  Placement = pos=(50,0,0) rot=(0,0,1;0rad)
  Radius = 1.65
  SecondAngle = 0
  expr: .Placement.Base.x = <<BreadboardConfig>>.screw_spacing * 10
  expr: Height = <<BreadboardConfig>>.t_plate
  expr: Radius = <<BreadboardConfig>>.screw_corehole / 2
FEATURE [Part::Cylinder] Cylinder389
  Angle = 360
  AttacherType = Attacher::AttachEngine3D
  FirstAngle = 0
  Height = 2
  Placement = pos=(-5,0,0) rot=(0,0,1;0rad)
  Radius = 1.65
  SecondAngle = 0
  expr: .Placement.Base.x = <<BreadboardConfig>>.screw_spacing * -1
  expr: Height = <<BreadboardConfig>>.t_plate
  expr: Radius = <<BreadboardConfig>>.screw_corehole / 2
FEATURE [Part::Cylinder] Cylinder390
  Angle = 360
  AttacherType = Attacher::AttachEngine3D
  FirstAngle = 0
  Height = 2
  Placement = pos=(-10,0,0) rot=(0,0,1;0rad)
  Radius = 1.65
  SecondAngle = 0
  expr: .Placement.Base.x = <<BreadboardConfig>>.screw_spacing * -2
  expr: Height = <<BreadboardConfig>>.t_plate
  expr: Radius = <<BreadboardConfig>>.screw_corehole / 2
FEATURE [Part::Cylinder] Cylinder391
  Angle = 360
  AttacherType = Attacher::AttachEngine3D
  FirstAngle = 0
  Height = 2
  Placement = pos=(-15,0,0) rot=(0,0,1;0rad)
  Radius = 1.65
  SecondAngle = 0
  expr: .Placement.Base.x = <<BreadboardConfig>>.screw_spacing * -3
  expr: Height = <<BreadboardConfig>>.t_plate
  expr: Radius = <<BreadboardConfig>>.screw_corehole / 2
FEATURE [Part::Cylinder] Cylinder392
  Angle = 360
  AttacherType = Attacher::AttachEngine3D
  FirstAngle = 0
  Height = 2
  Placement = pos=(-20,0,0) rot=(0,0,1;0rad)
  Radius = 1.65
  SecondAngle = 0
  expr: .Placement.Base.x = <<BreadboardConfig>>.screw_spacing * -4
  expr: Height = <<BreadboardConfig>>.t_plate
  expr: Radius = <<BreadboardConfig>>.screw_corehole / 2
FEATURE [Part::Cylinder] Cylinder393
  Angle = 360
  AttacherType = Attacher::AttachEngine3D
  FirstAngle = 0
  Height = 2
  Placement = pos=(-25,0,0) rot=(0,0,1;0rad)
  Radius = 1.65
  SecondAngle = 0
  expr: .Placement.Base.x = <<BreadboardConfig>>.screw_spacing * -5
  expr: Height = <<BreadboardConfig>>.t_plate
  expr: Radius = <<BreadboardConfig>>.screw_corehole / 2
FEATURE [Part::Cylinder] Cylinder394
  Angle = 360
  AttacherType = Attacher::AttachEngine3D
  FirstAngle = 0
  Height = 2
  Placement = pos=(-30,0,0) rot=(0,0,1;0rad)
  Radius = 1.65
  SecondAngle = 0
  expr: .Placement.Base.x = <<BreadboardConfig>>.screw_spacing * -6
  expr: Height = <<BreadboardConfig>>.t_plate
  expr: Radius = <<BreadboardConfig>>.screw_corehole / 2
FEATURE [Part::Cylinder] Cylinder395
  Angle = 360
  AttacherType = Attacher::AttachEngine3D
  FirstAngle = 0
  Height = 2
  Placement = pos=(-35,0,0) rot=(0,0,1;0rad)
  Radius = 1.65
  SecondAngle = 0
  expr: .Placement.Base.x = <<BreadboardConfig>>.screw_spacing * -7
  expr: Height = <<BreadboardConfig>>.t_plate
  expr: Radius = <<BreadboardConfig>>.screw_corehole / 2
FEATURE [Part::Cylinder] Cylinder396
  Angle = 360
  AttacherType = Attacher::AttachEngine3D
  FirstAngle = 0
  Height = 2
  Placement = pos=(-40,0,0) rot=(0,0,1;0rad)
  Radius = 1.65
  SecondAngle = 0
  expr: .Placement.Base.x = <<BreadboardConfig>>.screw_spacing * -8
  expr: Height = <<BreadboardConfig>>.t_plate
  expr: Radius = <<BreadboardConfig>>.screw_corehole / 2
FEATURE [Part::Cylinder] Cylinder397
  Angle = 360
  AttacherType = Attacher::AttachEngine3D
  FirstAngle = 0
  Height = 2
  Placement = pos=(-45,0,0) rot=(0,0,1;0rad)
  Radius = 1.65
  SecondAngle = 0
  expr: .Placement.Base.x = <<BreadboardConfig>>.screw_spacing * -9
  expr: Height = <<BreadboardConfig>>.t_plate
  expr: Radius = <<BreadboardConfig>>.screw_corehole / 2
FEATURE [Part::Cylinder] Cylinder398
  Angle = 360
  AttacherType = Attacher::AttachEngine3D
  FirstAngle = 0
  Height = 2
  Placement = pos=(-50,0,0) rot=(0,0,1;0rad)
  Radius = 1.65
  SecondAngle = 0
  expr: .Placement.Base.x = <<BreadboardConfig>>.screw_spacing * -10
  expr: Height = <<BreadboardConfig>>.t_plate
  expr: Radius = <<BreadboardConfig>>.screw_corehole / 2
FEATURE [Part::Cylinder] Cylinder399
  Angle = 360
  AttacherType = Attacher::AttachEngine3D
  FirstAngle = 0
  Height = 2
  Radius = 1.65
  SecondAngle = 0
  expr: Height = <<BreadboardConfig>>.t_plate
  expr: Radius = <<BreadboardConfig>>.screw_corehole / 2
FEATURE [Part::MultiFuse] Fusion019
  Placement = pos=(0,-45,0) rot=(0,0,1;0rad)
  Shapes = -> [Cylinder398,Cylinder397,Cylinder396,Cylinder395,Cylinder394,Cylinder393,Cylinder392,Cylinder391,Cylinder390,Cylinder389,Cylinder388,Cylinder387,Cylinder386,Cylinder385,Cylinder384,Cylinder383,Cylinder382,Cylinder381,Cylinder380,Cylinder379,Cylinder399]
  expr: .Placement.Base.y = <<BreadboardConfig>>.screw_spacing * -9
FEATURE [Part::Cylinder] Cylinder400
  Angle = 360
  AttacherType = Attacher::AttachEngine3D
  FirstAngle = 0
  Height = 2
  Placement = pos=(5,0,0) rot=(0,0,1;0rad)
  Radius = 1.65
  SecondAngle = 0
  expr: .Placement.Base.x = <<BreadboardConfig>>.screw_spacing * 1
  expr: Height = <<BreadboardConfig>>.t_plate
  expr: Radius = <<BreadboardConfig>>.screw_corehole / 2
FEATURE [Part::Cylinder] Cylinder401
  Angle = 360
  AttacherType = Attacher::AttachEngine3D
  FirstAngle = 0
  Height = 2
  Placement = pos=(10,0,0) rot=(0,0,1;0rad)
  Radius = 1.65
  SecondAngle = 0
  expr: .Placement.Base.x = <<BreadboardConfig>>.screw_spacing * 2
  expr: Height = <<BreadboardConfig>>.t_plate
  expr: Radius = <<BreadboardConfig>>.screw_corehole / 2
FEATURE [Part::Cylinder] Cylinder402
  Angle = 360
  AttacherType = Attacher::AttachEngine3D
  FirstAngle = 0
  Height = 2
  Placement = pos=(15,0,0) rot=(0,0,1;0rad)
  Radius = 1.65
  SecondAngle = 0
  expr: .Placement.Base.x = <<BreadboardConfig>>.screw_spacing * 3
  expr: Height = <<BreadboardConfig>>.t_plate
  expr: Radius = <<BreadboardConfig>>.screw_corehole / 2
FEATURE [Part::Cylinder] Cylinder403
  Angle = 360
  AttacherType = Attacher::AttachEngine3D
  FirstAngle = 0
  Height = 2
  Placement = pos=(20,0,0) rot=(0,0,1;0rad)
  Radius = 1.65
  SecondAngle = 0
  expr: .Placement.Base.x = <<BreadboardConfig>>.screw_spacing * 4
  expr: Height = <<BreadboardConfig>>.t_plate
  expr: Radius = <<BreadboardConfig>>.screw_corehole / 2
FEATURE [Part::Cylinder] Cylinder404
  Angle = 360
  AttacherType = Attacher::AttachEngine3D
  FirstAngle = 0
  Height = 2
  Placement = pos=(25,0,0) rot=(0,0,1;0rad)
  Radius = 1.65
  SecondAngle = 0
  expr: .Placement.Base.x = <<BreadboardConfig>>.screw_spacing * 5
  expr: Height = <<BreadboardConfig>>.t_plate
  expr: Radius = <<BreadboardConfig>>.screw_corehole / 2
FEATURE [Part::Cylinder] Cylinder405
  Angle = 360
  AttacherType = Attacher::AttachEngine3D
  FirstAngle = 0
  Height = 2
  Placement = pos=(30,0,0) rot=(0,0,1;0rad)
  Radius = 1.65
  SecondAngle = 0
  expr: .Placement.Base.x = <<BreadboardConfig>>.screw_spacing * 6
  expr: Height = <<BreadboardConfig>>.t_plate
  expr: Radius = <<BreadboardConfig>>.screw_corehole / 2
FEATURE [Part::Cylinder] Cylinder406
  Angle = 360
  AttacherType = Attacher::AttachEngine3D
  FirstAngle = 0
  Height = 2
  Placement = pos=(35,0,0) rot=(0,0,1;0rad)
  Radius = 1.65
  SecondAngle = 0
  expr: .Placement.Base.x = <<BreadboardConfig>>.screw_spacing * 7
  expr: Height = <<BreadboardConfig>>.t_plate
  expr: Radius = <<BreadboardConfig>>.screw_corehole / 2
FEATURE [Part::Cylinder] Cylinder407
  Angle = 360
  AttacherType = Attacher::AttachEngine3D
  FirstAngle = 0
  Height = 2
  Placement = pos=(40,0,0) rot=(0,0,1;0rad)
  Radius = 1.65
  SecondAngle = 0
  expr: .Placement.Base.x = <<BreadboardConfig>>.screw_spacing * 8
  expr: Height = <<BreadboardConfig>>.t_plate
  expr: Radius = <<BreadboardConfig>>.screw_corehole / 2
FEATURE [Part::Cylinder] Cylinder408
  Angle = 360
  AttacherType = Attacher::AttachEngine3D
  FirstAngle = 0
  Height = 2
  Placement = pos=(45,0,0) rot=(0,0,1;0rad)
  Radius = 1.65
  SecondAngle = 0
  expr: .Placement.Base.x = <<BreadboardConfig>>.screw_spacing * 9
  expr: Height = <<BreadboardConfig>>.t_plate
  expr: Radius = <<BreadboardConfig>>.screw_corehole / 2
FEATURE [Part::Cylinder] Cylinder409
  Angle = 360
  AttacherType = Attacher::AttachEngine3D
  FirstAngle = 0
  Height = 2
  Placement = pos=(50,0,0) rot=(0,0,1;0rad)
  Radius = 1.65
  SecondAngle = 0
  expr: .Placement.Base.x = <<BreadboardConfig>>.screw_spacing * 10
  expr: Height = <<BreadboardConfig>>.t_plate
  expr: Radius = <<BreadboardConfig>>.screw_corehole / 2
FEATURE [Part::Cylinder] Cylinder410
  Angle = 360
  AttacherType = Attacher::AttachEngine3D
  FirstAngle = 0
  Height = 2
  Placement = pos=(-5,0,0) rot=(0,0,1;0rad)
  Radius = 1.65
  SecondAngle = 0
  expr: .Placement.Base.x = <<BreadboardConfig>>.screw_spacing * -1
  expr: Height = <<BreadboardConfig>>.t_plate
  expr: Radius = <<BreadboardConfig>>.screw_corehole / 2
FEATURE [Part::Cylinder] Cylinder411
  Angle = 360
  AttacherType = Attacher::AttachEngine3D
  FirstAngle = 0
  Height = 2
  Placement = pos=(-10,0,0) rot=(0,0,1;0rad)
  Radius = 1.65
  SecondAngle = 0
  expr: .Placement.Base.x = <<BreadboardConfig>>.screw_spacing * -2
  expr: Height = <<BreadboardConfig>>.t_plate
  expr: Radius = <<BreadboardConfig>>.screw_corehole / 2
FEATURE [Part::Cylinder] Cylinder412
  Angle = 360
  AttacherType = Attacher::AttachEngine3D
  FirstAngle = 0
  Height = 2
  Placement = pos=(-15,0,0) rot=(0,0,1;0rad)
  Radius = 1.65
  SecondAngle = 0
  expr: .Placement.Base.x = <<BreadboardConfig>>.screw_spacing * -3
  expr: Height = <<BreadboardConfig>>.t_plate
  expr: Radius = <<BreadboardConfig>>.screw_corehole / 2
FEATURE [Part::Cylinder] Cylinder413
  Angle = 360
  AttacherType = Attacher::AttachEngine3D
  FirstAngle = 0
  Height = 2
  Placement = pos=(-20,0,0) rot=(0,0,1;0rad)
  Radius = 1.65
  SecondAngle = 0
  expr: .Placement.Base.x = <<BreadboardConfig>>.screw_spacing * -4
  expr: Height = <<BreadboardConfig>>.t_plate
  expr: Radius = <<BreadboardConfig>>.screw_corehole / 2
FEATURE [Part::Cylinder] Cylinder414
  Angle = 360
  AttacherType = Attacher::AttachEngine3D
  FirstAngle = 0
  Height = 2
  Placement = pos=(-25,0,0) rot=(0,0,1;0rad)
  Radius = 1.65
  SecondAngle = 0
  expr: .Placement.Base.x = <<BreadboardConfig>>.screw_spacing * -5
  expr: Height = <<BreadboardConfig>>.t_plate
  expr: Radius = <<BreadboardConfig>>.screw_corehole / 2
FEATURE [Part::Cylinder] Cylinder415
  Angle = 360
  AttacherType = Attacher::AttachEngine3D
  FirstAngle = 0
  Height = 2
  Placement = pos=(-30,0,0) rot=(0,0,1;0rad)
  Radius = 1.65
  SecondAngle = 0
  expr: .Placement.Base.x = <<BreadboardConfig>>.screw_spacing * -6
  expr: Height = <<BreadboardConfig>>.t_plate
  expr: Radius = <<BreadboardConfig>>.screw_corehole / 2
FEATURE [Part::Cylinder] Cylinder416
  Angle = 360
  AttacherType = Attacher::AttachEngine3D
  FirstAngle = 0
  Height = 2
  Placement = pos=(-35,0,0) rot=(0,0,1;0rad)
  Radius = 1.65
  SecondAngle = 0
  expr: .Placement.Base.x = <<BreadboardConfig>>.screw_spacing * -7
  expr: Height = <<BreadboardConfig>>.t_plate
  expr: Radius = <<BreadboardConfig>>.screw_corehole / 2
FEATURE [Part::Cylinder] Cylinder417
  Angle = 360
  AttacherType = Attacher::AttachEngine3D
  FirstAngle = 0
  Height = 2
  Placement = pos=(-40,0,0) rot=(0,0,1;0rad)
  Radius = 1.65
  SecondAngle = 0
  expr: .Placement.Base.x = <<BreadboardConfig>>.screw_spacing * -8
  expr: Height = <<BreadboardConfig>>.t_plate
  expr: Radius = <<BreadboardConfig>>.screw_corehole / 2
FEATURE [Part::Cylinder] Cylinder418
  Angle = 360
  AttacherType = Attacher::AttachEngine3D
  FirstAngle = 0
  Height = 2
  Placement = pos=(-45,0,0) rot=(0,0,1;0rad)
  Radius = 1.65
  SecondAngle = 0
  expr: .Placement.Base.x = <<BreadboardConfig>>.screw_spacing * -9
  expr: Height = <<BreadboardConfig>>.t_plate
  expr: Radius = <<BreadboardConfig>>.screw_corehole / 2
FEATURE [Part::Cylinder] Cylinder419
  Angle = 360
  AttacherType = Attacher::AttachEngine3D
  FirstAngle = 0
  Height = 2
  Placement = pos=(-50,0,0) rot=(0,0,1;0rad)
  Radius = 1.65
  SecondAngle = 0
  expr: .Placement.Base.x = <<BreadboardConfig>>.screw_spacing * -10
  expr: Height = <<BreadboardConfig>>.t_plate
  expr: Radius = <<BreadboardConfig>>.screw_corehole / 2
FEATURE [Part::Cylinder] Cylinder420
  Angle = 360
  AttacherType = Attacher::AttachEngine3D
  FirstAngle = 0
  Height = 2
  Radius = 1.65
  SecondAngle = 0
  expr: Height = <<BreadboardConfig>>.t_plate
  expr: Radius = <<BreadboardConfig>>.screw_corehole / 2
FEATURE [Part::MultiFuse] Fusion020
  Placement = pos=(0,-50,0) rot=(0,0,1;0rad)
  Shapes = -> [Cylinder419,Cylinder418,Cylinder417,Cylinder416,Cylinder415,Cylinder414,Cylinder413,Cylinder412,Cylinder411,Cylinder410,Cylinder409,Cylinder408,Cylinder407,Cylinder406,Cylinder405,Cylinder404,Cylinder403,Cylinder402,Cylinder401,Cylinder400,Cylinder420]
  expr: .Placement.Base.y = <<BreadboardConfig>>.screw_spacing * -10
FEATURE [Part::Cylinder] Cylinder421
  Angle = 360
  AttacherType = Attacher::AttachEngine3D
  FirstAngle = 0
  Height = 2
  Placement = pos=(5,0,0) rot=(0,0,1;0rad)
  Radius = 1.65
  SecondAngle = 0
  expr: .Placement.Base.x = <<BreadboardConfig>>.screw_spacing * 1
  expr: Height = <<BreadboardConfig>>.t_plate
  expr: Radius = <<BreadboardConfig>>.screw_corehole / 2
FEATURE [Part::Cylinder] Cylinder422
  Angle = 360
  AttacherType = Attacher::AttachEngine3D
  FirstAngle = 0
  Height = 2
  Placement = pos=(10,0,0) rot=(0,0,1;0rad)
  Radius = 1.65
  SecondAngle = 0
  expr: .Placement.Base.x = <<BreadboardConfig>>.screw_spacing * 2
  expr: Height = <<BreadboardConfig>>.t_plate
  expr: Radius = <<BreadboardConfig>>.screw_corehole / 2
FEATURE [Part::Cylinder] Cylinder423
  Angle = 360
  AttacherType = Attacher::AttachEngine3D
  FirstAngle = 0
  Height = 2
  Placement = pos=(15,0,0) rot=(0,0,1;0rad)
  Radius = 1.65
  SecondAngle = 0
  expr: .Placement.Base.x = <<BreadboardConfig>>.screw_spacing * 3
  expr: Height = <<BreadboardConfig>>.t_plate
  expr: Radius = <<BreadboardConfig>>.screw_corehole / 2
FEATURE [Part::Cylinder] Cylinder424
  Angle = 360
  AttacherType = Attacher::AttachEngine3D
  FirstAngle = 0
  Height = 2
  Placement = pos=(20,0,0) rot=(0,0,1;0rad)
  Radius = 1.65
  SecondAngle = 0
  expr: .Placement.Base.x = <<BreadboardConfig>>.screw_spacing * 4
  expr: Height = <<BreadboardConfig>>.t_plate
  expr: Radius = <<BreadboardConfig>>.screw_corehole / 2
FEATURE [Part::Cylinder] Cylinder425
  Angle = 360
  AttacherType = Attacher::AttachEngine3D
  FirstAngle = 0
  Height = 2
  Placement = pos=(25,0,0) rot=(0,0,1;0rad)
  Radius = 1.65
  SecondAngle = 0
  expr: .Placement.Base.x = <<BreadboardConfig>>.screw_spacing * 5
  expr: Height = <<BreadboardConfig>>.t_plate
  expr: Radius = <<BreadboardConfig>>.screw_corehole / 2
FEATURE [Part::Cylinder] Cylinder426
  Angle = 360
  AttacherType = Attacher::AttachEngine3D
  FirstAngle = 0
  Height = 2
  Placement = pos=(30,0,0) rot=(0,0,1;0rad)
  Radius = 1.65
  SecondAngle = 0
  expr: .Placement.Base.x = <<BreadboardConfig>>.screw_spacing * 6
  expr: Height = <<BreadboardConfig>>.t_plate
  expr: Radius = <<BreadboardConfig>>.screw_corehole / 2
FEATURE [Part::Cylinder] Cylinder427
  Angle = 360
  AttacherType = Attacher::AttachEngine3D
  FirstAngle = 0
  Height = 2
  Placement = pos=(35,0,0) rot=(0,0,1;0rad)
  Radius = 1.65
  SecondAngle = 0
  expr: .Placement.Base.x = <<BreadboardConfig>>.screw_spacing * 7
  expr: Height = <<BreadboardConfig>>.t_plate
  expr: Radius = <<BreadboardConfig>>.screw_corehole / 2
FEATURE [Part::Cylinder] Cylinder428
  Angle = 360
  AttacherType = Attacher::AttachEngine3D
  FirstAngle = 0
  Height = 2
  Placement = pos=(40,0,0) rot=(0,0,1;0rad)
  Radius = 1.65
  SecondAngle = 0
  expr: .Placement.Base.x = <<BreadboardConfig>>.screw_spacing * 8
  expr: Height = <<BreadboardConfig>>.t_plate
  expr: Radius = <<BreadboardConfig>>.screw_corehole / 2
FEATURE [Part::Cylinder] Cylinder429
  Angle = 360
  AttacherType = Attacher::AttachEngine3D
  FirstAngle = 0
  Height = 2
  Placement = pos=(45,0,0) rot=(0,0,1;0rad)
  Radius = 1.65
  SecondAngle = 0
  expr: .Placement.Base.x = <<BreadboardConfig>>.screw_spacing * 9
  expr: Height = <<BreadboardConfig>>.t_plate
  expr: Radius = <<BreadboardConfig>>.screw_corehole / 2
FEATURE [Part::Cylinder] Cylinder430
  Angle = 360
  AttacherType = Attacher::AttachEngine3D
  FirstAngle = 0
  Height = 2
  Placement = pos=(50,0,0) rot=(0,0,1;0rad)
  Radius = 1.65
  SecondAngle = 0
  expr: .Placement.Base.x = <<BreadboardConfig>>.screw_spacing * 10
  expr: Height = <<BreadboardConfig>>.t_plate
  expr: Radius = <<BreadboardConfig>>.screw_corehole / 2
FEATURE [Part::Cylinder] Cylinder431
  Angle = 360
  AttacherType = Attacher::AttachEngine3D
  FirstAngle = 0
  Height = 2
  Placement = pos=(-5,0,0) rot=(0,0,1;0rad)
  Radius = 1.65
  SecondAngle = 0
  expr: .Placement.Base.x = <<BreadboardConfig>>.screw_spacing * -1
  expr: Height = <<BreadboardConfig>>.t_plate
  expr: Radius = <<BreadboardConfig>>.screw_corehole / 2
FEATURE [Part::Cylinder] Cylinder432
  Angle = 360
  AttacherType = Attacher::AttachEngine3D
  FirstAngle = 0
  Height = 2
  Placement = pos=(-10,0,0) rot=(0,0,1;0rad)
  Radius = 1.65
  SecondAngle = 0
  expr: .Placement.Base.x = <<BreadboardConfig>>.screw_spacing * -2
  expr: Height = <<BreadboardConfig>>.t_plate
  expr: Radius = <<BreadboardConfig>>.screw_corehole / 2
FEATURE [Part::Cylinder] Cylinder433
  Angle = 360
  AttacherType = Attacher::AttachEngine3D
  FirstAngle = 0
  Height = 2
  Placement = pos=(-15,0,0) rot=(0,0,1;0rad)
  Radius = 1.65
  SecondAngle = 0
  expr: .Placement.Base.x = <<BreadboardConfig>>.screw_spacing * -3
  expr: Height = <<BreadboardConfig>>.t_plate
  expr: Radius = <<BreadboardConfig>>.screw_corehole / 2
FEATURE [Part::Cylinder] Cylinder434
  Angle = 360
  AttacherType = Attacher::AttachEngine3D
  FirstAngle = 0
  Height = 2
  Placement = pos=(-20,0,0) rot=(0,0,1;0rad)
  Radius = 1.65
  SecondAngle = 0
  expr: .Placement.Base.x = <<BreadboardConfig>>.screw_spacing * -4
  expr: Height = <<BreadboardConfig>>.t_plate
  expr: Radius = <<BreadboardConfig>>.screw_corehole / 2
FEATURE [Part::Cylinder] Cylinder435
  Angle = 360
  AttacherType = Attacher::AttachEngine3D
  FirstAngle = 0
  Height = 2
  Placement = pos=(-25,0,0) rot=(0,0,1;0rad)
  Radius = 1.65
  SecondAngle = 0
  expr: .Placement.Base.x = <<BreadboardConfig>>.screw_spacing * -5
  expr: Height = <<BreadboardConfig>>.t_plate
  expr: Radius = <<BreadboardConfig>>.screw_corehole / 2
FEATURE [Part::Cylinder] Cylinder436
  Angle = 360
  AttacherType = Attacher::AttachEngine3D
  FirstAngle = 0
  Height = 2
  Placement = pos=(-30,0,0) rot=(0,0,1;0rad)
  Radius = 1.65
  SecondAngle = 0
  expr: .Placement.Base.x = <<BreadboardConfig>>.screw_spacing * -6
  expr: Height = <<BreadboardConfig>>.t_plate
  expr: Radius = <<BreadboardConfig>>.screw_corehole / 2
FEATURE [Part::Cylinder] Cylinder437
  Angle = 360
  AttacherType = Attacher::AttachEngine3D
  FirstAngle = 0
  Height = 2
  Placement = pos=(-35,0,0) rot=(0,0,1;0rad)
  Radius = 1.65
  SecondAngle = 0
  expr: .Placement.Base.x = <<BreadboardConfig>>.screw_spacing * -7
  expr: Height = <<BreadboardConfig>>.t_plate
  expr: Radius = <<BreadboardConfig>>.screw_corehole / 2
FEATURE [Part::Cylinder] Cylinder438
  Angle = 360
  AttacherType = Attacher::AttachEngine3D
  FirstAngle = 0
  Height = 2
  Placement = pos=(-40,0,0) rot=(0,0,1;0rad)
  Radius = 1.65
  SecondAngle = 0
  expr: .Placement.Base.x = <<BreadboardConfig>>.screw_spacing * -8
  expr: Height = <<BreadboardConfig>>.t_plate
  expr: Radius = <<BreadboardConfig>>.screw_corehole / 2
FEATURE [Part::Cylinder] Cylinder439
  Angle = 360
  AttacherType = Attacher::AttachEngine3D
  FirstAngle = 0
  Height = 2
  Placement = pos=(-45,0,0) rot=(0,0,1;0rad)
  Radius = 1.65
  SecondAngle = 0
  expr: .Placement.Base.x = <<BreadboardConfig>>.screw_spacing * -9
  expr: Height = <<BreadboardConfig>>.t_plate
  expr: Radius = <<BreadboardConfig>>.screw_corehole / 2
FEATURE [Part::Cylinder] Cylinder440
  Angle = 360
  AttacherType = Attacher::AttachEngine3D
  FirstAngle = 0
  Height = 2
  Placement = pos=(-50,0,0) rot=(0,0,1;0rad)
  Radius = 1.65
  SecondAngle = 0
  expr: .Placement.Base.x = <<BreadboardConfig>>.screw_spacing * -10
  expr: Height = <<BreadboardConfig>>.t_plate
  expr: Radius = <<BreadboardConfig>>.screw_corehole / 2
FEATURE [Part::Cylinder] Cylinder441
  Angle = 360
  AttacherType = Attacher::AttachEngine3D
  FirstAngle = 0
  Height = 2
  Radius = 1.65
  SecondAngle = 0
  expr: Height = <<BreadboardConfig>>.t_plate
  expr: Radius = <<BreadboardConfig>>.screw_corehole / 2
FEATURE [Part::MultiFuse] Fusion022
  Placement = pos=(0,-35,0) rot=(0,0,1;0rad)
  Shapes = -> [Cylinder440,Cylinder439,Cylinder438,Cylinder437,Cylinder436,Cylinder435,Cylinder434,Cylinder433,Cylinder432,Cylinder431,Cylinder430,Cylinder429,Cylinder428,Cylinder427,Cylinder426,Cylinder425,Cylinder424,Cylinder423,Cylinder422,Cylinder421,Cylinder441]
  expr: .Placement.Base.y = <<BreadboardConfig>>.screw_spacing * -7
FEATURE [Part::MultiFuse] Fusion021  label="HoleMatrix"
  Shapes = -> [Fusion020,Fusion003,Fusion004,Fusion005,Fusion006,Fusion007,Fusion008,Fusion009,Fusion010,Fusion011,Fusion012,Fusion013,Fusion014,Fusion015,Fusion016,Fusion017,Fusion018,Fusion019,Fusion002,Fusion001,Fusion022]
FEATURE [Part::Cut] Cut
  Base = -> Fusion
  Tool = -> Fusion021
